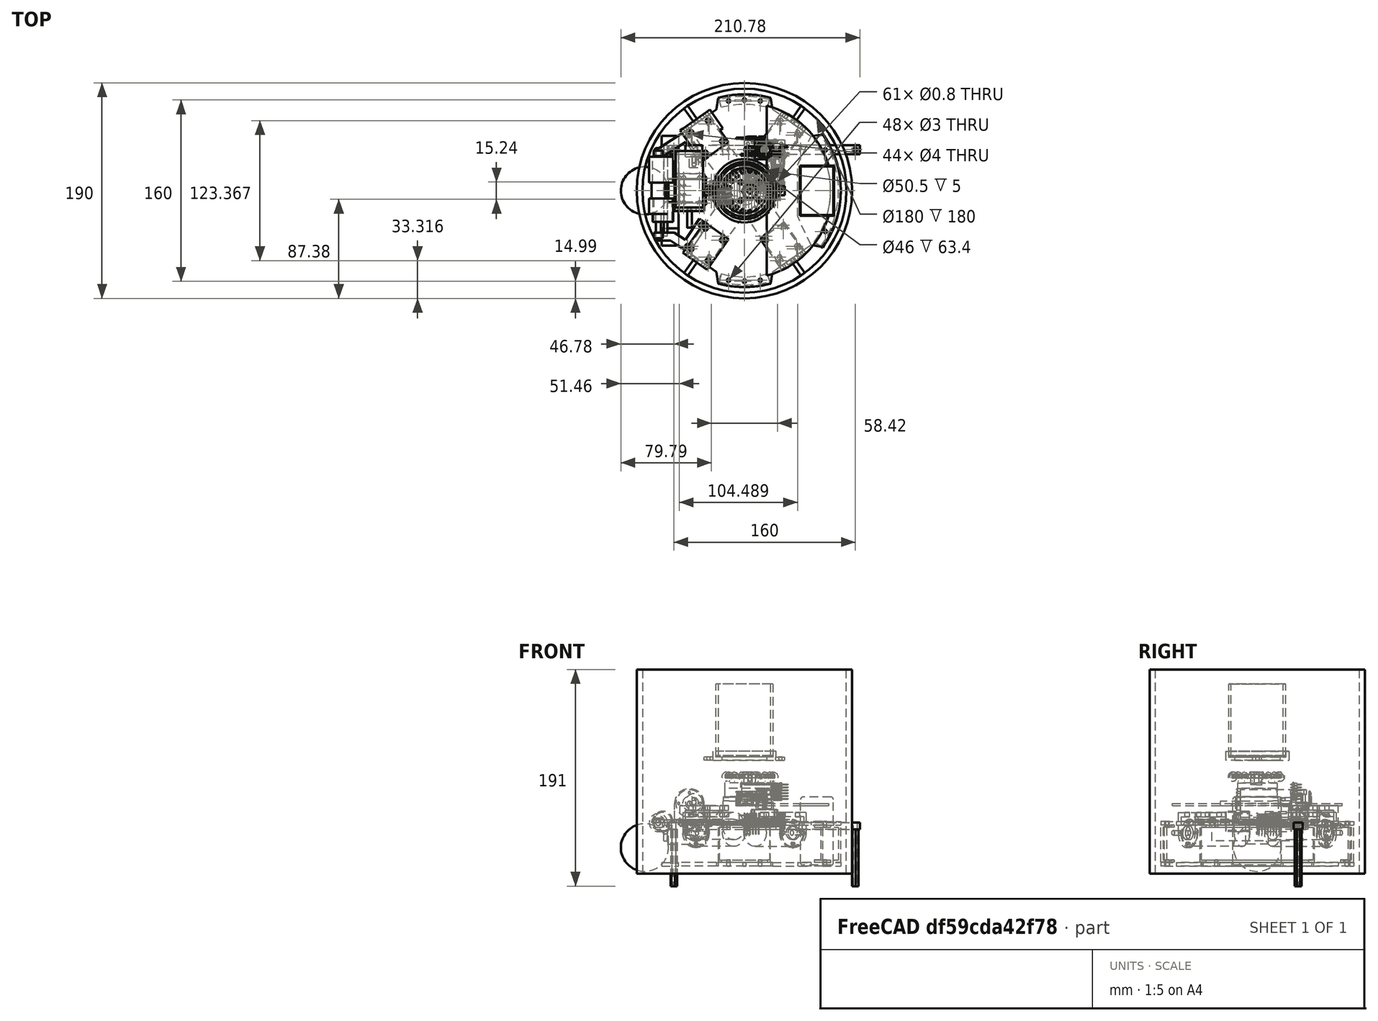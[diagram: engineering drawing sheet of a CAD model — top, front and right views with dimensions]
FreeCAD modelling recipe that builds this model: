
FCSTD DOCUMENT  (FreeCAD 0.21R33668 +7 (Git))
Label: SN9-10_model
License: All rights reserved
LicenseURL: https://en.wikipedia.org/wiki/All_rights_reserved
objects: Part::Feature×304, Sketcher::SketchObject×75, App::Part×51, PartDesign::Pad×48, PartDesign::Pocket×47, PartDesign::Body×31, PartDesign::SubShapeBinder×27, PartDesign::PolarPattern×11, PartDesign::Revolution×4, Part::FeaturePython×2, Part::Sphere×1, PartDesign::Fillet×1, Part::Cylinder×1, Part::Cut×1
note: 653 computed .brp shape members not serialized (recipe doc carries the construction recipe); baked Part::Feature solids carry a one-line shape summary decoded from their .brp

FEATURE [Sketcher::SketchObject] Sketch
  FullyConstrained = true
  MapMode = 5
  Support = -> [XY_Plane008]
  sketch-geometry (1):
    g0: Circle CenterX=0 CenterY=0 CenterZ=0 NormalX=0 NormalY=0 NormalZ=1 AngleXU=0 Radius=85
  constraints (2):
    c: Coincident(g0,g-1)
    c: Diameter(g0) = 170
FEATURE [Sketcher::SketchObject] Sketch005
  FullyConstrained = true
  MapMode = 5
  Placement = pos=(0,0,0) rot=(1,0,0;1.5708rad)
  Support = -> [XZ_Plane009]
  sketch-geometry (6):
    g0: ArcOfHyperbola CenterX=0 CenterY=94.5 CenterZ=0 NormalX=0 NormalY=0 NormalZ=1 MajorRadius=17.5 MinorRadius=15.6742 AngleXU=1.5708 StartAngle=0 EndAngle=1.02375
    g1: LineSegment StartX=5e-16 StartY=112 StartZ=0 EndX=-5e-16 EndY=77 EndZ=0
    g2: LineSegment StartX=-15.6742 StartY=112 StartZ=0 EndX=15.6742 EndY=112 EndZ=0
    g3: GeomPoint X=2.6e-15 Y=117.993 Z=0
    g4: LineSegment StartX=-19 StartY=122 StartZ=0 EndX=0 EndY=122 EndZ=0
    g5: LineSegment StartX=0 StartY=112 StartZ=0 EndX=0 EndY=122 EndZ=0
  constraints (15):
    c: InternalAlignment(g1,g0)
    c: InternalAlignment(g2,g0)
    c: InternalAlignment(g3,g0)
    c: Horizontal(g2)
    c: PointOnObject(g0,g-2)
    c: PointOnObject(g0,g-2)
    c: DistanceY(g0,g0) = 10
    c: DistanceX(g0,g0) = 19
    c: DistanceY(g1,g0) = 35
    c: Coincident(g4,g0)
    c: Coincident(g5,g0)
    c: Coincident(g5,g4)
    c: Vertical(g5)
    c: Horizontal(g4)
    c: DistanceY(g-1,g0) = 112
FEATURE [PartDesign::Pad] Pad  label="Structural layer"
  Direction = (0,0,1)
  Length = 3
  Length2 = 10
  Profile = -> Sketch
  ReferenceAxis = -> Sketch [N_Axis]
  Type = 0
FEATURE [Sketcher::SketchObject] Sketch001
  ExternalGeometry = -> [Pad]
  FullyConstrained = false
  MapMode = 5
  Placement = pos=(0,0,3) rot=(0,0,1;0rad)
  Support = -> [Pad]
  sketch-geometry (7):
    g0: LineSegment StartX=-10.6686 StartY=100.741 StartZ=0 EndX=44.4806 EndY=91.0164 EndZ=0
    g1: LineSegment StartX=44.4806 StartY=91.0164 StartZ=0 EndX=41.5109 EndY=74.1744 EndZ=0
    g2: LineSegment StartX=32.942 StartY=68.1744 StartZ=0 EndX=-7.63834 EndY=75.3298 EndZ=0
    g3: LineSegment StartX=-13.6383 StartY=83.8987 StartZ=0 EndX=-10.6686 EndY=100.741 EndZ=0
    g4: LineSegment StartX=32.942 StartY=68.1744 StartZ=0 EndX=41.5109 EndY=74.1744 EndZ=0
    g5: LineSegment StartX=-13.6383 StartY=83.8987 StartZ=0 EndX=-7.63834 EndY=75.3298 EndZ=0
    g6: LineSegment StartX=-98.5042 StartY=90.5189 StartZ=0 EndX=89.0462 EndY=57.4487 EndZ=0
  constraints (18):
    c: Coincident(g0,g1)
    c: Coincident(g3,g0)
    c: Coincident(g4,g2)
    c: Coincident(g4,g1)
    c: Coincident(g5,g3)
    c: Coincident(g5,g2)
    c: Angle(g4,g2) = 2.35619
    c: Angle(g2,g5) = 2.35619
    c: DistanceX(g3,g2) = 6
    c: Angle(g6,g-1) = 0.174533
    c: Parallel(g2,g6)
    c: Parallel(g0,g2)
    c: Perpendicular(g6,g1)
    c: Equal(g1,g3)
    c: Parallel(g1,g3)
    c: PointOnObject(g3,g-3)
    c: PointOnObject(g1,g-3)
    c: Distance(g0) = 56
FEATURE [PartDesign::Pocket] Pocket
  BaseFeature = -> Pad
  Direction = (0,0,-1)
  Length = 5
  Length2 = 5
  Profile = -> Sketch001
  ReferenceAxis = -> Sketch001 [N_Axis]
  Type = 1
FEATURE [PartDesign::PolarPattern] PolarPattern
  Angle = 110
  Axis = -> Sketch001 [N_Axis]
  BaseFeature = -> Pocket
  Occurrences = 2
  Originals = -> [Pocket]
FEATURE [PartDesign::Revolution] Revolution
  Angle = 360
  Axis = (0,-2e-16,1)
  Base = (0,0,0)
  Placement = pos=(0,0,0) rot=(1,0,0;1.5708rad)
  Profile = -> Sketch005
  ReferenceAxis = -> Sketch005 [V_Axis]
FEATURE [Sketcher::SketchObject] Sketch015
  FullyConstrained = true
  MapMode = 5
  Placement = pos=(0,0,3) rot=(0,0,1;0rad)
  Support = -> [PolarPattern]
  sketch-geometry (4):
    g0: LineSegment StartX=-111 StartY=31 StartZ=0 EndX=-31 EndY=111 EndZ=0
    g1: LineSegment StartX=-31 StartY=111 StartZ=0 EndX=-1 EndY=81 EndZ=0
    g2: LineSegment StartX=-1 StartY=81 StartZ=0 EndX=-81 EndY=1 EndZ=0
    g3: LineSegment StartX=-81 StartY=1 StartZ=0 EndX=-111 EndY=31 EndZ=0
  constraints (12):
    c: Coincident(g0,g1)
    c: Coincident(g1,g2)
    c: Coincident(g2,g3)
    c: Coincident(g3,g0)
    c: Equal(g3,g1)
    c: Equal(g0,g2)
    c: Angle(g3,g0) = 1.5708
    c: DistanceX(g2,g-1) = 81
    c: DistanceY(g-1,g1) = 81
    c: DistanceX(g0,g1) = 30
    c: DistanceX(g2,g1) = 80
    c: Angle(g-1,g2) = 0.785398
FEATURE [PartDesign::Pocket] Pocket004
  BaseFeature = -> PolarPattern
  Direction = (0,0,-1)
  Length = 5
  Length2 = 5
  Profile = -> Sketch015
  ReferenceAxis = -> Sketch015 [N_Axis]
  Type = 1
FEATURE [Sketcher::SketchObject] Sketch016
  FullyConstrained = true
  MapMode = 5
  Placement = pos=(0,0,0) rot=(1,0,0;1.5708rad)
  Support = -> [XZ_Plane016]
  sketch-geometry (8):
    g0: LineSegment StartX=-88 StartY=-1 StartZ=0 EndX=-79 EndY=-1 EndZ=0
    g1: LineSegment StartX=-79 StartY=-34 StartZ=0 EndX=-88 EndY=-34 EndZ=0
    g2: LineSegment StartX=-88 StartY=-34 StartZ=0 EndX=-88 EndY=-1 EndZ=0
    g3: LineSegment StartX=-79 StartY=-1 StartZ=0 EndX=-79 EndY=-3 EndZ=0
    g4: LineSegment StartX=-79 StartY=-3 StartZ=0 EndX=-86 EndY=-3 EndZ=0
    g5: LineSegment StartX=-86 StartY=-3 StartZ=0 EndX=-86 EndY=-32 EndZ=0
    g6: LineSegment StartX=-86 StartY=-32 StartZ=0 EndX=-79 EndY=-32 EndZ=0
    g7: LineSegment StartX=-79 StartY=-32 StartZ=0 EndX=-79 EndY=-34 EndZ=0
  constraints (24):
    c: Coincident(g1,g2)
    c: Coincident(g2,g0)
    c: Horizontal(g0)
    c: Horizontal(g1)
    c: Vertical(g2)
    c: DistanceY(g1,g0) = 33
    c: DistanceX(g1,g1) = 9
    c: DistanceX(g0,g-1) = 88
    c: DistanceY(g1,g-1) = 34
    c: Equal(g1,g0)
    c: Coincident(g3,g0)
    c: Vertical(g3)
    c: Coincident(g4,g3)
    c: Horizontal(g4)
    c: Coincident(g5,g4)
    c: Vertical(g5)
    c: Coincident(g6,g5)
    c: Horizontal(g6)
    c: Coincident(g7,g6)
    c: Coincident(g7,g1)
    c: Vertical(g7)
    c: Equal(g3,g7)
    c: DistanceY(g3,g3) = 2
    c: DistanceX(g0,g4) = 2
FEATURE [PartDesign::Revolution] Revolution001
  Angle = 30
  Axis = (1e-16,1e-16,1)
  Base = (0,0,0)
  Midplane = true
  Placement = pos=(0,0,0) rot=(1,0,0;1.5708rad)
  Profile = -> Sketch016
  ReferenceAxis = -> Z_Axis016
  Reversed = true
FEATURE [Part::Feature] Part__Feature268  label="OmniBase_Predeterminado004"
  Placement = pos=(4.80373,-0.638646,40.5) rot=(0,0,1;0rad)
  shape: bbox 44 x 43.9 x 9 mm, 104 faces (baked)
FEATURE [Part::Feature] Part__Feature269  label="Roller_Predeterminado072"
  Placement = pos=(4.80373,20.3614,41.6192) rot=(0,0,1;0rad)
  shape: bbox 2.6 x 8.659 x 8.659 mm, 10 faces (baked)
FEATURE [Part::Feature] Part__Feature270  label="Roller_Predeterminado073"
  Placement = pos=(-2.3787,19.0949,41.6192) rot=(0,0,1;0.349066rad)
  shape: bbox 4.664 x 8.342 x 8.659 mm, 10 faces (baked)
FEATURE [Part::Feature] Part__Feature271  label="Roller_Predeterminado074"
  Placement = pos=(-8.69481,15.4483,41.6192) rot=(0,0,1;0.698132rad)
  shape: bbox 6.71 x 7.451 x 8.659 mm, 10 faces (baked)
FEATURE [Part::Feature] Part__Feature272  label="Roller_Predeterminado075"
  Placement = pos=(-13.3828,9.86135,41.6192) rot=(0,0,1;1.0472rad)
  shape: bbox 7.965 x 5.765 x 8.659 mm, 10 faces (baked)
FEATURE [Part::Feature] Part__Feature273  label="Roller_Predeterminado076"
  Placement = pos=(-15.8772,3.00797,41.6192) rot=(0,0,1;1.39626rad)
  shape: bbox 8.632 x 3.688 x 8.659 mm, 10 faces (baked)
FEATURE [Part::Feature] Part__Feature274  label="Roller_Predeterminado077"
  Placement = pos=(-15.8772,-4.28526,41.6192) rot=(0,0,1;1.74533rad)
  shape: bbox 8.632 x 3.688 x 8.659 mm, 10 faces (baked)
FEATURE [Part::Feature] Part__Feature275  label="Roller_Predeterminado078"
  Placement = pos=(-13.3828,-11.1386,41.6192) rot=(0,0,1;2.0944rad)
  shape: bbox 7.965 x 5.765 x 8.659 mm, 10 faces (baked)
FEATURE [Part::Feature] Part__Feature276  label="Roller_Predeterminado079"
  Placement = pos=(-8.69481,-16.7256,41.6192) rot=(0,0,1;2.44346rad)
  shape: bbox 6.71 x 7.451 x 8.659 mm, 10 faces (baked)
FEATURE [Part::Feature] Part__Feature277  label="Roller_Predeterminado080"
  Placement = pos=(-2.3787,-20.3722,41.6192) rot=(0,0,1;2.79253rad)
  shape: bbox 4.664 x 8.342 x 8.659 mm, 10 faces (baked)
FEATURE [Part::Feature] Part__Feature278  label="Roller_Predeterminado081"
  Placement = pos=(4.80373,-21.6386,41.6192) rot=(0,0,1;3.14159rad)
  shape: bbox 2.6 x 8.659 x 8.659 mm, 10 faces (baked)
FEATURE [Part::Feature] Part__Feature279  label="Roller_Predeterminado082"
  Placement = pos=(11.9862,-20.3722,41.6192) rot=(0,0,1;3.49066rad)
  shape: bbox 4.664 x 8.342 x 8.659 mm, 10 faces (baked)
FEATURE [Part::Feature] Part__Feature280  label="Roller_Predeterminado083"
  Placement = pos=(18.3023,-16.7256,41.6192) rot=(0,0,1;3.83972rad)
  shape: bbox 6.71 x 7.451 x 8.659 mm, 10 faces (baked)
FEATURE [Part::Feature] Part__Feature281  label="Roller_Predeterminado084"
  Placement = pos=(22.9903,-11.1386,41.6192) rot=(0,0,-1;2.0944rad)
  shape: bbox 7.965 x 5.765 x 8.659 mm, 10 faces (baked)
FEATURE [Part::Feature] Part__Feature282  label="Roller_Predeterminado085"
  Placement = pos=(25.4847,-4.28526,41.6192) rot=(0,0,-1;1.74533rad)
  shape: bbox 8.632 x 3.688 x 8.659 mm, 10 faces (baked)
FEATURE [Part::Feature] Part__Feature283  label="Roller_Predeterminado086"
  Placement = pos=(25.4847,3.00797,41.6192) rot=(0,0,-1;1.39626rad)
  shape: bbox 8.632 x 3.688 x 8.659 mm, 10 faces (baked)
FEATURE [Part::Feature] Part__Feature284  label="Roller_Predeterminado087"
  Placement = pos=(22.9903,9.86135,41.6192) rot=(0,0,-1;1.0472rad)
  shape: bbox 7.965 x 5.765 x 8.659 mm, 10 faces (baked)
FEATURE [Part::Feature] Part__Feature285  label="Roller_Predeterminado088"
  Placement = pos=(18.3023,15.4483,41.6192) rot=(0,0,-1;0.698132rad)
  shape: bbox 6.71 x 7.451 x 8.659 mm, 10 faces (baked)
FEATURE [Part::Feature] Part__Feature286  label="Roller_Predeterminado089"
  Placement = pos=(11.9862,19.0949,41.6192) rot=(0,0,-1;0.349066rad)
  shape: bbox 4.664 x 8.342 x 8.659 mm, 10 faces (baked)
FEATURE [Part::Feature] Part__Feature287  label="Nut_Predeterminado004"
  Placement = pos=(4.80373,-0.638646,43.5) rot=(0,0,1;1.0472rad)
  shape: bbox 13.86 x 12.93 x 2 mm, 24 faces (baked)
FEATURE [App::Part] OmniWheel054  label="OmniWheel 1"
  Group = -> [Part__Feature268,Part__Feature269,Part__Feature270,Part__Feature271,Part__Feature272,Part__Feature273,Part__Feature274,Part__Feature275,Part__Feature276,Part__Feature277,Part__Feature278,Part__Feature279,Part__Feature280,Part__Feature281,Part__Feature282,Part__Feature283,Part__Feature284,Part__Feature285,Part__Feature286,Part__Feature287]
  Origin = -> Origin019
  Placement = pos=(-23.8855,35.1581,-6.8) rot=(-0.419215,-0.805305,-0.419215;1.78566rad)
FEATURE [Sketcher::SketchObject] Sketch023
  FullyConstrained = true
  MapMode = 5
  Support = -> [XY_Plane024]
  sketch-geometry (9):
    g0: Circle CenterX=0 CenterY=0 CenterZ=0 NormalX=0 NormalY=0 NormalZ=1 AngleXU=0 Radius=20
    g1: LineSegment StartX=27.7128 StartY=-4 StartZ=0 EndX=35.7128 EndY=-4 EndZ=0
    g2: LineSegment StartX=35.7128 StartY=-4 StartZ=0 EndX=35.7128 EndY=4 EndZ=0
    g3: LineSegment StartX=35.7128 StartY=4 StartZ=0 EndX=27.7128 EndY=4 EndZ=0
    g4: LineSegment StartX=-27.7128 StartY=-4 StartZ=0 EndX=-35.7128 EndY=-4 EndZ=0
    g5: LineSegment StartX=-35.7128 StartY=-4 StartZ=0 EndX=-35.7128 EndY=4 EndZ=0
    g6: LineSegment StartX=-35.7128 StartY=4 StartZ=0 EndX=-27.7128 EndY=4 EndZ=0
    g7: ArcOfCircle CenterX=0 CenterY=0 CenterZ=0 NormalX=0 NormalY=0 NormalZ=1 AngleXU=0 Radius=28 StartAngle=0.143348 EndAngle=2.99825
    g8: ArcOfCircle CenterX=0 CenterY=0 CenterZ=0 NormalX=0 NormalY=0 NormalZ=1 AngleXU=0 Radius=28 StartAngle=3.28494 EndAngle=6.13984
  constraints (25):
    c: Coincident(g0,g-1)
    c: Diameter(g0) = 40
    c: Horizontal(g1)
    c: Coincident(g2,g1)
    c: Coincident(g3,g2)
    c: Horizontal(g3)
    c: Horizontal(g4)
    c: Coincident(g5,g4)
    c: Vertical(g5)
    c: Coincident(g6,g5)
    c: Horizontal(g6)
    c: Coincident(g7,g0)
    c: Coincident(g7,g6)
    c: Coincident(g7,g3)
    c: Coincident(g8,g0)
    c: Coincident(g8,g4)
    c: Coincident(g8,g1)
    c: Diameter(g7) = 56
    c: Diameter(g8) = 56
    c: Symmetric(g1,g2,g-1)
    c: Equal(g5,g2)
    c: Equal(g6,g3)
    c: Equal(g4,g1)
    c: DistanceY(g2,g2) = 8
    c: DistanceX(g6,g6) = 8
FEATURE [PartDesign::Pad] Pad007
  Direction = (0,0,1)
  Length = 3
  Length2 = 10
  Profile = -> Sketch023
  ReferenceAxis = -> Sketch023 [N_Axis]
  Type = 0
FEATURE [Sketcher::SketchObject] Sketch025
  FullyConstrained = true
  MapMode = 5
  Support = -> [XY_Plane026]
  sketch-geometry (2):
    g0: Circle CenterX=0 CenterY=0 CenterZ=0 NormalX=0 NormalY=0 NormalZ=1 AngleXU=0 Radius=90
    g1: Circle CenterX=0 CenterY=0 CenterZ=0 NormalX=0 NormalY=0 NormalZ=1 AngleXU=0 Radius=95
  constraints (4):
    c: Diameter(g0) = 180
    c: Coincident(g1,g-1)
    c: Diameter(g1) = 190
    c: Coincident(g0,g-1)
FEATURE [PartDesign::Pad] Pad008
  Direction = (0,0,1)
  Length = 180
  Length2 = 10
  Profile = -> Sketch025
  ReferenceAxis = -> Sketch025 [N_Axis]
  Type = 0
FEATURE [PartDesign::Body] Body008  label="Cylinder"
  Group = -> [Sketch025,Pad008]
  Origin = -> Origin026
  Placement = pos=(0,0,-44) rot=(0,0,1;0rad)
  Tip = -> Pad008
FEATURE [Sketcher::SketchObject] Sketch061
  FullyConstrained = true
  MapMode = 5
  Placement = pos=(0,0,2) rot=(0,0,1;0rad)
  sketch-geometry (1):
    g0: Circle CenterX=0 CenterY=0 CenterZ=0 NormalX=0 NormalY=0 NormalZ=1 AngleXU=0 Radius=12.5
  constraints (2):
    c: Coincident(g0,g-1)
    c: Diameter(g0) = 25
FEATURE [PartDesign::Pocket] Pocket019
  BaseFeature = -> Pocket004
  Direction = (0,0,-1)
  Length = 5
  Length2 = 5
  Profile = -> Sketch061
  ReferenceAxis = -> Sketch061 [N_Axis]
  Type = 4
FEATURE [Part::Feature] Part__Feature439  label="114-00841-68--3DModel-STEP-56544 v1"
  Placement = pos=(24.0935,-0.00012972,0.814608) rot=(0.57735,0.57735,0.57735;2.0944rad)
  shape: bbox 11.35 x 11.95 x 1.68 mm, 239 faces (baked)
FEATURE [Part::Feature] Part__Feature453  label="MIMXRT1052CVJ5B v1"
  Placement = pos=(1.30183,-0.0809243,0.815) rot=(0,0.707107,0.707107;3.14159rad)
  shape: bbox 12 x 12 x 1.27 mm, 6 faces (baked)
FEATURE [App::Part] MIMXRT1052CVJ5B_v1  label="MIMXRT1052CVJ5B v198"
  Group = -> [Part__Feature453]
  Origin = -> Origin053
FEATURE [Part::Feature] Part__Feature589  label="MicroUSB Molex 473460001 v1"
  Placement = pos=(-28.9499,0.13174,2.07033) rot=(0.57735,-0.57735,-0.57735;2.0944rad)
  shape: bbox 5.43 x 7.98 x 2.94 mm, 406 faces (baked)
FEATURE [Part::Feature] Part__Feature590  label="COMPOUND"
  shape: bbox 2.54 x 2.54 x 2.799 mm, 22 faces, 0 solids (baked)
FEATURE [Part::Feature] Part__Feature591  label="COMPOUND001"
  shape: bbox 2.54 x 2.54 x 2.799 mm, 22 faces, 0 solids (baked)
FEATURE [Part::Feature] Part__Feature592  label="COMPOUND002"
  shape: bbox 2.54 x 2.54 x 2.799 mm, 23 faces, 0 solids (baked)
FEATURE [Part::Feature] Part__Feature593  label="COMPOUND003"
  shape: bbox 2.54 x 2.54 x 2.799 mm, 22 faces, 0 solids (baked)
FEATURE [Part::Feature] Part__Feature594  label="COMPOUND004"
  shape: bbox 2.54 x 2.54 x 2.799 mm, 22 faces, 0 solids (baked)
FEATURE [Part::Feature] Part__Feature595  label="COMPOUND005"
  shape: bbox 2.54 x 2.54 x 2.799 mm, 23 faces, 0 solids (baked)
FEATURE [App::Part] COMPOUND  label="COMPOUND006"
  Group = -> [Part__Feature590,Part__Feature591,Part__Feature592,Part__Feature593,Part__Feature594,Part__Feature595]
  Origin = -> Origin055
FEATURE [Part::Feature] Part__Feature596  label="COMPOUND007"
  shape: bbox 0.6304 x 0.63 x 12.7 mm, 14 faces (baked)
FEATURE [Part::Feature] Part__Feature597  label="COMPOUND008"
  shape: bbox 0.6304 x 0.63 x 12.7 mm, 14 faces (baked)
FEATURE [Part::Feature] Part__Feature598  label="COMPOUND009"
  shape: bbox 0.6304 x 0.63 x 12.7 mm, 14 faces (baked)
FEATURE [Part::Feature] Part__Feature599  label="COMPOUND010"
  shape: bbox 0.6304 x 0.63 x 12.7 mm, 14 faces (baked)
FEATURE [Part::Feature] Part__Feature600  label="COMPOUND011"
  shape: bbox 0.6304 x 0.63 x 12.7 mm, 14 faces (baked)
FEATURE [Part::Feature] Part__Feature601  label="COMPOUND012"
  shape: bbox 0.6304 x 0.63 x 12.7 mm, 14 faces (baked)
FEATURE [App::Part] COMPOUND001  label="COMPOUND013"
  Group = -> [Part__Feature596,Part__Feature597,Part__Feature598,Part__Feature599,Part__Feature600,Part__Feature601]
  Origin = -> Origin056
FEATURE [App::Part] Pin_Header_1x6_TH_Pitch_2_54mm_v1  label="Pin Header 1x6 TH Pitch 2.54mm v1"
  Group = -> [COMPOUND,COMPOUND001]
  Origin = -> Origin054
  Placement = pos=(-16.51,-7.62,-0.814) rot=(0,1,0;3.14159rad)
FEATURE [Part::Feature] Part__Feature602  label="COMPOUND014"
  shape: bbox 2.54 x 2.54 x 2.799 mm, 22 faces, 0 solids (baked)
FEATURE [Part::Feature] Part__Feature603  label="COMPOUND015"
  shape: bbox 2.54 x 2.54 x 2.799 mm, 22 faces, 0 solids (baked)
FEATURE [Part::Feature] Part__Feature604  label="COMPOUND016"
  shape: bbox 2.54 x 2.54 x 2.799 mm, 23 faces, 0 solids (baked)
FEATURE [Part::Feature] Part__Feature605  label="COMPOUND017"
  shape: bbox 2.54 x 2.54 x 2.799 mm, 22 faces, 0 solids (baked)
FEATURE [Part::Feature] Part__Feature606  label="COMPOUND018"
  shape: bbox 2.54 x 2.54 x 2.799 mm, 22 faces, 0 solids (baked)
FEATURE [Part::Feature] Part__Feature607  label="COMPOUND019"
  shape: bbox 2.54 x 2.54 x 2.799 mm, 23 faces, 0 solids (baked)
FEATURE [App::Part] COMPOUND002  label="COMPOUND020"
  Group = -> [Part__Feature602,Part__Feature603,Part__Feature604,Part__Feature605,Part__Feature606,Part__Feature607]
  Origin = -> Origin058
FEATURE [Part::Feature] Part__Feature608  label="COMPOUND021"
  shape: bbox 0.6304 x 0.63 x 12.7 mm, 14 faces (baked)
FEATURE [Part::Feature] Part__Feature609  label="COMPOUND022"
  shape: bbox 0.6304 x 0.63 x 12.7 mm, 14 faces (baked)
FEATURE [Part::Feature] Part__Feature610  label="COMPOUND023"
  shape: bbox 0.6304 x 0.63 x 12.7 mm, 14 faces (baked)
FEATURE [Part::Feature] Part__Feature611  label="COMPOUND024"
  shape: bbox 0.6304 x 0.63 x 12.7 mm, 14 faces (baked)
FEATURE [Part::Feature] Part__Feature612  label="COMPOUND025"
  shape: bbox 0.6304 x 0.63 x 12.7 mm, 14 faces (baked)
FEATURE [Part::Feature] Part__Feature613  label="COMPOUND026"
  shape: bbox 0.6304 x 0.63 x 12.7 mm, 14 faces (baked)
FEATURE [App::Part] COMPOUND003  label="COMPOUND027"
  Group = -> [Part__Feature608,Part__Feature609,Part__Feature610,Part__Feature611,Part__Feature612,Part__Feature613]
  Origin = -> Origin059
FEATURE [App::Part] Pin_Header_1x6_TH_Pitch_2_54mm_v002  label="Pin Header 1x6 TH Pitch 2.54mm v002"
  Group = -> [COMPOUND002,COMPOUND003]
  Origin = -> Origin057
  Placement = pos=(-1.27,-7.62,-0.814) rot=(0,1,0;3.14159rad)
FEATURE [Part::Feature] Part__Feature614  label="COMPOUND028"
  shape: bbox 2.54 x 2.54 x 2.799 mm, 22 faces, 0 solids (baked)
FEATURE [Part::Feature] Part__Feature615  label="COMPOUND029"
  shape: bbox 2.54 x 2.54 x 2.799 mm, 22 faces, 0 solids (baked)
FEATURE [Part::Feature] Part__Feature616  label="COMPOUND030"
  shape: bbox 2.54 x 2.54 x 2.799 mm, 23 faces, 0 solids (baked)
FEATURE [Part::Feature] Part__Feature617  label="COMPOUND031"
  shape: bbox 2.54 x 2.54 x 2.799 mm, 22 faces, 0 solids (baked)
FEATURE [Part::Feature] Part__Feature618  label="COMPOUND032"
  shape: bbox 2.54 x 2.54 x 2.799 mm, 22 faces, 0 solids (baked)
FEATURE [Part::Feature] Part__Feature619  label="COMPOUND033"
  shape: bbox 2.54 x 2.54 x 2.799 mm, 23 faces, 0 solids (baked)
FEATURE [App::Part] COMPOUND004  label="COMPOUND034"
  Group = -> [Part__Feature614,Part__Feature615,Part__Feature616,Part__Feature617,Part__Feature618,Part__Feature619]
  Origin = -> Origin060
FEATURE [Part::Feature] Part__Feature620  label="COMPOUND035"
  shape: bbox 0.6304 x 0.63 x 12.7 mm, 14 faces (baked)
FEATURE [Part::Feature] Part__Feature621  label="COMPOUND036"
  shape: bbox 0.6304 x 0.63 x 12.7 mm, 14 faces (baked)
FEATURE [Part::Feature] Part__Feature622  label="COMPOUND037"
  shape: bbox 0.6304 x 0.63 x 12.7 mm, 14 faces (baked)
FEATURE [Part::Feature] Part__Feature623  label="COMPOUND038"
  shape: bbox 0.6304 x 0.63 x 12.7 mm, 14 faces (baked)
FEATURE [Part::Feature] Part__Feature624  label="COMPOUND039"
  shape: bbox 0.6304 x 0.63 x 12.7 mm, 14 faces (baked)
FEATURE [Part::Feature] Part__Feature625  label="COMPOUND040"
  shape: bbox 0.6304 x 0.63 x 12.7 mm, 14 faces (baked)
FEATURE [App::Part] COMPOUND005  label="COMPOUND041"
  Group = -> [Part__Feature620,Part__Feature621,Part__Feature622,Part__Feature623,Part__Feature624,Part__Feature625]
  Origin = -> Origin010
FEATURE [App::Part] Pin_Header_1x6_TH_Pitch_2_54mm_v003  label="Pin Header 1x6 TH Pitch 2.54mm v003"
  Group = -> [COMPOUND004,COMPOUND005]
  Origin = -> Origin011
  Placement = pos=(13.97,-7.62,-0.814) rot=(0,1,0;3.14159rad)
FEATURE [Part::Feature] Part__Feature626  label="COMPOUND042"
  shape: bbox 2.54 x 2.54 x 2.799 mm, 22 faces, 0 solids (baked)
FEATURE [Part::Feature] Part__Feature627  label="COMPOUND043"
  shape: bbox 2.54 x 2.54 x 2.799 mm, 22 faces, 0 solids (baked)
FEATURE [Part::Feature] Part__Feature628  label="COMPOUND044"
  shape: bbox 2.54 x 2.54 x 2.799 mm, 23 faces, 0 solids (baked)
FEATURE [Part::Feature] Part__Feature629  label="COMPOUND045"
  shape: bbox 2.54 x 2.54 x 2.799 mm, 22 faces, 0 solids (baked)
FEATURE [Part::Feature] Part__Feature630  label="COMPOUND046"
  shape: bbox 2.54 x 2.54 x 2.799 mm, 22 faces, 0 solids (baked)
FEATURE [Part::Feature] Part__Feature631  label="COMPOUND047"
  shape: bbox 2.54 x 2.54 x 2.799 mm, 23 faces, 0 solids (baked)
FEATURE [App::Part] COMPOUND006  label="COMPOUND048"
  Group = -> [Part__Feature626,Part__Feature627,Part__Feature628,Part__Feature629,Part__Feature630,Part__Feature631]
  Origin = -> Origin012
FEATURE [Part::Feature] Part__Feature632  label="COMPOUND049"
  shape: bbox 0.6304 x 0.63 x 12.7 mm, 14 faces (baked)
FEATURE [Part::Feature] Part__Feature633  label="COMPOUND050"
  shape: bbox 0.6304 x 0.63 x 12.7 mm, 14 faces (baked)
FEATURE [Part::Feature] Part__Feature634  label="COMPOUND051"
  shape: bbox 0.6304 x 0.63 x 12.7 mm, 14 faces (baked)
FEATURE [Part::Feature] Part__Feature635  label="COMPOUND052"
  shape: bbox 0.6304 x 0.63 x 12.7 mm, 14 faces (baked)
FEATURE [Part::Feature] Part__Feature636  label="COMPOUND053"
  shape: bbox 0.6304 x 0.63 x 12.7 mm, 14 faces (baked)
FEATURE [Part::Feature] Part__Feature637  label="COMPOUND054"
  shape: bbox 0.6304 x 0.63 x 12.7 mm, 14 faces (baked)
FEATURE [App::Part] COMPOUND007  label="COMPOUND055"
  Group = -> [Part__Feature632,Part__Feature633,Part__Feature634,Part__Feature635,Part__Feature636,Part__Feature637]
  Origin = -> Origin013
FEATURE [App::Part] Pin_Header_1x6_TH_Pitch_2_54mm_v004  label="Pin Header 1x6 TH Pitch 2.54mm v004"
  Group = -> [COMPOUND006,COMPOUND007]
  Origin = -> Origin014
  Placement = pos=(29.21,-7.62,-0.814) rot=(0,1,0;3.14159rad)
FEATURE [Part::Feature] Part__Feature638  label="COMPOUND056"
  shape: bbox 2.54 x 2.54 x 2.799 mm, 22 faces, 0 solids (baked)
FEATURE [Part::Feature] Part__Feature639  label="COMPOUND057"
  shape: bbox 2.54 x 2.54 x 2.799 mm, 22 faces, 0 solids (baked)
FEATURE [Part::Feature] Part__Feature640  label="COMPOUND058"
  shape: bbox 2.54 x 2.54 x 2.799 mm, 23 faces, 0 solids (baked)
FEATURE [Part::Feature] Part__Feature641  label="COMPOUND059"
  shape: bbox 2.54 x 2.54 x 2.799 mm, 22 faces, 0 solids (baked)
FEATURE [Part::Feature] Part__Feature642  label="COMPOUND060"
  shape: bbox 2.54 x 2.54 x 2.799 mm, 22 faces, 0 solids (baked)
FEATURE [Part::Feature] Part__Feature643  label="COMPOUND061"
  shape: bbox 2.54 x 2.54 x 2.799 mm, 23 faces, 0 solids (baked)
FEATURE [App::Part] COMPOUND008  label="COMPOUND062"
  Group = -> [Part__Feature638,Part__Feature639,Part__Feature640,Part__Feature641,Part__Feature642,Part__Feature643]
  Origin = -> Origin061
FEATURE [Part::Feature] Part__Feature644  label="COMPOUND063"
  shape: bbox 0.6304 x 0.63 x 12.7 mm, 14 faces (baked)
FEATURE [Part::Feature] Part__Feature645  label="COMPOUND064"
  shape: bbox 0.6304 x 0.63 x 12.7 mm, 14 faces (baked)
FEATURE [Part::Feature] Part__Feature646  label="COMPOUND065"
  shape: bbox 0.6304 x 0.63 x 12.7 mm, 14 faces (baked)
FEATURE [Part::Feature] Part__Feature647  label="COMPOUND066"
  shape: bbox 0.6304 x 0.63 x 12.7 mm, 14 faces (baked)
FEATURE [Part::Feature] Part__Feature648  label="COMPOUND067"
  shape: bbox 0.6304 x 0.63 x 12.7 mm, 14 faces (baked)
FEATURE [Part::Feature] Part__Feature649  label="COMPOUND068"
  shape: bbox 0.6304 x 0.63 x 12.7 mm, 14 faces (baked)
FEATURE [App::Part] COMPOUND009  label="COMPOUND069"
  Group = -> [Part__Feature644,Part__Feature645,Part__Feature646,Part__Feature647,Part__Feature648,Part__Feature649]
  Origin = -> Origin062
FEATURE [App::Part] Pin_Header_1x6_TH_Pitch_2_54mm_v1_Mirror_  label="Pin Header 1x6 TH Pitch 2.54mm v1(Mirror)"
  Group = -> [COMPOUND008,COMPOUND009]
  Origin = -> Origin017
  Placement = pos=(-16.51,7.62,-0.814) rot=(0,0,1;3.14159rad)
FEATURE [Part::Feature] Part__Feature650  label="COMPOUND070"
  shape: bbox 2.54 x 2.54 x 2.799 mm, 22 faces, 0 solids (baked)
FEATURE [Part::Feature] Part__Feature651  label="COMPOUND071"
  shape: bbox 2.54 x 2.54 x 2.799 mm, 22 faces, 0 solids (baked)
FEATURE [Part::Feature] Part__Feature652  label="COMPOUND072"
  shape: bbox 2.54 x 2.54 x 2.799 mm, 23 faces, 0 solids (baked)
FEATURE [Part::Feature] Part__Feature653  label="COMPOUND073"
  shape: bbox 2.54 x 2.54 x 2.799 mm, 22 faces, 0 solids (baked)
FEATURE [Part::Feature] Part__Feature654  label="COMPOUND074"
  shape: bbox 2.54 x 2.54 x 2.799 mm, 22 faces, 0 solids (baked)
FEATURE [Part::Feature] Part__Feature655  label="COMPOUND075"
  shape: bbox 2.54 x 2.54 x 2.799 mm, 23 faces, 0 solids (baked)
FEATURE [App::Part] COMPOUND010  label="COMPOUND076"
  Group = -> [Part__Feature650,Part__Feature651,Part__Feature652,Part__Feature653,Part__Feature654,Part__Feature655]
  Origin = -> Origin064
FEATURE [Part::Feature] Part__Feature656  label="COMPOUND077"
  shape: bbox 0.6304 x 0.63 x 12.7 mm, 14 faces (baked)
FEATURE [Part::Feature] Part__Feature657  label="COMPOUND078"
  shape: bbox 0.6304 x 0.63 x 12.7 mm, 14 faces (baked)
FEATURE [Part::Feature] Part__Feature658  label="COMPOUND079"
  shape: bbox 0.6304 x 0.63 x 12.7 mm, 14 faces (baked)
FEATURE [Part::Feature] Part__Feature659  label="COMPOUND080"
  shape: bbox 0.6304 x 0.63 x 12.7 mm, 14 faces (baked)
FEATURE [Part::Feature] Part__Feature660  label="COMPOUND081"
  shape: bbox 0.6304 x 0.63 x 12.7 mm, 14 faces (baked)
FEATURE [Part::Feature] Part__Feature661  label="COMPOUND082"
  shape: bbox 0.6304 x 0.63 x 12.7 mm, 14 faces (baked)
FEATURE [App::Part] COMPOUND011  label="COMPOUND083"
  Group = -> [Part__Feature656,Part__Feature657,Part__Feature658,Part__Feature659,Part__Feature660,Part__Feature661]
  Origin = -> Origin065
FEATURE [App::Part] Pin_Header_1x6_TH_Pitch_2_54mm_v1_Mirror_001  label="Pin Header 1x6 TH Pitch 2.54mm v1(Mirror)001"
  Group = -> [COMPOUND010,COMPOUND011]
  Origin = -> Origin063
  Placement = pos=(-1.27,7.62,-0.814) rot=(0,0,1;3.14159rad)
FEATURE [Part::Feature] Part__Feature662  label="COMPOUND084"
  shape: bbox 2.54 x 2.54 x 2.799 mm, 22 faces, 0 solids (baked)
FEATURE [Part::Feature] Part__Feature663  label="COMPOUND085"
  shape: bbox 2.54 x 2.54 x 2.799 mm, 22 faces, 0 solids (baked)
FEATURE [Part::Feature] Part__Feature664  label="COMPOUND086"
  shape: bbox 2.54 x 2.54 x 2.799 mm, 23 faces, 0 solids (baked)
FEATURE [Part::Feature] Part__Feature665  label="COMPOUND087"
  shape: bbox 2.54 x 2.54 x 2.799 mm, 22 faces, 0 solids (baked)
FEATURE [Part::Feature] Part__Feature666  label="COMPOUND088"
  shape: bbox 2.54 x 2.54 x 2.799 mm, 22 faces, 0 solids (baked)
FEATURE [Part::Feature] Part__Feature667  label="COMPOUND089"
  shape: bbox 2.54 x 2.54 x 2.799 mm, 23 faces, 0 solids (baked)
FEATURE [App::Part] COMPOUND012  label="COMPOUND090"
  Group = -> [Part__Feature662,Part__Feature663,Part__Feature664,Part__Feature665,Part__Feature666,Part__Feature667]
  Origin = -> Origin067
FEATURE [Part::Feature] Part__Feature668  label="COMPOUND091"
  shape: bbox 0.6304 x 0.63 x 12.7 mm, 14 faces (baked)
FEATURE [Part::Feature] Part__Feature669  label="COMPOUND092"
  shape: bbox 0.6304 x 0.63 x 12.7 mm, 14 faces (baked)
FEATURE [Part::Feature] Part__Feature670  label="COMPOUND093"
  shape: bbox 0.6304 x 0.63 x 12.7 mm, 14 faces (baked)
FEATURE [Part::Feature] Part__Feature671  label="COMPOUND094"
  shape: bbox 0.6304 x 0.63 x 12.7 mm, 14 faces (baked)
FEATURE [Part::Feature] Part__Feature672  label="COMPOUND095"
  shape: bbox 0.6304 x 0.63 x 12.7 mm, 14 faces (baked)
FEATURE [Part::Feature] Part__Feature673  label="COMPOUND096"
  shape: bbox 0.6304 x 0.63 x 12.7 mm, 14 faces (baked)
FEATURE [App::Part] COMPOUND013  label="COMPOUND097"
  Group = -> [Part__Feature668,Part__Feature669,Part__Feature670,Part__Feature671,Part__Feature672,Part__Feature673]
  Origin = -> Origin022
FEATURE [App::Part] Pin_Header_1x6_TH_Pitch_2_54mm_v1_Mirror_002  label="Pin Header 1x6 TH Pitch 2.54mm v1(Mirror)002"
  Group = -> [COMPOUND012,COMPOUND013]
  Origin = -> Origin066
  Placement = pos=(13.97,7.62,-0.814) rot=(0,0,1;3.14159rad)
FEATURE [Part::Feature] Part__Feature674  label="COMPOUND098"
  shape: bbox 2.54 x 2.54 x 2.799 mm, 22 faces, 0 solids (baked)
FEATURE [Part::Feature] Part__Feature675  label="COMPOUND099"
  shape: bbox 2.54 x 2.54 x 2.799 mm, 22 faces, 0 solids (baked)
FEATURE [Part::Feature] Part__Feature676  label="COMPOUND100"
  shape: bbox 2.54 x 2.54 x 2.799 mm, 23 faces, 0 solids (baked)
FEATURE [Part::Feature] Part__Feature677  label="COMPOUND101"
  shape: bbox 2.54 x 2.54 x 2.799 mm, 22 faces, 0 solids (baked)
FEATURE [Part::Feature] Part__Feature678  label="COMPOUND102"
  shape: bbox 2.54 x 2.54 x 2.799 mm, 22 faces, 0 solids (baked)
FEATURE [Part::Feature] Part__Feature679  label="COMPOUND103"
  shape: bbox 2.54 x 2.54 x 2.799 mm, 23 faces, 0 solids (baked)
FEATURE [App::Part] COMPOUND014  label="COMPOUND104"
  Group = -> [Part__Feature674,Part__Feature675,Part__Feature676,Part__Feature677,Part__Feature678,Part__Feature679]
  Origin = -> Origin069
FEATURE [Part::Feature] Part__Feature680  label="COMPOUND105"
  shape: bbox 0.6304 x 0.63 x 12.7 mm, 14 faces (baked)
FEATURE [Part::Feature] Part__Feature681  label="COMPOUND106"
  shape: bbox 0.6304 x 0.63 x 12.7 mm, 14 faces (baked)
FEATURE [Part::Feature] Part__Feature682  label="COMPOUND107"
  shape: bbox 0.6304 x 0.63 x 12.7 mm, 14 faces (baked)
FEATURE [Part::Feature] Part__Feature683  label="COMPOUND108"
  shape: bbox 0.6304 x 0.63 x 12.7 mm, 14 faces (baked)
FEATURE [Part::Feature] Part__Feature684  label="COMPOUND109"
  shape: bbox 0.6304 x 0.63 x 12.7 mm, 14 faces (baked)
FEATURE [Part::Feature] Part__Feature685  label="COMPOUND110"
  shape: bbox 0.6304 x 0.63 x 12.7 mm, 14 faces (baked)
FEATURE [App::Part] COMPOUND015  label="COMPOUND111"
  Group = -> [Part__Feature680,Part__Feature681,Part__Feature682,Part__Feature683,Part__Feature684,Part__Feature685]
  Origin = -> Origin070
FEATURE [App::Part] Pin_Header_1x6_TH_Pitch_2_54mm_v1_Mirror_003  label="Pin Header 1x6 TH Pitch 2.54mm v1(Mirror)003"
  Group = -> [COMPOUND014,COMPOUND015]
  Origin = -> Origin068
  Placement = pos=(29.21,7.62,-0.814) rot=(0,0,1;3.14159rad)
FEATURE [Part::Feature] Part__Feature716  label="PTS810 SJK 250 SMTR LFS v1"
  Placement = pos=(12.85,-0.068585,1.06859) rot=(1,0,0;1.5708rad)
  shape: bbox 4.2 x 3.2 x 2 mm, 27 faces (baked)
FEATURE [Part::Feature] Part__Feature717  label="PTS810 SJK 250 SMTR LFS v002"
  Placement = pos=(12.85,-0.068585,1.06859) rot=(1,0,0;1.5708rad)
  shape: bbox 3.181 x 2.381 x 1.2 mm, 10 faces (baked)
FEATURE [App::Part] PTS810_SJK_250_SMTR_LFS_v1  label="PTS810 SJK 250 SMTR LFS v007"
  Group = -> [Part__Feature716,Part__Feature717]
  Origin = -> Origin075
FEATURE [Part::Feature] Part__Feature722  label="COMPOUND136"
  shape: bbox 60.96 x 17.78 x 1.63 mm, 71 faces (baked)
FEATURE [App::Part] COMPOUND020  label="COMPOUND159"
  Group = -> [Part__Feature722]
  Origin = -> Origin076
FEATURE [Part::Sphere] Sphere  label="Ball"
  Angle1 = -90
  Angle2 = 90
  Angle3 = 360
  AttacherType = Attacher::AttachEngine3D
  Placement = pos=(-88,0,-21) rot=(0,1,0;1.5708rad)
  Radius = 21
FEATURE [Sketcher::SketchObject] Sketch065
  FullyConstrained = true
  MapMode = 5
  Support = -> [XY_Plane226]
  sketch-geometry (12):
    g0: LineSegment StartX=101.78 StartY=40.22 StartZ=0 EndX=101.78 EndY=32.22 EndZ=0
    g1: LineSegment StartX=-66.22 StartY=32.22 StartZ=0 EndX=-66.22 EndY=40.22 EndZ=0
    g2: LineSegment StartX=-66.22 StartY=32.22 StartZ=0 EndX=7.78 EndY=32.22 EndZ=0
    g3: LineSegment StartX=7.78 StartY=32.22 StartZ=0 EndX=7.78 EndY=0 EndZ=0
    g4: LineSegment StartX=7.78 StartY=0 StartZ=0 EndX=27.78 EndY=0 EndZ=0
    g5: LineSegment StartX=27.78 StartY=0 StartZ=0 EndX=27.78 EndY=32.22 EndZ=0
    g6: LineSegment StartX=27.78 StartY=32.22 StartZ=0 EndX=101.78 EndY=32.22 EndZ=0
    g7: LineSegment StartX=-66.22 StartY=40.22 StartZ=0 EndX=0 EndY=40.22 EndZ=0
    g8: LineSegment StartX=101.78 StartY=40.22 StartZ=0 EndX=35.56 EndY=40.22 EndZ=0
    g9: LineSegment StartX=0 StartY=40.22 StartZ=0 EndX=0 EndY=44.52 EndZ=0
    g10: LineSegment StartX=0 StartY=44.52 StartZ=0 EndX=35.56 EndY=44.52 EndZ=0
    g11: LineSegment StartX=35.56 StartY=44.52 StartZ=0 EndX=35.56 EndY=40.22 EndZ=0
  constraints (36):
    c: Vertical(g0)
    c: Vertical(g1)
    c: DistanceY(g0,g0) = 8
    c: Coincident(g2,g1)
    c: Horizontal(g2)
    c: Vertical(g3)
    c: Coincident(g4,g3)
    c: Horizontal(g4)
    c: Coincident(g5,g4)
    c: Vertical(g5)
    c: Coincident(g6,g5)
    c: Coincident(g6,g0)
    c: Horizontal(g6)
    c: Equal(g2,g6)
    c: Horizontal(g2,g5)
    c: DistanceX(g1,g0) = 168
    c: Coincident(g7,g1)
    c: PointOnObject(g7,g-2)
    c: Horizontal(g7)
    c: Coincident(g8,g0)
    c: Horizontal(g8)
    c: DistanceX(g7,g8) = 35.56
    c: Equal(g1,g0)
    c: Coincident(g9,g7)
    c: Vertical(g9)
    c: Coincident(g10,g9)
    c: Horizontal(g10)
    c: Coincident(g11,g10)
    c: Coincident(g11,g8)
    c: Vertical(g11)
    c: DistanceY(g11,g11) = 4.3
    c: PointOnObject(g4,g-1)
    c: Coincident(g2,g3)
    c: DistanceX(g6,g6) = 74
    c: DistanceX(g1,g-1) = 66.22
    c: DistanceY(g-1,g1) = 32.22
FEATURE [PartDesign::Pad] Pad044
  Direction = (0,0,1)
  Length = 6
  Length2 = 10
  Profile = -> Sketch065
  ReferenceAxis = -> Sketch065 [N_Axis]
  Reversed = true
  Type = 0
FEATURE [Sketcher::SketchObject] Sketch074
  FullyConstrained = true
  MapMode = 5
  Support = -> [XY_Plane229]
  sketch-geometry (1):
    g0: Circle CenterX=0 CenterY=0 CenterZ=0 NormalX=0 NormalY=0 NormalZ=1 AngleXU=0 Radius=12
  constraints (2):
    c: Diameter(g0) = 24
    c: Coincident(g0,g-1)
FEATURE [PartDesign::Pad] Pad051
  Direction = (0,0,1)
  Length = 56.5
  Length2 = 10
  Profile = -> Sketch074
  ReferenceAxis = -> Sketch074 [N_Axis]
  Type = 0
FEATURE [Sketcher::SketchObject] Sketch075
  FullyConstrained = true
  MapMode = 5
  Support = -> [XY_Plane230]
  sketch-geometry (1):
    g0: Circle CenterX=0 CenterY=0 CenterZ=0 NormalX=0 NormalY=0 NormalZ=1 AngleXU=0 Radius=12
  constraints (2):
    c: Diameter(g0) = 24
    c: Coincident(g0,g-1)
FEATURE [PartDesign::Pad] Pad052
  Direction = (0,0,1)
  Length = 56.5
  Length2 = 10
  Profile = -> Sketch075
  ReferenceAxis = -> Sketch075 [N_Axis]
  Type = 0
FEATURE [Sketcher::SketchObject] Sketch081
  FullyConstrained = true
  MapMode = 5
  Support = -> [XY_Plane235]
  sketch-geometry (1):
    g0: Circle CenterX=0 CenterY=0 CenterZ=0 NormalX=0 NormalY=0 NormalZ=1 AngleXU=0 Radius=12
  constraints (2):
    c: Diameter(g0) = 24
    c: Coincident(g0,g-1)
FEATURE [PartDesign::Pad] Pad057
  Direction = (0,0,1)
  Length = 56.5
  Length2 = 10
  Profile = -> Sketch081
  ReferenceAxis = -> Sketch081 [N_Axis]
  Type = 0
FEATURE [Sketcher::SketchObject] Sketch082
  FullyConstrained = true
  MapMode = 5
  Placement = pos=(0,0,0) rot=(1,0,0;1.5708rad)
  Support = -> [XZ_Plane237]
  sketch-geometry (1):
    g0: Circle CenterX=0 CenterY=0 CenterZ=0 NormalX=0 NormalY=0 NormalZ=1 AngleXU=0 Radius=12
  constraints (2):
    c: Coincident(g0,g-1)
    c: Diameter(g0) = 24
FEATURE [PartDesign::Pad] Pad058
  Direction = (0,-1,-2e-16)
  Length = 50
  Length2 = 10
  Placement = pos=(0,0,0) rot=(1,0,0;1.5708rad)
  Profile = -> Sketch082
  ReferenceAxis = -> Sketch082 [N_Axis]
  Reversed = true
  Type = 0
FEATURE [Sketcher::SketchObject] Sketch083
  FullyConstrained = true
  MapMode = 5
  Placement = pos=(0,0,0) rot=(1,0,0;1.5708rad)
  Support = -> [XZ_Plane238]
  sketch-geometry (1):
    g0: Circle CenterX=0 CenterY=0 CenterZ=0 NormalX=0 NormalY=0 NormalZ=1 AngleXU=0 Radius=8
  constraints (2):
    c: Coincident(g0,g-1)
    c: Diameter(g0) = 16
FEATURE [PartDesign::Pad] Pad059
  Direction = (0,-1,-2e-16)
  Length = 50.5
  Length2 = 10
  Placement = pos=(0,0,0) rot=(1,0,0;1.5708rad)
  Profile = -> Sketch083
  ReferenceAxis = -> Sketch083 [N_Axis]
  Reversed = true
  Type = 0
FEATURE [Sketcher::SketchObject] Sketch084
  FullyConstrained = true
  MapMode = 5
  Placement = pos=(0,0,0) rot=(1,0,0;1.5708rad)
  Support = -> [XZ_Plane241]
  sketch-geometry (5):
    g0: Circle CenterX=0 CenterY=0 CenterZ=0 NormalX=0 NormalY=0 NormalZ=1 AngleXU=0 Radius=5
    g1: LineSegment StartX=-13 StartY=18 StartZ=0 EndX=13 EndY=18 EndZ=0
    g2: LineSegment StartX=-13 StartY=18 StartZ=0 EndX=-13 EndY=-3.6e-15 EndZ=0
    g3: LineSegment StartX=13 StartY=18 StartZ=0 EndX=13 EndY=-3.6e-15 EndZ=0
    g4: ArcOfCircle CenterX=0 CenterY=0 CenterZ=0 NormalX=0 NormalY=0 NormalZ=1 AngleXU=0 Radius=13 StartAngle=3.14159 EndAngle=6.28319
  constraints (13):
    c: Coincident(g0,g-1)
    c: Diameter(g0) = 10
    c: DistanceX(g1,g1) = 26
    c: Symmetric(g1,g1,g-2)
    c: DistanceY(g0,g1) = 18
    c: Coincident(g2,g1)
    c: PointOnObject(g2,g-1)
    c: Vertical(g2)
    c: Coincident(g3,g1)
    c: PointOnObject(g3,g-1)
    c: Coincident(g4,g0)
    c: Coincident(g4,g2)
    c: Coincident(g4,g3)
FEATURE [PartDesign::Pad] Pad062
  Direction = (0,-1,-2e-16)
  Length = 3
  Length2 = 10
  Placement = pos=(0,0,0) rot=(1,0,0;1.5708rad)
  Profile = -> Sketch084
  ReferenceAxis = -> Sketch084 [N_Axis]
  Type = 0
FEATURE [Sketcher::SketchObject] Sketch085
  ExternalGeometry = -> [Pad062]
  FullyConstrained = true
  MapMode = 5
  Placement = pos=(0,-3,0) rot=(1,0,0;1.5708rad)
  Support = -> [Pad062]
  sketch-geometry (4):
    g0: LineSegment StartX=-13 StartY=18 StartZ=0 EndX=-13 EndY=14 EndZ=0
    g1: LineSegment StartX=-13 StartY=14 StartZ=0 EndX=13 EndY=14 EndZ=0
    g2: LineSegment StartX=13 StartY=14 StartZ=0 EndX=13 EndY=18 EndZ=0
    g3: LineSegment StartX=13 StartY=18 StartZ=0 EndX=-13 EndY=18 EndZ=0
  constraints (10):
    c: Coincident(g0,g-3)
    c: Vertical(g0)
    c: Coincident(g1,g0)
    c: Horizontal(g1)
    c: Coincident(g2,g1)
    c: Coincident(g2,g-3)
    c: Vertical(g2)
    c: Coincident(g3,g2)
    c: Coincident(g3,g0)
    c: DistanceY(g0,g0) = 4
FEATURE [PartDesign::Pad] Pad063
  BaseFeature = -> Pad062
  Direction = (0,-1,-2e-16)
  Length = 30
  Length2 = 10
  Placement = pos=(0,0,0) rot=(1,0,0;1.5708rad)
  Profile = -> Sketch085
  ReferenceAxis = -> Sketch085 [N_Axis]
  Type = 0
FEATURE [Sketcher::SketchObject] Sketch086
  ExternalGeometry = -> [Pad063]
  FullyConstrained = true
  MapMode = 5
  Placement = pos=(0,4e-15,18) rot=(0,0,1;3.14159rad)
  Support = -> [Pad063]
  sketch-geometry (4):
    g0: Circle CenterX=-9 CenterY=7 CenterZ=0 NormalX=0 NormalY=0 NormalZ=1 AngleXU=0 Radius=2
    g1: Circle CenterX=9 CenterY=7 CenterZ=0 NormalX=0 NormalY=0 NormalZ=1 AngleXU=0 Radius=2
    g2: Circle CenterX=-9 CenterY=29 CenterZ=0 NormalX=0 NormalY=0 NormalZ=1 AngleXU=0 Radius=2
    g3: Circle CenterX=9 CenterY=29 CenterZ=0 NormalX=0 NormalY=0 NormalZ=1 AngleXU=0 Radius=2
  constraints (10):
    c: Diameter(g2) = 4
    c: Diameter(g3) = 4
    c: Diameter(g1) = 4
    c: Diameter(g0) = 4
    c: Symmetric(g2,g3,g-2)
    c: Symmetric(g0,g1,g-2)
    c: Vertical(g2,g0)
    c: DistanceX(g-4,g2) = 4
    c: DistanceY(g2,g-4) = 4
    c: DistanceY(g-4,g0) = 4
FEATURE [PartDesign::Pocket] Pocket029
  BaseFeature = -> Pad063
  Direction = (0,2e-16,-1)
  Length = 5
  Length2 = 5
  Placement = pos=(0,0,0) rot=(1,0,0;1.5708rad)
  Profile = -> Sketch086
  ReferenceAxis = -> Sketch086 [N_Axis]
  Type = 1
FEATURE [Sketcher::SketchObject] Sketch087
  FullyConstrained = true
  MapMode = 5
  Placement = pos=(0,0,0) rot=(-1,0,0;1.5708rad)
  Support = -> [Pocket029]
  sketch-geometry (1):
    g0: Circle CenterX=0 CenterY=9.5 CenterZ=0 NormalX=0 NormalY=0 NormalZ=1 AngleXU=0 Radius=1
  constraints (3):
    c: PointOnObject(g0,g-2)
    c: Diameter(g0) = 2
    c: DistanceY(g-1,g0) = 9.5
FEATURE [PartDesign::Pocket] Pocket030
  BaseFeature = -> Pocket029
  Direction = (0,-1,-2e-16)
  Length = 5
  Length2 = 5
  Placement = pos=(0,0,0) rot=(1,0,0;1.5708rad)
  Profile = -> Sketch087
  ReferenceAxis = -> Sketch087 [N_Axis]
  Type = 1
FEATURE [PartDesign::PolarPattern] PolarPattern012
  Angle = 360
  Axis = -> Sketch087 [N_Axis]
  BaseFeature = -> Pocket030
  Occurrences = 4
  Originals = -> [Pocket030]
  Placement = pos=(0,0,0) rot=(1,0,0;1.5708rad)
FEATURE [PartDesign::SubShapeBinder] Binder
  BindCopyOnChange = 0
  BindMode = 0
  ClaimChildren = false
  Context = -> Body [Binder.]
  Fuse = false
  MakeFace = true
  OffsetFill = false
  OffsetIntersection = false
  OffsetJoinType = 0
  OffsetOpenResult = false
  PartialLoad = false
  Relative = true
  Support = -> [Part003[Part005.Body038.Pocket029.Sketch086.]]
  _Version = 2
FEATURE [Sketcher::SketchObject] Sketch088
  FullyConstrained = true
  MapMode = 5
  Placement = pos=(0,0,0) rot=(1,0,0;1.5708rad)
  Support = -> [XZ_Plane242]
  sketch-geometry (5):
    g0: Circle CenterX=0 CenterY=0 CenterZ=0 NormalX=0 NormalY=0 NormalZ=1 AngleXU=0 Radius=6
    g1: LineSegment StartX=-13 StartY=18 StartZ=0 EndX=13 EndY=18 EndZ=0
    g2: LineSegment StartX=-13 StartY=18 StartZ=0 EndX=-13 EndY=0 EndZ=0
    g3: LineSegment StartX=13 StartY=18 StartZ=0 EndX=13 EndY=-3.6e-15 EndZ=0
    g4: ArcOfCircle CenterX=0 CenterY=0 CenterZ=0 NormalX=0 NormalY=0 NormalZ=1 AngleXU=0 Radius=13 StartAngle=3.14159 EndAngle=6.28319
  constraints (13):
    c: Coincident(g0,g-1)
    c: Diameter(g0) = 12
    c: DistanceX(g1,g1) = 26
    c: Symmetric(g1,g1,g-2)
    c: DistanceY(g0,g1) = 18
    c: Coincident(g2,g1)
    c: PointOnObject(g2,g-1)
    c: Vertical(g2)
    c: Coincident(g3,g1)
    c: PointOnObject(g3,g-1)
    c: Coincident(g4,g0)
    c: Coincident(g4,g2)
    c: Coincident(g4,g3)
FEATURE [PartDesign::Pad] Pad064
  Direction = (0,-1,-2e-16)
  Length = 3
  Length2 = 10
  Placement = pos=(0,0,0) rot=(1,0,0;1.5708rad)
  Profile = -> Sketch088
  ReferenceAxis = -> Sketch088 [N_Axis]
  Type = 0
FEATURE [Sketcher::SketchObject] Sketch089
  ExternalGeometry = -> [Pad064]
  FullyConstrained = true
  MapMode = 5
  Placement = pos=(0,-3,0) rot=(1,0,0;1.5708rad)
  Support = -> [Pad064]
  sketch-geometry (4):
    g0: LineSegment StartX=-13 StartY=18 StartZ=0 EndX=-13 EndY=14 EndZ=0
    g1: LineSegment StartX=-13 StartY=14 StartZ=0 EndX=13 EndY=14 EndZ=0
    g2: LineSegment StartX=13 StartY=14 StartZ=0 EndX=13 EndY=18 EndZ=0
    g3: LineSegment StartX=13 StartY=18 StartZ=0 EndX=-13 EndY=18 EndZ=0
  constraints (10):
    c: Coincident(g0,g-3)
    c: Vertical(g0)
    c: Coincident(g1,g0)
    c: Horizontal(g1)
    c: Coincident(g2,g1)
    c: Coincident(g2,g-3)
    c: Vertical(g2)
    c: Coincident(g3,g2)
    c: Coincident(g3,g0)
    c: DistanceY(g0,g0) = 4
FEATURE [PartDesign::Pad] Pad065
  BaseFeature = -> Pad064
  Direction = (0,-1,-2e-16)
  Length = 30
  Length2 = 10
  Placement = pos=(0,0,0) rot=(1,0,0;1.5708rad)
  Profile = -> Sketch089
  ReferenceAxis = -> Sketch089 [N_Axis]
  Type = 0
FEATURE [Sketcher::SketchObject] Sketch090
  ExternalGeometry = -> [Pad065]
  FullyConstrained = true
  MapMode = 5
  Placement = pos=(0,4e-15,18) rot=(0,0,1;3.14159rad)
  Support = -> [Pad065]
  sketch-geometry (4):
    g0: Circle CenterX=-9 CenterY=7 CenterZ=0 NormalX=0 NormalY=0 NormalZ=1 AngleXU=0 Radius=2
    g1: Circle CenterX=9 CenterY=7 CenterZ=0 NormalX=0 NormalY=0 NormalZ=1 AngleXU=0 Radius=2
    g2: Circle CenterX=-9 CenterY=29 CenterZ=0 NormalX=0 NormalY=0 NormalZ=1 AngleXU=0 Radius=2
    g3: Circle CenterX=9 CenterY=29 CenterZ=0 NormalX=0 NormalY=0 NormalZ=1 AngleXU=0 Radius=2
  constraints (10):
    c: Diameter(g2) = 4
    c: Diameter(g3) = 4
    c: Diameter(g1) = 4
    c: Diameter(g0) = 4
    c: Symmetric(g2,g3,g-2)
    c: Symmetric(g0,g1,g-2)
    c: Vertical(g2,g0)
    c: DistanceX(g-4,g2) = 4
    c: DistanceY(g2,g-4) = 4
    c: DistanceY(g-4,g0) = 4
FEATURE [PartDesign::Pocket] Pocket032
  BaseFeature = -> Pad065
  Direction = (0,2e-16,-1)
  Length = 5
  Length2 = 5
  Placement = pos=(0,0,0) rot=(1,0,0;1.5708rad)
  Profile = -> Sketch090
  ReferenceAxis = -> Sketch090 [N_Axis]
  Type = 1
FEATURE [Sketcher::SketchObject] Sketch091
  FullyConstrained = true
  MapMode = 5
  Placement = pos=(0,0,0) rot=(-1,0,0;1.5708rad)
  Support = -> [Pocket032]
  sketch-geometry (1):
    g0: Circle CenterX=0 CenterY=9.5 CenterZ=0 NormalX=0 NormalY=0 NormalZ=1 AngleXU=0 Radius=1
  constraints (3):
    c: PointOnObject(g0,g-2)
    c: Diameter(g0) = 2
    c: DistanceY(g-1,g0) = 9.5
FEATURE [PartDesign::Pocket] Pocket033
  BaseFeature = -> Pocket032
  Direction = (0,-1,-2e-16)
  Length = 5
  Length2 = 5
  Placement = pos=(0,0,0) rot=(1,0,0;1.5708rad)
  Profile = -> Sketch091
  ReferenceAxis = -> Sketch091 [N_Axis]
  Type = 1
FEATURE [PartDesign::PolarPattern] PolarPattern013
  Angle = 360
  Axis = -> Sketch091 [N_Axis]
  BaseFeature = -> Pocket033
  Occurrences = 4
  Originals = -> [Pocket033]
  Placement = pos=(0,0,0) rot=(1,0,0;1.5708rad)
FEATURE [PartDesign::Body] Body039  label="Moteur support 2"
  Group = -> [Sketch088,Pad064,Sketch089,Pad065,Sketch090,Pocket032,Sketch091,Pocket033,PolarPattern013]
  Origin = -> Origin242
  Placement = pos=(43.5918,62.2556,-8) rot=(0,0,-1;0.610865rad)
  Tip = -> PolarPattern013
FEATURE [Sketcher::SketchObject] Sketch092
  FullyConstrained = true
  MapMode = 5
  Placement = pos=(0,0,0) rot=(1,0,0;1.5708rad)
  Support = -> [XZ_Plane243]
  sketch-geometry (5):
    g0: Circle CenterX=0 CenterY=0 CenterZ=0 NormalX=0 NormalY=0 NormalZ=1 AngleXU=0 Radius=6
    g1: LineSegment StartX=-13 StartY=18 StartZ=0 EndX=13 EndY=18 EndZ=0
    g2: LineSegment StartX=-13 StartY=18 StartZ=0 EndX=-13 EndY=0 EndZ=0
    g3: LineSegment StartX=13 StartY=18 StartZ=0 EndX=13 EndY=-3.6e-15 EndZ=0
    g4: ArcOfCircle CenterX=0 CenterY=0 CenterZ=0 NormalX=0 NormalY=0 NormalZ=1 AngleXU=0 Radius=13 StartAngle=3.14159 EndAngle=6.28319
  constraints (13):
    c: Coincident(g0,g-1)
    c: Diameter(g0) = 12
    c: DistanceX(g1,g1) = 26
    c: Symmetric(g1,g1,g-2)
    c: DistanceY(g0,g1) = 18
    c: Coincident(g2,g1)
    c: PointOnObject(g2,g-1)
    c: Vertical(g2)
    c: Coincident(g3,g1)
    c: PointOnObject(g3,g-1)
    c: Coincident(g4,g0)
    c: Coincident(g4,g2)
    c: Coincident(g4,g3)
FEATURE [PartDesign::Pad] Pad066
  Direction = (0,-1,-2e-16)
  Length = 3
  Length2 = 10
  Placement = pos=(0,0,0) rot=(1,0,0;1.5708rad)
  Profile = -> Sketch092
  ReferenceAxis = -> Sketch092 [N_Axis]
  Type = 0
FEATURE [Sketcher::SketchObject] Sketch093
  ExternalGeometry = -> [Pad066]
  FullyConstrained = true
  MapMode = 5
  Placement = pos=(0,-3,0) rot=(1,0,0;1.5708rad)
  Support = -> [Pad066]
  sketch-geometry (4):
    g0: LineSegment StartX=-13 StartY=18 StartZ=0 EndX=-13 EndY=14 EndZ=0
    g1: LineSegment StartX=-13 StartY=14 StartZ=0 EndX=13 EndY=14 EndZ=0
    g2: LineSegment StartX=13 StartY=14 StartZ=0 EndX=13 EndY=18 EndZ=0
    g3: LineSegment StartX=13 StartY=18 StartZ=0 EndX=-13 EndY=18 EndZ=0
  constraints (10):
    c: Coincident(g0,g-3)
    c: Vertical(g0)
    c: Coincident(g1,g0)
    c: Horizontal(g1)
    c: Coincident(g2,g1)
    c: Coincident(g2,g-3)
    c: Vertical(g2)
    c: Coincident(g3,g2)
    c: Coincident(g3,g0)
    c: DistanceY(g0,g0) = 4
FEATURE [PartDesign::Pad] Pad067
  BaseFeature = -> Pad066
  Direction = (0,-1,-2e-16)
  Length = 30
  Length2 = 10
  Placement = pos=(0,0,0) rot=(1,0,0;1.5708rad)
  Profile = -> Sketch093
  ReferenceAxis = -> Sketch093 [N_Axis]
  Type = 0
FEATURE [Sketcher::SketchObject] Sketch094
  ExternalGeometry = -> [Pad067]
  FullyConstrained = true
  MapMode = 5
  Placement = pos=(0,4e-15,18) rot=(0,0,1;3.14159rad)
  Support = -> [Pad067]
  sketch-geometry (4):
    g0: Circle CenterX=-9 CenterY=7 CenterZ=0 NormalX=0 NormalY=0 NormalZ=1 AngleXU=0 Radius=2
    g1: Circle CenterX=9 CenterY=7 CenterZ=0 NormalX=0 NormalY=0 NormalZ=1 AngleXU=0 Radius=2
    g2: Circle CenterX=-9 CenterY=29 CenterZ=0 NormalX=0 NormalY=0 NormalZ=1 AngleXU=0 Radius=2
    g3: Circle CenterX=9 CenterY=29 CenterZ=0 NormalX=0 NormalY=0 NormalZ=1 AngleXU=0 Radius=2
  constraints (10):
    c: Diameter(g2) = 4
    c: Diameter(g3) = 4
    c: Diameter(g1) = 4
    c: Diameter(g0) = 4
    c: Symmetric(g2,g3,g-2)
    c: Symmetric(g0,g1,g-2)
    c: Vertical(g2,g0)
    c: DistanceX(g-4,g2) = 4
    c: DistanceY(g2,g-4) = 4
    c: DistanceY(g-4,g0) = 4
FEATURE [PartDesign::Pocket] Pocket034
  BaseFeature = -> Pad067
  Direction = (0,2e-16,-1)
  Length = 5
  Length2 = 5
  Placement = pos=(0,0,0) rot=(1,0,0;1.5708rad)
  Profile = -> Sketch094
  ReferenceAxis = -> Sketch094 [N_Axis]
  Type = 1
FEATURE [Sketcher::SketchObject] Sketch095
  FullyConstrained = true
  MapMode = 5
  Placement = pos=(0,0,0) rot=(-1,0,0;1.5708rad)
  Support = -> [Pocket034]
  sketch-geometry (1):
    g0: Circle CenterX=0 CenterY=9.5 CenterZ=0 NormalX=0 NormalY=0 NormalZ=1 AngleXU=0 Radius=1
  constraints (3):
    c: PointOnObject(g0,g-2)
    c: Diameter(g0) = 2
    c: DistanceY(g-1,g0) = 9.5
FEATURE [PartDesign::Pocket] Pocket035
  BaseFeature = -> Pocket034
  Direction = (0,-1,-2e-16)
  Length = 5
  Length2 = 5
  Placement = pos=(0,0,0) rot=(1,0,0;1.5708rad)
  Profile = -> Sketch095
  ReferenceAxis = -> Sketch095 [N_Axis]
  Type = 1
FEATURE [PartDesign::PolarPattern] PolarPattern014
  Angle = 360
  Axis = -> Sketch095 [N_Axis]
  BaseFeature = -> Pocket035
  Occurrences = 4
  Originals = -> [Pocket035]
  Placement = pos=(0,0,0) rot=(1,0,0;1.5708rad)
FEATURE [PartDesign::Body] Body040  label="Moteur support 3"
  Group = -> [Sketch092,Pad066,Sketch093,Pad067,Sketch094,Pocket034,Sketch095,Pocket035,PolarPattern014]
  Origin = -> Origin243
  Placement = pos=(43.5918,-62.2556,-8) rot=(0,0,1;3.75246rad)
  Tip = -> PolarPattern014
FEATURE [Sketcher::SketchObject] Sketch096
  FullyConstrained = true
  MapMode = 5
  Placement = pos=(0,0,0) rot=(1,0,0;1.5708rad)
  Support = -> [XZ_Plane244]
  sketch-geometry (5):
    g0: Circle CenterX=0 CenterY=0 CenterZ=0 NormalX=0 NormalY=0 NormalZ=1 AngleXU=0 Radius=6
    g1: LineSegment StartX=-13 StartY=18 StartZ=0 EndX=13 EndY=18 EndZ=0
    g2: LineSegment StartX=-13 StartY=18 StartZ=0 EndX=-13 EndY=0 EndZ=0
    g3: LineSegment StartX=13 StartY=18 StartZ=0 EndX=13 EndY=-3.6e-15 EndZ=0
    g4: ArcOfCircle CenterX=0 CenterY=0 CenterZ=0 NormalX=0 NormalY=0 NormalZ=1 AngleXU=0 Radius=13 StartAngle=3.14159 EndAngle=6.28319
  constraints (13):
    c: Coincident(g0,g-1)
    c: Diameter(g0) = 12
    c: DistanceX(g1,g1) = 26
    c: Symmetric(g1,g1,g-2)
    c: DistanceY(g0,g1) = 18
    c: Coincident(g2,g1)
    c: PointOnObject(g2,g-1)
    c: Vertical(g2)
    c: Coincident(g3,g1)
    c: PointOnObject(g3,g-1)
    c: Coincident(g4,g0)
    c: Coincident(g4,g2)
    c: Coincident(g4,g3)
FEATURE [PartDesign::Pad] Pad068
  Direction = (0,-1,-2e-16)
  Length = 3
  Length2 = 10
  Placement = pos=(0,0,0) rot=(1,0,0;1.5708rad)
  Profile = -> Sketch096
  ReferenceAxis = -> Sketch096 [N_Axis]
  Type = 0
FEATURE [Sketcher::SketchObject] Sketch097
  ExternalGeometry = -> [Pad068]
  FullyConstrained = true
  MapMode = 5
  Placement = pos=(0,-3,0) rot=(1,0,0;1.5708rad)
  Support = -> [Pad068]
  sketch-geometry (4):
    g0: LineSegment StartX=-13 StartY=18 StartZ=0 EndX=-13 EndY=14 EndZ=0
    g1: LineSegment StartX=-13 StartY=14 StartZ=0 EndX=13 EndY=14 EndZ=0
    g2: LineSegment StartX=13 StartY=14 StartZ=0 EndX=13 EndY=18 EndZ=0
    g3: LineSegment StartX=13 StartY=18 StartZ=0 EndX=-13 EndY=18 EndZ=0
  constraints (10):
    c: Coincident(g0,g-3)
    c: Vertical(g0)
    c: Coincident(g1,g0)
    c: Horizontal(g1)
    c: Coincident(g2,g1)
    c: Coincident(g2,g-3)
    c: Vertical(g2)
    c: Coincident(g3,g2)
    c: Coincident(g3,g0)
    c: DistanceY(g0,g0) = 4
FEATURE [PartDesign::Pad] Pad069
  BaseFeature = -> Pad068
  Direction = (0,-1,-2e-16)
  Length = 30
  Length2 = 10
  Placement = pos=(0,0,0) rot=(1,0,0;1.5708rad)
  Profile = -> Sketch097
  ReferenceAxis = -> Sketch097 [N_Axis]
  Type = 0
FEATURE [Sketcher::SketchObject] Sketch098
  ExternalGeometry = -> [Pad069]
  FullyConstrained = true
  MapMode = 5
  Placement = pos=(0,4e-15,18) rot=(0,0,1;3.14159rad)
  Support = -> [Pad069]
  sketch-geometry (4):
    g0: Circle CenterX=-9 CenterY=7 CenterZ=0 NormalX=0 NormalY=0 NormalZ=1 AngleXU=0 Radius=2
    g1: Circle CenterX=9 CenterY=7 CenterZ=0 NormalX=0 NormalY=0 NormalZ=1 AngleXU=0 Radius=2
    g2: Circle CenterX=-9 CenterY=29 CenterZ=0 NormalX=0 NormalY=0 NormalZ=1 AngleXU=0 Radius=2
    g3: Circle CenterX=9 CenterY=29 CenterZ=0 NormalX=0 NormalY=0 NormalZ=1 AngleXU=0 Radius=2
  constraints (10):
    c: Diameter(g2) = 4
    c: Diameter(g3) = 4
    c: Diameter(g1) = 4
    c: Diameter(g0) = 4
    c: Symmetric(g2,g3,g-2)
    c: Symmetric(g0,g1,g-2)
    c: Vertical(g2,g0)
    c: DistanceX(g-4,g2) = 4
    c: DistanceY(g2,g-4) = 4
    c: DistanceY(g-4,g0) = 4
FEATURE [PartDesign::Pocket] Pocket036
  BaseFeature = -> Pad069
  Direction = (0,2e-16,-1)
  Length = 5
  Length2 = 5
  Placement = pos=(0,0,0) rot=(1,0,0;1.5708rad)
  Profile = -> Sketch098
  ReferenceAxis = -> Sketch098 [N_Axis]
  Type = 1
FEATURE [Sketcher::SketchObject] Sketch099
  FullyConstrained = true
  MapMode = 5
  Placement = pos=(0,0,0) rot=(-1,0,0;1.5708rad)
  Support = -> [Pocket036]
  sketch-geometry (1):
    g0: Circle CenterX=0 CenterY=9.5 CenterZ=0 NormalX=0 NormalY=0 NormalZ=1 AngleXU=0 Radius=1
  constraints (3):
    c: PointOnObject(g0,g-2)
    c: Diameter(g0) = 2
    c: DistanceY(g-1,g0) = 9.5
FEATURE [PartDesign::Pocket] Pocket037
  BaseFeature = -> Pocket036
  Direction = (0,-1,-2e-16)
  Length = 5
  Length2 = 5
  Placement = pos=(0,0,0) rot=(1,0,0;1.5708rad)
  Profile = -> Sketch099
  ReferenceAxis = -> Sketch099 [N_Axis]
  Type = 1
FEATURE [PartDesign::PolarPattern] PolarPattern015
  Angle = 360
  Axis = -> Sketch099 [N_Axis]
  BaseFeature = -> Pocket037
  Occurrences = 4
  Originals = -> [Pocket037]
  Placement = pos=(0,0,0) rot=(1,0,0;1.5708rad)
FEATURE [PartDesign::Body] Body041  label="Moteur support 4"
  Group = -> [Sketch096,Pad068,Sketch097,Pad069,Sketch098,Pocket036,Sketch099,Pocket037,PolarPattern015]
  Origin = -> Origin244
  Placement = pos=(-43.5918,-62.2556,-8) rot=(0,0,1;2.53073rad)
  Tip = -> PolarPattern015
FEATURE [PartDesign::SubShapeBinder] Binder005
  BindCopyOnChange = 0
  BindMode = 0
  ClaimChildren = false
  Context = -> Body [Binder005.]
  Fuse = false
  MakeFace = true
  OffsetFill = false
  OffsetIntersection = false
  OffsetJoinType = 0
  OffsetOpenResult = false
  PartialLoad = false
  Relative = true
  Support = -> [Part003[Part006.Body039.Pocket032.Sketch090.]]
  _Version = 2
FEATURE [PartDesign::Pocket] Pocket031
  BaseFeature = -> Pocket019
  Direction = (0,-2e-16,-1)
  Length = 5
  Length2 = 5
  Profile = -> Binder
  Reversed = true
  Type = 1
FEATURE [PartDesign::Pocket] Pocket038
  BaseFeature = -> Pocket031
  Direction = (-2e-16,0,-1)
  Length = 5
  Length2 = 5
  Profile = -> Binder005
  Reversed = true
  Type = 1
FEATURE [PartDesign::SubShapeBinder] Binder006
  BindCopyOnChange = 0
  BindMode = 0
  ClaimChildren = false
  Context = -> Body [Binder006.]
  Fuse = false
  MakeFace = true
  OffsetFill = false
  OffsetIntersection = false
  OffsetJoinType = 0
  OffsetOpenResult = false
  PartialLoad = false
  Relative = true
  Support = -> [Part003[Part007.Body040.Pocket034.Sketch094.]]
  _Version = 2
FEATURE [PartDesign::Pocket] Pocket039
  BaseFeature = -> Pocket038
  Direction = (0,2e-16,-1)
  Length = 5
  Length2 = 5
  Profile = -> Binder006
  Reversed = true
  Type = 1
FEATURE [PartDesign::SubShapeBinder] Binder007
  BindCopyOnChange = 0
  BindMode = 0
  ClaimChildren = false
  Context = -> Body [Binder007.]
  Fuse = false
  MakeFace = true
  OffsetFill = false
  OffsetIntersection = false
  OffsetJoinType = 0
  OffsetOpenResult = false
  PartialLoad = false
  Relative = true
  Support = -> [Part003[Part008.Body041.Pocket036.Sketch098.]]
  _Version = 2
FEATURE [PartDesign::Pocket] Pocket040
  BaseFeature = -> Pocket039
  Direction = (2e-16,0,-1)
  Length = 5
  Length2 = 5
  Profile = -> Binder007
  Reversed = true
  Type = 1
FEATURE [Sketcher::SketchObject] Sketch102
  FullyConstrained = true
  MapMode = 5
  Support = -> [XY_Plane248]
  sketch-geometry (1):
    g0: Circle CenterX=0 CenterY=0 CenterZ=0 NormalX=0 NormalY=0 NormalZ=1 AngleXU=0 Radius=85
  constraints (2):
    c: Coincident(g0,g-1)
    c: Diameter(g0) = 170
FEATURE [PartDesign::Pad] Pad070  label="Structural layer001"
  Direction = (0,0,1)
  Length = 3
  Length2 = 10
  Profile = -> Sketch102
  ReferenceAxis = -> Sketch102 [N_Axis]
  Type = 0
FEATURE [Sketcher::SketchObject] Sketch109
  FullyConstrained = true
  MapMode = 5
  Placement = pos=(0,0,0) rot=(0.57735,0.57735,0.57735;2.0944rad)
  Support = -> [YZ_Plane251]
  sketch-geometry (4):
    g0: LineSegment StartX=-40 StartY=7 StartZ=0 EndX=40 EndY=7 EndZ=0
    g1: LineSegment StartX=40 StartY=7 StartZ=0 EndX=40 EndY=-7 EndZ=0
    g2: LineSegment StartX=40 StartY=-7 StartZ=0 EndX=-40 EndY=-7 EndZ=0
    g3: LineSegment StartX=-40 StartY=-7 StartZ=0 EndX=-40 EndY=7 EndZ=0
  constraints (10):
    c: Coincident(g0,g1)
    c: Coincident(g1,g2)
    c: Coincident(g2,g3)
    c: Coincident(g3,g0)
    c: Horizontal(g2)
    c: Vertical(g1)
    c: Symmetric(g2,g0,g-1)
    c: Symmetric(g0,g0,g-2)
    c: DistanceX(g0,g0) = 80
    c: DistanceY(g1,g1) = 14
FEATURE [PartDesign::Pad] Pad076
  Direction = (1,-2e-16,3e-16)
  Length = 3
  Length2 = 10
  Placement = pos=(0,0,0) rot=(0.57735,0.57735,0.57735;2.0944rad)
  Profile = -> Sketch109
  ReferenceAxis = -> Sketch109 [N_Axis]
  Type = 0
FEATURE [Sketcher::SketchObject] Sketch121
  FullyConstrained = true
  MapMode = 5
  Placement = pos=(0,0,0) rot=(1,0,0;1.5708rad)
  Support = -> [XZ_Plane255]
  sketch-geometry (5):
    g0: Circle CenterX=0 CenterY=0 CenterZ=0 NormalX=0 NormalY=0 NormalZ=1 AngleXU=0 Radius=6
    g1: LineSegment StartX=-13 StartY=17 StartZ=0 EndX=13 EndY=17 EndZ=0
    g2: LineSegment StartX=-13 StartY=17 StartZ=0 EndX=-13 EndY=0 EndZ=0
    g3: LineSegment StartX=13 StartY=17 StartZ=0 EndX=13 EndY=-3.6e-15 EndZ=0
    g4: ArcOfCircle CenterX=0 CenterY=0 CenterZ=0 NormalX=0 NormalY=0 NormalZ=1 AngleXU=0 Radius=13 StartAngle=3.14159 EndAngle=6.28319
  constraints (13):
    c: Coincident(g0,g-1)
    c: Diameter(g0) = 12
    c: DistanceX(g1,g1) = 26
    c: Symmetric(g1,g1,g-2)
    c: DistanceY(g0,g1) = 17
    c: Coincident(g2,g1)
    c: PointOnObject(g2,g-1)
    c: Vertical(g2)
    c: Coincident(g3,g1)
    c: PointOnObject(g3,g-1)
    c: Coincident(g4,g0)
    c: Coincident(g4,g2)
    c: Coincident(g4,g3)
FEATURE [PartDesign::Pad] Pad085
  Direction = (0,-1,2e-16)
  Length = 3
  Length2 = 10
  Placement = pos=(0,0,0) rot=(1,0,0;1.5708rad)
  Profile = -> Sketch121
  ReferenceAxis = -> Sketch121 [N_Axis]
  Type = 0
FEATURE [Sketcher::SketchObject] Sketch122
  ExternalGeometry = -> [Pad085]
  FullyConstrained = true
  MapMode = 5
  Placement = pos=(0,-3,1.3e-15) rot=(1,0,0;1.5708rad)
  Support = -> [Pad085]
  sketch-geometry (4):
    g0: LineSegment StartX=-13 StartY=17 StartZ=0 EndX=-13 EndY=14 EndZ=0
    g1: LineSegment StartX=-13 StartY=14 StartZ=0 EndX=13 EndY=14 EndZ=0
    g2: LineSegment StartX=13 StartY=14 StartZ=0 EndX=13 EndY=17 EndZ=0
    g3: LineSegment StartX=13 StartY=17 StartZ=0 EndX=-13 EndY=17 EndZ=0
  constraints (10):
    c: Coincident(g0,g-3)
    c: Vertical(g0)
    c: Coincident(g1,g0)
    c: Horizontal(g1)
    c: Coincident(g2,g1)
    c: Coincident(g2,g-3)
    c: Vertical(g2)
    c: Coincident(g3,g2)
    c: Coincident(g3,g0)
    c: DistanceY(g0,g0) = 3
FEATURE [PartDesign::Pad] Pad086
  BaseFeature = -> Pad085
  Direction = (0,-1,2e-16)
  Length = 30
  Length2 = 10
  Placement = pos=(0,0,0) rot=(1,0,0;1.5708rad)
  Profile = -> Sketch122
  ReferenceAxis = -> Sketch122 [N_Axis]
  Type = 0
FEATURE [Sketcher::SketchObject] Sketch123
  ExternalGeometry = -> [Pad086]
  FullyConstrained = true
  MapMode = 5
  Placement = pos=(2.4e-15,1.13e-14,17) rot=(0,0,1;3.14159rad)
  Support = -> [Pad086]
  sketch-geometry (4):
    g0: Circle CenterX=-9 CenterY=7 CenterZ=0 NormalX=0 NormalY=0 NormalZ=1 AngleXU=0 Radius=2
    g1: Circle CenterX=9 CenterY=7 CenterZ=0 NormalX=0 NormalY=0 NormalZ=1 AngleXU=0 Radius=2
    g2: Circle CenterX=-9 CenterY=29 CenterZ=0 NormalX=0 NormalY=0 NormalZ=1 AngleXU=0 Radius=2
    g3: Circle CenterX=9 CenterY=29 CenterZ=0 NormalX=0 NormalY=0 NormalZ=1 AngleXU=0 Radius=2
  constraints (10):
    c: Diameter(g2) = 4
    c: Diameter(g3) = 4
    c: Diameter(g1) = 4
    c: Diameter(g0) = 4
    c: Symmetric(g2,g3,g-2)
    c: Symmetric(g0,g1,g-2)
    c: Vertical(g2,g0)
    c: DistanceX(g-4,g2) = 4
    c: DistanceY(g2,g-4) = 4
    c: DistanceY(g-4,g0) = 4
FEATURE [PartDesign::Pocket] Pocket048
  BaseFeature = -> Pad086
  Direction = (-1e-16,-2e-16,-1)
  Length = 5
  Length2 = 5
  Placement = pos=(0,0,0) rot=(1,0,0;1.5708rad)
  Profile = -> Sketch123
  ReferenceAxis = -> Sketch123 [N_Axis]
  Type = 1
FEATURE [Sketcher::SketchObject] Sketch124
  FullyConstrained = true
  MapMode = 5
  Placement = pos=(0,0,0) rot=(-1,0,0;1.5708rad)
  Support = -> [Pocket048]
  sketch-geometry (1):
    g0: Circle CenterX=0 CenterY=9.5 CenterZ=0 NormalX=0 NormalY=0 NormalZ=1 AngleXU=0 Radius=1
  constraints (3):
    c: PointOnObject(g0,g-2)
    c: Diameter(g0) = 2
    c: DistanceY(g-1,g0) = 9.5
FEATURE [PartDesign::Pocket] Pocket049
  BaseFeature = -> Pocket048
  Direction = (0,-1,2e-16)
  Length = 5
  Length2 = 5
  Placement = pos=(0,0,0) rot=(1,0,0;1.5708rad)
  Profile = -> Sketch124
  ReferenceAxis = -> Sketch124 [N_Axis]
  Type = 1
FEATURE [PartDesign::PolarPattern] PolarPattern018
  Angle = 360
  Axis = -> Sketch124 [N_Axis]
  BaseFeature = -> Pocket049
  Occurrences = 4
  Originals = -> [Pocket049]
  Placement = pos=(0,0,0) rot=(1,0,0;1.5708rad)
FEATURE [PartDesign::SubShapeBinder] Binder008
  BindCopyOnChange = 0
  BindMode = 0
  ClaimChildren = false
  Context = -> Body [Binder008.]
  Fuse = false
  MakeFace = true
  OffsetFill = false
  OffsetIntersection = false
  OffsetJoinType = 0
  OffsetOpenResult = false
  PartialLoad = false
  Relative = true
  Support = -> [Part011[Body050.Pocket048.Sketch123.]]
  _Version = 2
FEATURE [PartDesign::Pocket] Pocket050
  BaseFeature = -> Pocket040
  Direction = (-4e-16,-6e-16,-1)
  Length = 5
  Length2 = 5
  Profile = -> Binder008
  Type = 1
FEATURE [PartDesign::SubShapeBinder] Binder010
  BindCopyOnChange = 0
  BindMode = 0
  ClaimChildren = false
  Context = -> Part015 [Body025.Binder010.]
  Fuse = false
  MakeFace = true
  OffsetFill = false
  OffsetIntersection = false
  OffsetJoinType = 0
  OffsetOpenResult = false
  PartialLoad = false
  Relative = true
  _Version = 2
FEATURE [PartDesign::Pocket] Pocket052
  BaseFeature = -> Pad044
  Direction = (0,0,-1)
  Length = 5
  Length2 = 5
  Profile = -> Binder010
  Type = 1
FEATURE [Sketcher::SketchObject] Sketch126
  FullyConstrained = false
  MapMode = 5
  Placement = pos=(0,0,2) rot=(0,0,1;0rad)
  sketch-geometry (8):
    g0: Circle CenterX=-65.799 CenterY=-46 CenterZ=0 NormalX=0 NormalY=0 NormalZ=1 AngleXU=0 Radius=1.5
    g1: Circle CenterX=-46 CenterY=-65.799 CenterZ=0 NormalX=0 NormalY=0 NormalZ=1 AngleXU=0 Radius=1.5
    g2: LineSegment StartX=103.375 StartY=103.375 StartZ=0 EndX=-110.971 EndY=-110.971 EndZ=0
    g3: LineSegment StartX=0 StartY=0 StartZ=0 EndX=106.113 EndY=-106.113 EndZ=0
    g4: Circle CenterX=25 CenterY=-75.9117 CenterZ=0 NormalX=0 NormalY=0 NormalZ=1 AngleXU=0 Radius=1.5
    g5: Circle CenterX=75.9117 CenterY=-25 CenterZ=0 NormalX=0 NormalY=0 NormalZ=1 AngleXU=0 Radius=1.5
    g6: Circle CenterX=65.799 CenterY=46 CenterZ=0 NormalX=0 NormalY=0 NormalZ=1 AngleXU=0 Radius=1.5
    g7: Circle CenterX=46 CenterY=65.799 CenterZ=0 NormalX=0 NormalY=0 NormalZ=1 AngleXU=0 Radius=1.5
  constraints (19):
    c: Diameter(g1) = 3
    c: Diameter(g0) = 3
    c: Angle(g2,g-1) = 2.35619
    c: Symmetric(g1,g0,g2)
    c: Distance(g1,g2) = 14
    c: Distance(g1,g-2) = 46
    c: PointOnObject(g-1,g2)
    c: Coincident(g3,g-1)
    c: Perpendicular(g2,g3)
    c: Diameter(g7) = 3
    c: Diameter(g6) = 3
    c: Diameter(g5) = 3
    c: Diameter(g4) = 3
    c: Symmetric(g4,g5,g3)
    c: Symmetric(g7,g6,g2)
    c: Distance(g4,g3) = 36
    c: Distance(g6,g2) = 14
    c: Distance(g4,g-2) = 25
    c: Distance(g7,g-2) = 46
FEATURE [PartDesign::Pocket] Pocket055
  BaseFeature = -> Pocket050
  Direction = (0,0,-1)
  Length = 50
  Length2 = 5
  Profile = -> Sketch126
  ReferenceAxis = -> Sketch126 [N_Axis]
  Type = 4
FEATURE [PartDesign::SubShapeBinder] Binder013
  BindCopyOnChange = 0
  BindMode = 0
  ClaimChildren = false
  Context = -> Part014 [Body044.Binder013.]
  Fuse = false
  MakeFace = true
  OffsetFill = false
  OffsetIntersection = false
  OffsetJoinType = 0
  OffsetOpenResult = false
  PartialLoad = false
  Relative = true
  Support = -> [Body[Pocket055.Sketch126.]]
  _Version = 2
FEATURE [PartDesign::Pocket] Pocket094
  BaseFeature = -> Pad070
  Direction = (0,0,-1)
  Length = 5
  Length2 = 5
  Profile = -> Binder013
  Type = 1
FEATURE [PartDesign::PolarPattern] PolarPattern021
  Angle = 70
  Axis = -> Sketch001 [N_Axis]
  BaseFeature = -> Pocket055
  Occurrences = 2
  Originals = -> [Pocket]
  Reversed = true
FEATURE [PartDesign::PolarPattern] PolarPattern022
  Angle = 360
  Axis = -> Sketch001 [N_Axis]
  BaseFeature = -> PolarPattern021
  Occurrences = 2
  Originals = -> [Pocket]
FEATURE [PartDesign::SubShapeBinder] Binder027
  BindCopyOnChange = 0
  BindMode = 0
  ClaimChildren = false
  Context = -> Part014 [Body044.Binder027.]
  Fuse = false
  MakeFace = true
  OffsetFill = false
  OffsetIntersection = false
  OffsetJoinType = 0
  OffsetOpenResult = false
  PartialLoad = false
  Relative = true
  Support = -> [Body[Pocket.Sketch001.]]
  _Version = 2
FEATURE [PartDesign::Pocket] Pocket096
  BaseFeature = -> Pocket094
  Direction = (0,0,-1)
  Length = 5
  Length2 = 5
  Profile = -> Binder027
  Type = 1
FEATURE [PartDesign::PolarPattern] PolarPattern023
  Angle = 110
  Axis = -> Z_Axis248
  BaseFeature = -> Pocket096
  Occurrences = 2
  Originals = -> [Pocket096]
FEATURE [PartDesign::PolarPattern] PolarPattern024
  Angle = 70
  Axis = -> Z_Axis248
  BaseFeature = -> PolarPattern023
  Occurrences = 2
  Originals = -> [Pocket096]
  Reversed = true
FEATURE [PartDesign::PolarPattern] PolarPattern025
  Angle = 180
  Axis = -> Z_Axis248
  BaseFeature = -> PolarPattern024
  Occurrences = 2
  Originals = -> [Pocket096]
FEATURE [PartDesign::SubShapeBinder] Binder028
  BindCopyOnChange = 0
  BindMode = 0
  ClaimChildren = false
  Context = -> Part014 [Body044.Binder028.]
  Fuse = false
  MakeFace = true
  OffsetFill = false
  OffsetIntersection = false
  OffsetJoinType = 0
  OffsetOpenResult = false
  PartialLoad = false
  Relative = true
  Support = -> [Body[Pocket004.Sketch015.]]
  _Version = 2
FEATURE [PartDesign::Pocket] Pocket097
  BaseFeature = -> PolarPattern025
  Direction = (0,0,-1)
  Length = 5
  Length2 = 5
  Profile = -> Binder028
  Type = 1
FEATURE [Sketcher::SketchObject] Sketch127
  FullyConstrained = true
  MapMode = 5
  Placement = pos=(0,0,0) rot=(1,0,0;1.5708rad)
  Support = -> [XZ_Plane256]
  sketch-geometry (8):
    g0: LineSegment StartX=-88 StartY=-1 StartZ=0 EndX=-79 EndY=-1 EndZ=0
    g1: LineSegment StartX=-79 StartY=-34 StartZ=0 EndX=-88 EndY=-34 EndZ=0
    g2: LineSegment StartX=-88 StartY=-34 StartZ=0 EndX=-88 EndY=-1 EndZ=0
    g3: LineSegment StartX=-79 StartY=-1 StartZ=0 EndX=-79 EndY=-3 EndZ=0
    g4: LineSegment StartX=-79 StartY=-3 StartZ=0 EndX=-86 EndY=-3 EndZ=0
    g5: LineSegment StartX=-86 StartY=-3 StartZ=0 EndX=-86 EndY=-32 EndZ=0
    g6: LineSegment StartX=-86 StartY=-32 StartZ=0 EndX=-79 EndY=-32 EndZ=0
    g7: LineSegment StartX=-79 StartY=-32 StartZ=0 EndX=-79 EndY=-34 EndZ=0
  constraints (24):
    c: Coincident(g1,g2)
    c: Coincident(g2,g0)
    c: Horizontal(g0)
    c: Horizontal(g1)
    c: Vertical(g2)
    c: DistanceY(g1,g0) = 33
    c: DistanceX(g1,g1) = 9
    c: DistanceX(g0,g-1) = 88
    c: DistanceY(g1,g-1) = 34
    c: Equal(g1,g0)
    c: Coincident(g3,g0)
    c: Vertical(g3)
    c: Coincident(g4,g3)
    c: Horizontal(g4)
    c: Coincident(g5,g4)
    c: Vertical(g5)
    c: Coincident(g6,g5)
    c: Horizontal(g6)
    c: Coincident(g7,g6)
    c: Coincident(g7,g1)
    c: Vertical(g7)
    c: Equal(g3,g7)
    c: DistanceY(g3,g3) = 2
    c: DistanceX(g0,g4) = 2
FEATURE [PartDesign::Revolution] Revolution002
  Angle = 70
  Axis = (1e-16,1e-16,1)
  Base = (0,0,0)
  Midplane = true
  Placement = pos=(0,0,0) rot=(1,0,0;1.5708rad)
  Profile = -> Sketch127
  ReferenceAxis = -> Z_Axis256
  Reversed = true
FEATURE [Sketcher::SketchObject] Sketch128
  FullyConstrained = true
  MapMode = 5
  Placement = pos=(0,0,0) rot=(1,0,0;1.5708rad)
  Support = -> [XZ_Plane257]
  sketch-geometry (8):
    g0: LineSegment StartX=-88 StartY=-1 StartZ=0 EndX=-79 EndY=-1 EndZ=0
    g1: LineSegment StartX=-79 StartY=-34 StartZ=0 EndX=-88 EndY=-34 EndZ=0
    g2: LineSegment StartX=-88 StartY=-34 StartZ=0 EndX=-88 EndY=-1 EndZ=0
    g3: LineSegment StartX=-79 StartY=-1 StartZ=0 EndX=-79 EndY=-3 EndZ=0
    g4: LineSegment StartX=-79 StartY=-3 StartZ=0 EndX=-86 EndY=-3 EndZ=0
    g5: LineSegment StartX=-86 StartY=-3 StartZ=0 EndX=-86 EndY=-32 EndZ=0
    g6: LineSegment StartX=-86 StartY=-32 StartZ=0 EndX=-79 EndY=-32 EndZ=0
    g7: LineSegment StartX=-79 StartY=-32 StartZ=0 EndX=-79 EndY=-34 EndZ=0
  constraints (24):
    c: Coincident(g1,g2)
    c: Coincident(g2,g0)
    c: Horizontal(g0)
    c: Horizontal(g1)
    c: Vertical(g2)
    c: DistanceY(g1,g0) = 33
    c: DistanceX(g1,g1) = 9
    c: DistanceX(g0,g-1) = 88
    c: DistanceY(g1,g-1) = 34
    c: Equal(g1,g0)
    c: Coincident(g3,g0)
    c: Vertical(g3)
    c: Coincident(g4,g3)
    c: Horizontal(g4)
    c: Coincident(g5,g4)
    c: Vertical(g5)
    c: Coincident(g6,g5)
    c: Horizontal(g6)
    c: Coincident(g7,g6)
    c: Coincident(g7,g1)
    c: Vertical(g7)
    c: Equal(g3,g7)
    c: DistanceY(g3,g3) = 2
    c: DistanceX(g0,g4) = 2
FEATURE [PartDesign::Revolution] Revolution003
  Angle = 30
  Axis = (1e-16,1e-16,1)
  Base = (0,0,0)
  Midplane = true
  Placement = pos=(0,0,0) rot=(1,0,0;1.5708rad)
  Profile = -> Sketch128
  ReferenceAxis = -> Z_Axis257
  Reversed = true
FEATURE [Part::Feature] Part__Feature1464  label="LD19_BASE"
  Placement = pos=(-9e-15,-8.62399,0) rot=(0,0,1;0rad)
  shape: bbox 53.95 x 46.29 x 3.551 mm, 34 faces (baked)
FEATURE [Part::Feature] Part__Feature1465  label="LD19_EMITTER"
  Placement = pos=(5.47382e-06,-8.59716,0) rot=(0,0,1;0rad)
  shape: bbox 39.74 x 39.74 x 11.25 mm, 29 faces (baked)
FEATURE [Part::Feature] Part__Feature1466  label="LD19_BODY"
  Placement = pos=(5.47382e-06,-8.59716,-2e-15) rot=(0,0,1;0rad)
  shape: bbox 38.52 x 38.52 x 18.7 mm, 15 faces (baked)
FEATURE [PartDesign::SubShapeBinder] Binder032
  BindCopyOnChange = 0
  BindMode = 0
  ClaimChildren = false
  Context = -> Body [Binder032.]
  Fuse = false
  MakeFace = true
  OffsetFill = false
  OffsetIntersection = false
  OffsetJoinType = 0
  OffsetOpenResult = false
  PartialLoad = false
  Relative = true
  Support = -> [LD19[Part__Feature1464.Edge77,Part__Feature1464.Edge78,Part__Feature1464.Edge73,Part__Feature1464.Edge74,Part__Feature1464.Edge75,Part__Feature1464.Edge76]]
  _Version = 2
FEATURE [PartDesign::Pocket] Pocket101
  BaseFeature = -> PolarPattern022
  Direction = (0,0,-1)
  Length = 5
  Length2 = 5
  Profile = -> Binder032
  Type = 1
FEATURE [Sketcher::SketchObject] Sketch130
  FullyConstrained = false
  MapMode = 5
  Support = -> [XY_Plane049]
  sketch-geometry (6):
    g0: ArcOfCircle CenterX=0 CenterY=0 CenterZ=0 NormalX=0 NormalY=0 NormalZ=1 AngleXU=0 Radius=77.5 StartAngle=4.97117 EndAngle=7.5952
    g1: LineSegment StartX=19.8431 StartY=-22.5 StartZ=0 EndX=19.8431 EndY=22.5 EndZ=0
    g2: ArcOfCircle CenterX=0 CenterY=0 CenterZ=0 NormalX=0 NormalY=0 NormalZ=1 AngleXU=0 Radius=30 StartAngle=5.43464 EndAngle=5.43512
    g3: ArcOfCircle CenterX=0 CenterY=0 CenterZ=0 NormalX=0 NormalY=0 NormalZ=1 AngleXU=0 Radius=30 StartAngle=0.848062 EndAngle=0.848549
    g4: LineSegment StartX=19.8322 StartY=-74.9195 StartZ=0 EndX=19.8322 EndY=-22.5097 EndZ=0
    g5: LineSegment StartX=19.8322 StartY=22.5097 StartZ=0 EndX=19.8322 EndY=74.9195 EndZ=0
  constraints (16):
    c: Coincident(g0,g-1)
    c: Symmetric(g1,g1,g-1)
    c: Diameter(g0) = 155
    c: DistanceY(g1,g1) = 45
    c: Coincident(g2,g0)
    c: Coincident(g2,g1)
    c: Coincident(g3,g0)
    c: Coincident(g3,g1)
    c: Diameter(g3) = 60
    c: Coincident(g4,g0)
    c: Coincident(g4,g2)
    c: Coincident(g5,g3)
    c: Coincident(g5,g0)
    c: Vertical(g0,g0)
    c: Vertical(g2,g3)
    c: Vertical(g4)
FEATURE [PartDesign::Pad] Pad088
  Direction = (0,0,1)
  Length = 2
  Length2 = 10
  Profile = -> Sketch130
  ReferenceAxis = -> Sketch130 [N_Axis]
  Type = 0
FEATURE [Sketcher::SketchObject] Sketch131
  FullyConstrained = true
  MapMode = 5
  Placement = pos=(0,0,0) rot=(1,0,0;1.5708rad)
  Support = -> [XZ_Plane259]
  sketch-geometry (4):
    g0: LineSegment StartX=-22 StartY=15 StartZ=0 EndX=22 EndY=15 EndZ=0
    g1: LineSegment StartX=22 StartY=15 StartZ=0 EndX=22 EndY=-15 EndZ=0
    g2: LineSegment StartX=22 StartY=-15 StartZ=0 EndX=-22 EndY=-15 EndZ=0
    g3: LineSegment StartX=-22 StartY=-15 StartZ=0 EndX=-22 EndY=15 EndZ=0
  constraints (10):
    c: Coincident(g0,g1)
    c: Coincident(g1,g2)
    c: Coincident(g2,g3)
    c: Coincident(g3,g0)
    c: Horizontal(g2)
    c: Vertical(g3)
    c: DistanceY(g1,g1) = 30
    c: Symmetric(g1,g0,g-1)
    c: Symmetric(g0,g0,g-2)
    c: DistanceX(g0,g0) = 44
FEATURE [PartDesign::SubShapeBinder] Binder034
  BindCopyOnChange = 0
  BindMode = 0
  ClaimChildren = false
  Context = -> Body [Binder034.]
  Fuse = false
  MakeFace = true
  OffsetFill = false
  OffsetIntersection = false
  OffsetJoinType = 0
  OffsetOpenResult = false
  PartialLoad = false
  Relative = true
  Support = -> [Part004[Body053.Pad089.Sketch131.]]
  _Version = 2
FEATURE [PartDesign::Pocket] Pocket103
  BaseFeature = -> Pocket101
  Direction = (-6e-16,-1e-15,-1)
  Length = 5
  Length2 = 5
  Profile = -> Binder034
  Reversed = true
  Type = 1
FEATURE [PartDesign::SubShapeBinder] Binder035
  BindCopyOnChange = 0
  BindMode = 0
  ClaimChildren = false
  Context = -> Part [Body024.Binder035.]
  Fuse = false
  MakeFace = true
  OffsetFill = false
  OffsetIntersection = false
  OffsetJoinType = 0
  OffsetOpenResult = false
  PartialLoad = false
  Relative = true
  Support = -> [Part004[Body053.Pad089.Sketch131.]]
  _Version = 2
FEATURE [PartDesign::Pocket] Pocket104
  BaseFeature = -> Pad088
  Direction = (2e-16,-1.1e-15,-1)
  Length = 5
  Length2 = 5
  Profile = -> Binder035
  Reversed = true
  Type = 1
FEATURE [PartDesign::Body] Body024  label="PCB board"
  Group = -> [Sketch130,Pad088,Binder035,Pocket104]
  Origin = -> Origin049
  Placement = pos=(0,0,16) rot=(0,0,1;0rad)
  Tip = -> Pocket104
FEATURE [Sketcher::SketchObject] Sketch133
  FullyConstrained = true
  MapMode = 5
  Placement = pos=(0,0,0) rot=(1,0,0;1.5708rad)
  Support = -> [XZ_Plane259]
  sketch-geometry (4):
    g0: LineSegment StartX=-21.5 StartY=14.5 StartZ=0 EndX=21.5 EndY=14.5 EndZ=0
    g1: LineSegment StartX=21.5 StartY=14.5 StartZ=0 EndX=21.5 EndY=-14.5 EndZ=0
    g2: LineSegment StartX=21.5 StartY=-14.5 StartZ=0 EndX=-21.5 EndY=-14.5 EndZ=0
    g3: LineSegment StartX=-21.5 StartY=-14.5 StartZ=0 EndX=-21.5 EndY=14.5 EndZ=0
  constraints (10):
    c: Coincident(g0,g1)
    c: Coincident(g1,g2)
    c: Coincident(g2,g3)
    c: Coincident(g3,g0)
    c: Horizontal(g2)
    c: Vertical(g1)
    c: Symmetric(g0,g0,g-2)
    c: Symmetric(g2,g0,g-1)
    c: DistanceX(g0,g0) = 43
    c: DistanceY(g1,g1) = 29
FEATURE [PartDesign::Pad] Pad089
  Direction = (0,-1,-2e-16)
  Length = 60
  Length2 = 10
  Placement = pos=(0,0,0) rot=(1,0,0;1.5708rad)
  Profile = -> Sketch133
  ReferenceAxis = -> Sketch133 [N_Axis]
  Type = 0
FEATURE [PartDesign::Fillet] Fillet
  Base = -> Pad089 [Edge7,Edge4,Edge10,Edge12,Edge2,Edge5,Edge1,Edge8,Edge3,Edge11,Edge9,Edge6]
  BaseFeature = -> Pad089
  Placement = pos=(0,0,0) rot=(1,0,0;1.5708rad)
  Radius = 2
  SupportTransform = false
  UseAllEdges = false
FEATURE [PartDesign::Body] Body053  label="Batterie"
  Group = -> [Sketch131,Sketch133,Pad089,Fillet]
  Origin = -> Origin259
  Placement = pos=(64,-2.9e-14,-36.5) rot=(0.57735,-0.57735,0.57735;4.18879rad)
  Tip = -> Fillet
FEATURE [App::Part] Part004  label="Powerpack"
  Group = -> [Body053]
  Origin = -> Origin037
  Placement = pos=(0,0,3) rot=(0,0,1;0rad)
FEATURE [PartDesign::SubShapeBinder] Binder038
  BindCopyOnChange = 0
  BindMode = 0
  ClaimChildren = false
  Context = -> Body [Binder038.]
  Fuse = false
  MakeFace = true
  OffsetFill = false
  OffsetIntersection = false
  OffsetJoinType = 0
  OffsetOpenResult = false
  PartialLoad = false
  Relative = true
  Support = -> [Part013[Body049.Pocket108.Sketch137.]]
  _Version = 2
FEATURE [PartDesign::Pocket] Pocket109
  BaseFeature = -> Pocket103
  Direction = (0,0,-1)
  Length = 5
  Length2 = 5
  Profile = -> Binder038
  Reversed = true
  Type = 1
FEATURE [Sketcher::SketchObject] Sketch138
  ExternalGeometry = -> [Pocket097]
  FullyConstrained = true
  MapMode = 5
  Placement = pos=(0,0,0) rot=(1,0,0;3.14159rad)
  Support = -> [Pocket097]
  sketch-geometry (3):
    g0: LineSegment StartX=7.63834 StartY=75.3298 StartZ=0 EndX=17.2106 EndY=49.0304 EndZ=0
    g1: LineSegment StartX=17.2106 StartY=49.0304 StartZ=0 EndX=49.0304 EndY=17.2106 EndZ=0
    g2: LineSegment StartX=49.0304 StartY=17.2106 StartZ=0 EndX=75.3298 EndY=7.63834 EndZ=0
  constraints (8):
    c: Coincident(g0,g-3)
    c: Coincident(g1,g0)
    c: Coincident(g2,g1)
    c: Coincident(g2,g-4)
    c: Distance(g1) = 45
    c: Equal(g0,g2)
    c: Angle(g0,g-3) = 2.18166
    c: Angle(g-4,g2) = 2.18166
FEATURE [Sketcher::SketchObject] Sketch193
  FullyConstrained = false
  MapMode = 5
  Placement = pos=(0,0,0) rot=(1,0,0;3.14159rad)
  sketch-geometry (6):
    g0: LineSegment StartX=7.63834 StartY=75.3298 StartZ=0 EndX=17.2106 EndY=49.0304 EndZ=0
    g1: LineSegment StartX=17.2106 StartY=49.0304 StartZ=0 EndX=49.0304 EndY=17.2106 EndZ=0
    g2: LineSegment StartX=49.0304 StartY=17.2106 StartZ=0 EndX=75.3298 EndY=7.63834 EndZ=0
    g3: LineSegment StartX=7.63834 StartY=75.3298 StartZ=0 EndX=13.6383 EndY=83.8987 EndZ=0
    g4: LineSegment StartX=75.3298 StartY=7.63834 StartZ=0 EndX=83.8987 EndY=13.6383 EndZ=0
    g5: ArcOfCircle CenterX=0 CenterY=0 CenterZ=0 NormalX=0 NormalY=0 NormalZ=1 AngleXU=0 Radius=85 StartAngle=0.161148 EndAngle=1.40965
  constraints (8):
    c: Coincident(g1,g0)
    c: Coincident(g2,g1)
    c: Distance(g1) = 45
    c: Equal(g0,g2)
    c: Coincident(g3,g0)
    c: Coincident(g4,g2)
    c: Coincident(g5,g-1)
    c: Coincident(g5,g3)
FEATURE [PartDesign::Pad] Pad091
  Direction = (0,0,-1)
  Length = 3
  Length2 = 10
  Placement = pos=(0,0,0) rot=(1,0,0;3.14159rad)
  Profile = -> Sketch193
  ReferenceAxis = -> Sketch193 [N_Axis]
  Type = 0
FEATURE [Sketcher::SketchObject] Sketch248
  FullyConstrained = false
  MapMode = 5
  Placement = pos=(0,0,0) rot=(1,0,0;3.14159rad)
  sketch-geometry (20):
    g0: LineSegment StartX=7.63834 StartY=75.3298 StartZ=0 EndX=17.2106 EndY=49.0304 EndZ=0
    g1: LineSegment StartX=17.2106 StartY=49.0304 StartZ=0 EndX=49.0304 EndY=17.2106 EndZ=0
    g2: LineSegment StartX=49.0304 StartY=17.2106 StartZ=0 EndX=75.3298 EndY=7.63834 EndZ=0
    g3: LineSegment StartX=7.63834 StartY=75.3298 StartZ=0 EndX=-32.942 EndY=68.1744 EndZ=0
    g4: LineSegment StartX=-32.942 StartY=68.1744 StartZ=0 EndX=-41.5109 EndY=74.1744 EndZ=0
    g5: LineSegment StartX=-74.1744 StartY=41.5109 StartZ=0 EndX=-68.1744 EndY=32.942 EndZ=0
    g6: LineSegment StartX=-68.1744 StartY=32.942 StartZ=0 EndX=-75.1847 EndY=-6.81529 EndZ=0
    g7: LineSegment StartX=-6.81529 StartY=-75.1847 StartZ=0 EndX=32.942 EndY=-68.1744 EndZ=0
    g8: LineSegment StartX=32.942 StartY=-68.1744 StartZ=0 EndX=41.5109 EndY=-74.1744 EndZ=0
    g9: LineSegment StartX=74.1744 StartY=-41.5109 StartZ=0 EndX=68.1744 EndY=-32.942 EndZ=0
    g10: LineSegment StartX=68.1744 StartY=-32.942 StartZ=0 EndX=75.3298 EndY=7.63834 EndZ=0
    g11: ArcOfCircle CenterX=0 CenterY=0 CenterZ=0 NormalX=0 NormalY=0 NormalZ=1 AngleXU=0 Radius=85 StartAngle=2.08101 EndAngle=2.63138
    g12: ArcOfCircle CenterX=0 CenterY=0 CenterZ=0 NormalX=0 NormalY=0 NormalZ=1 AngleXU=0 Radius=85 StartAngle=5.2226 EndAngle=5.77297
    g13: LineSegment StartX=-75.1847 StartY=-6.81529 StartZ=0 EndX=-85.7913 EndY=-17.4219 EndZ=0
    g14: LineSegment StartX=-85.7913 StartY=-17.4219 StartZ=0 EndX=-75.1847 EndY=-28.0285 EndZ=0
    g15: LineSegment StartX=-75.1847 StartY=-28.0285 StartZ=0 EndX=-64.5781 EndY=-17.4219 EndZ=0
    g16: LineSegment StartX=-64.5781 StartY=-17.4219 StartZ=0 EndX=-17.4219 EndY=-64.5781 EndZ=0
    g17: LineSegment StartX=-17.4219 StartY=-64.5781 StartZ=0 EndX=-28.0285 EndY=-75.1847 EndZ=0
    g18: LineSegment StartX=-28.0285 StartY=-75.1847 StartZ=0 EndX=-17.4219 EndY=-85.7913 EndZ=0
    g19: LineSegment StartX=-17.4219 StartY=-85.7913 StartZ=0 EndX=-6.81529 EndY=-75.1847 EndZ=0
  constraints (38):
    c: Coincident(g1,g0)
    c: Coincident(g2,g1)
    c: Distance(g1) = 45
    c: Equal(g0,g2)
    c: Coincident(g3,g0)
    c: Coincident(g4,g3)
    c: Coincident(g6,g5)
    c: Coincident(g8,g7)
    c: Coincident(g10,g9)
    c: Coincident(g10,g2)
    c: Coincident(g11,g4)
    c: Coincident(g12,g11)
    c: Coincident(g12,g8)
    c: Coincident(g12,g9)
    c: DistanceX(g6) = -75.1847
    c: DistanceY(g6) = -6.81529
    c: DistanceX(g7) = -6.81529
    c: DistanceY(g7) = -75.1847
    c: Coincident(g13,g6)
    c: Coincident(g14,g13)
    c: Coincident(g15,g14)
    c: Coincident(g16,g15)
    c: Coincident(g17,g16)
    c: Coincident(g18,g17)
    c: Coincident(g19,g18)
    c: Coincident(g19,g7)
    c: Parallel(g13,g15)
    c: Parallel(g17,g19)
    c: Parallel(g16,g14)
    c: Parallel(g16,g18)
    c: Perpendicular(g17,g18)
    c: Perpendicular(g15,g14)
    c: Equal(g15,g17)
    c: Equal(g18,g14)
    c: Equal(g13,g15)
    c: Equal(g17,g19)
    c: Distance(g14) = 15
    c: Distance(g15) = 15
FEATURE [PartDesign::Pad] Pad092
  Direction = (0,0,-1)
  Length = 3
  Length2 = 10
  Placement = pos=(0,0,0) rot=(1,0,0;3.14159rad)
  Profile = -> Sketch248
  ReferenceAxis = -> Sketch248 [N_Axis]
  Type = 0
FEATURE [PartDesign::SubShapeBinder] Binder039
  BindCopyOnChange = 0
  BindMode = 0
  ClaimChildren = false
  Context = -> Part014 [Body093.Binder039.]
  Fuse = false
  MakeFace = true
  OffsetFill = false
  OffsetIntersection = false
  OffsetJoinType = 0
  OffsetOpenResult = false
  PartialLoad = false
  Relative = true
  Support = -> [Body[Pocket055.Sketch126.]]
  _Version = 2
FEATURE [PartDesign::Pocket] Pocket110
  BaseFeature = -> Pad092
  Direction = (0,0,-1)
  Length = 5
  Length2 = 5
  Placement = pos=(0,0,0) rot=(1,0,0;3.14159rad)
  Profile = -> Binder039
  Type = 1
FEATURE [PartDesign::SubShapeBinder] Binder040
  BindCopyOnChange = 0
  BindMode = 0
  ClaimChildren = false
  Context = -> Part014 [Body073.Binder040.]
  Fuse = false
  MakeFace = true
  OffsetFill = false
  OffsetIntersection = false
  OffsetJoinType = 0
  OffsetOpenResult = false
  PartialLoad = false
  Relative = true
  Support = -> [Body[Pocket055.Sketch126.]]
  _Version = 2
FEATURE [PartDesign::Pocket] Pocket111
  BaseFeature = -> Pad091
  Direction = (0,0,-1)
  Length = 5
  Length2 = 5
  Placement = pos=(0,0,0) rot=(1,0,0;3.14159rad)
  Profile = -> Binder040
  Type = 1
FEATURE [PartDesign::Body] Body073  label="Lower plate small"
  Group = -> [Sketch193,Pad091,Binder040,Pocket111]
  Origin = -> Origin300
  Placement = pos=(0,0,-34.2) rot=(0,0,1;0.785398rad)
  Tip = -> Pocket111
FEATURE [Sketcher::SketchObject] Sketch249
  ExternalGeometry = -> [Pocket052]
  FullyConstrained = false
  MapMode = 5
  Placement = pos=(0,0,-6) rot=(1,0,0;3.14159rad)
  Support = -> [Pocket052]
  sketch-geometry (18):
    g0: LineSegment StartX=-61.4103 StartY=-33.3313 StartZ=0 EndX=-64.3168 EndY=-34.0745 EndZ=0
    g1: LineSegment StartX=-64.3168 StartY=-34.0745 StartZ=0 EndX=-65.1265 EndY=-36.9631 EndZ=0
    g2: LineSegment StartX=-65.1265 StartY=-36.9631 StartZ=0 EndX=-63.0297 EndY=-39.1087 EndZ=0
    g3: LineSegment StartX=-63.0297 StartY=-39.1087 StartZ=0 EndX=-60.1232 EndY=-38.3655 EndZ=0
    g4: LineSegment StartX=-60.1232 StartY=-38.3655 StartZ=0 EndX=-59.3135 EndY=-35.4769 EndZ=0
    g5: LineSegment StartX=-59.3135 StartY=-35.4769 StartZ=0 EndX=-61.4103 EndY=-33.3313 EndZ=0
    g6: Circle CenterX=-62.22 CenterY=-36.22 CenterZ=0 NormalX=0 NormalY=0 NormalZ=1 AngleXU=0 Radius=3
    g7: LineSegment StartX=-62.22 StartY=-36.22 StartZ=0 EndX=-66.22 EndY=-40.22 EndZ=0
    g8: LineSegment StartX=-62.22 StartY=-36.22 StartZ=0 EndX=-66.22 EndY=-32.22 EndZ=0
    g9: LineSegment StartX=95.3648 StartY=-34.4404 StartZ=0 EndX=95.0313 EndY=-37.4218 EndZ=0
    g10: LineSegment StartX=95.0313 StartY=-37.4218 StartZ=0 EndX=97.4464 EndY=-39.2014 EndZ=0
    g11: LineSegment StartX=97.4464 StartY=-39.2014 StartZ=0 EndX=100.195 EndY=-37.9996 EndZ=0
    g12: LineSegment StartX=100.195 StartY=-37.9996 StartZ=0 EndX=100.529 EndY=-35.0182 EndZ=0
    g13: LineSegment StartX=100.529 StartY=-35.0182 StartZ=0 EndX=98.1136 EndY=-33.2386 EndZ=0
    g14: LineSegment StartX=98.1136 StartY=-33.2386 StartZ=0 EndX=95.3648 EndY=-34.4404 EndZ=0
    g15: Circle CenterX=97.78 CenterY=-36.22 CenterZ=0 NormalX=0 NormalY=0 NormalZ=1 AngleXU=0 Radius=3
    g16: LineSegment StartX=101.78 StartY=-32.22 StartZ=0 EndX=97.78 EndY=-36.22 EndZ=0
    g17: LineSegment StartX=97.78 StartY=-36.22 StartZ=0 EndX=101.78 EndY=-40.22 EndZ=0
  constraints (40):
    c: Coincident(g0,g1)
    c: Coincident(g1,g2)
    c: Coincident(g2,g3)
    c: Coincident(g3,g4)
    c: Coincident(g4,g5)
    c: Coincident(g5,g0)
    c: Equal(g0, g1-g5) x5
    c: PointOnObject(g0,g6)
    c: PointOnObject(g1,g6)
    c: PointOnObject(g2,g6)
    c: PointOnObject(g3,g6)
    c: PointOnObject(g4,g6)
    c: PointOnObject(g5,g6)
    c: Diameter(g6) = 6
    c: Coincident(g7,g6)
    c: Coincident(g7,g-3)
    c: Coincident(g8,g6)
    c: Coincident(g8,g-3)
    c: Equal(g8,g7)
    c: Coincident(g9,g10)
    c: Coincident(g10,g11)
    c: Coincident(g11,g12)
    c: Coincident(g12,g13)
    c: Coincident(g13,g14)
    c: Coincident(g14,g9)
    c: Equal(g9, g10-g14) x5
    c: PointOnObject(g9,g15)
    c: PointOnObject(g10,g15)
    c: PointOnObject(g11,g15)
    c: PointOnObject(g12,g15)
    c: PointOnObject(g13,g15)
    c: PointOnObject(g14,g15)
    c: Diameter(g15) = 6
    c: Coincident(g16,g-4)
    c: Coincident(g16,g15)
    c: Coincident(g17,g15)
    c: Coincident(g17,g-4)
    c: Equal(g16,g17)
    c: Perpendicular(g8,g7)
    c: Perpendicular(g16,g17)
FEATURE [PartDesign::Pad] Pad093
  BaseFeature = -> Pocket052
  Direction = (0,0,-1)
  Length = 50
  Length2 = 10
  Profile = -> Sketch249
  ReferenceAxis = -> Sketch249 [N_Axis]
  Type = 0
FEATURE [Sketcher::SketchObject] Sketch250
  ExternalGeometry = -> [Pad093]
  FullyConstrained = true
  MapMode = 5
  Support = -> [Pad093]
  sketch-geometry (6):
    g0: Circle CenterX=-62.22 CenterY=36.22 CenterZ=0 NormalX=0 NormalY=0 NormalZ=1 AngleXU=0 Radius=1.5
    g1: LineSegment StartX=-66.22 StartY=32.22 StartZ=0 EndX=-62.22 EndY=36.22 EndZ=0
    g2: LineSegment StartX=-62.22 StartY=36.22 StartZ=0 EndX=-66.22 EndY=40.22 EndZ=0
    g3: Circle CenterX=97.78 CenterY=36.22 CenterZ=0 NormalX=0 NormalY=0 NormalZ=1 AngleXU=0 Radius=1.5
    g4: LineSegment StartX=101.78 StartY=32.22 StartZ=0 EndX=97.78 EndY=36.22 EndZ=0
    g5: LineSegment StartX=97.78 StartY=36.22 StartZ=0 EndX=101.78 EndY=40.22 EndZ=0
  constraints (14):
    c: Diameter(g0) = 3
    c: Coincident(g1,g-3)
    c: Coincident(g1,g0)
    c: Coincident(g2,g-3)
    c: Coincident(g2,g0)
    c: Equal(g1,g2)
    c: Diameter(g3) = 3
    c: Coincident(g4,g-4)
    c: Coincident(g4,g3)
    c: Coincident(g5,g3)
    c: Coincident(g5,g-4)
    c: Equal(g4,g5)
    c: Perpendicular(g2,g1)
    c: Perpendicular(g5,g4)
FEATURE [PartDesign::Pocket] Pocket112
  BaseFeature = -> Pad093
  Direction = (0,0,-1)
  Length = 5
  Length2 = 5
  Profile = -> Sketch250
  ReferenceAxis = -> Sketch250 [N_Axis]
  Type = 1
FEATURE [PartDesign::SubShapeBinder] Binder044
  BindCopyOnChange = 0
  BindMode = 0
  ClaimChildren = false
  Context = -> Part014 [Body093.Binder044.]
  Fuse = false
  MakeFace = true
  OffsetFill = false
  OffsetIntersection = false
  OffsetJoinType = 0
  OffsetOpenResult = false
  PartialLoad = false
  Relative = true
  _Version = 2
FEATURE [PartDesign::Pocket] Pocket116
  BaseFeature = -> Pocket110
  Direction = (0,0,-1)
  Length = 5
  Length2 = 5
  Placement = pos=(0,0,0) rot=(1,0,0;3.14159rad)
  Profile = -> Binder044
  Type = 1
FEATURE [PartDesign::Body] Body093  label="Lower plate large"
  Group = -> [Sketch248,Pad092,Binder039,Pocket110,Binder044,Pocket116]
  Origin = -> Origin340
  Placement = pos=(0,0,-34.2) rot=(0,0,1;0.785398rad)
  Tip = -> Pocket116
FEATURE [PartDesign::SubShapeBinder] Binder045
  BindCopyOnChange = 0
  BindMode = 0
  ClaimChildren = false
  Context = -> Part014 [Body044.Binder045.]
  Fuse = false
  MakeFace = true
  OffsetFill = false
  OffsetIntersection = false
  OffsetJoinType = 0
  OffsetOpenResult = false
  PartialLoad = false
  Relative = true
  _Version = 2
FEATURE [PartDesign::Pocket] Pocket117
  BaseFeature = -> Pocket097
  Direction = (0,0,-1)
  Length = 5
  Length2 = 5
  Profile = -> Binder045
  Type = 1
FEATURE [PartDesign::Body] Body044  label="Lower plate full"
  Group = -> [Sketch102,Pad070,Binder013,Pocket094,Binder027,Pocket096,PolarPattern023,PolarPattern024,PolarPattern025,Binder028,Pocket097,Sketch138,Binder045,Pocket117]
  Origin = -> Origin248
  Placement = pos=(0,0,-37.2) rot=(0,0,1;0.785398rad)
  Tip = -> Pocket117
FEATURE [App::Part] Part014  label="Lower plate"
  Group = -> [Body044,Body073,Body093]
  Origin = -> Origin260
FEATURE [Part::Feature] Part__Feature1467  label="rt10"
  shape: bbox 14 x 14 x 16.7 mm, 16 faces (baked)
FEATURE [Part::Feature] Part__Feature1468  label="rt011"
  shape: bbox 5 x 5 x 0.7243 mm, 72 faces (baked)
FEATURE [Part::Feature] Part__Feature1469  label="rt012"
  shape: bbox 12.1 x 4.6 x 2.3 mm, 1904 faces (baked)
FEATURE [Part::Feature] Part__Feature1470  label="rt013"
  shape: bbox 35.56 x 16.51 x 1.6 mm, 134 faces (baked)
FEATURE [Part::Feature] Part__Feature1471  label="rt014"
  shape: bbox 4.35 x 4.35 x 4.4 mm, 6 faces (baked)
FEATURE [Part::Feature] Part__Feature1472  label="rt015"
  shape: bbox 4.35 x 4.35 x 4.4 mm, 6 faces (baked)
FEATURE [Part::Feature] Part__Feature1473  label="rt016"
  shape: bbox 12.11 x 4.605 x 2.705 mm, 1046 faces (baked)
FEATURE [Part::Feature] Part__Feature1474  label="rt017"
  shape: bbox 5 x 7 x 1.1 mm, 7 faces (baked)
FEATURE [Part::Feature] Part__Feature1475  label="rt018"
  shape: bbox 0.4 x 2 x 16.99 mm, 25 faces (baked)
FEATURE [Part::Feature] Part__Feature1476  label="rt019"
  shape: bbox 0.4 x 2 x 16.99 mm, 25 faces (baked)
FEATURE [Part::Feature] Part__Feature1477  label="rt020"
  shape: bbox 0.4 x 2 x 16.99 mm, 25 faces (baked)
FEATURE [Part::Feature] Part__Feature1478  label="rt021"
  shape: bbox 0.4 x 2 x 16.99 mm, 25 faces (baked)
FEATURE [Part::Feature] Part__Feature1479  label="rt022"
  shape: bbox 0.4 x 2 x 16.99 mm, 25 faces (baked)
FEATURE [Part::Feature] Part__Feature1480  label="rt023"
  shape: bbox 0.4 x 2 x 16.99 mm, 25 faces (baked)
FEATURE [Part::Feature] Part__Feature1481  label="rt024"
  shape: bbox 0.4 x 2 x 16.99 mm, 25 faces (baked)
FEATURE [Part::Feature] Part__Feature1482  label="rt025"
  shape: bbox 0.4 x 2 x 16.99 mm, 25 faces (baked)
FEATURE [Part::Feature] Part__Feature1483  label="rt026"
  shape: bbox 2.54 x 20.32 x 8.5 mm, 114 faces (baked)
FEATURE [Part::Feature] Part__Feature1484  label="rt027"
  shape: bbox 0.4 x 2 x 16.99 mm, 25 faces (baked)
FEATURE [Part::Feature] Part__Feature1485  label="rt028"
  shape: bbox 0.4 x 2 x 16.99 mm, 25 faces (baked)
FEATURE [Part::Feature] Part__Feature1486  label="rt029"
  shape: bbox 0.4 x 2 x 16.99 mm, 25 faces (baked)
FEATURE [Part::Feature] Part__Feature1487  label="rt030"
  shape: bbox 0.4 x 2 x 16.99 mm, 25 faces (baked)
FEATURE [Part::Feature] Part__Feature1488  label="rt031"
  shape: bbox 0.4 x 2 x 16.99 mm, 25 faces (baked)
FEATURE [Part::Feature] Part__Feature1489  label="rt032"
  shape: bbox 0.4 x 2 x 16.99 mm, 25 faces (baked)
FEATURE [Part::Feature] Part__Feature1490  label="rt033"
  shape: bbox 0.4 x 2 x 16.99 mm, 25 faces (baked)
FEATURE [Part::Feature] Part__Feature1491  label="rt034"
  shape: bbox 0.4 x 2 x 16.99 mm, 25 faces (baked)
FEATURE [Part::Feature] Part__Feature1492  label="rt035"
  shape: bbox 2.54 x 20.32 x 8.5 mm, 114 faces (baked)
FEATURE [Part::Feature] Part__Feature1495  label="rt038"
  shape: bbox 6 x 7.7 x 8.35 mm, 81 faces (baked)
FEATURE [Part::Feature] Part__Feature1501  label="rt044"
  shape: bbox 8 x 8 x 1.2 mm, 7 faces (baked)
FEATURE [Part::Feature] Part__Feature1503  label="rt046"
  shape: bbox 5 x 6 x 1 mm, 6 faces (baked)
FEATURE [Part::Feature] Part__Feature1507  label="rt050"
  shape: bbox 10 x 10 x 1.5 mm, 6 faces (baked)
FEATURE [Part::Feature] Part__Feature1510  label="rt053"
  shape: bbox 5.08 x 6.35 x 5.715 mm, 90 faces (baked)
FEATURE [Part::Feature] Part__Feature1511  label="rt054"
  shape: bbox 1.676 x 5.486 x 4.293 mm, 91 faces (baked)
FEATURE [Part::Feature] Part__Feature1512  label="rt055"
  shape: bbox 5.842 x 5.486 x 2.017 mm, 71 faces (baked)
FEATURE [Part::Feature] Part__Feature1514  label="rt057"
  shape: bbox 4 x 4 x 1 mm, 7 faces (baked)
FEATURE [Part::Feature] Part__Feature1517  label="rt060"
  shape: bbox 0.4 x 2 x 16.99 mm, 25 faces (baked)
FEATURE [Part::Feature] Part__Feature1518  label="rt061"
  shape: bbox 0.4 x 2 x 16.99 mm, 25 faces (baked)
FEATURE [Part::Feature] Part__Feature1519  label="rt062"
  shape: bbox 0.4 x 2 x 16.99 mm, 25 faces (baked)
FEATURE [Part::Feature] Part__Feature1520  label="rt063"
  shape: bbox 0.4 x 2 x 16.99 mm, 25 faces (baked)
FEATURE [Part::Feature] Part__Feature1521  label="rt064"
  shape: bbox 0.4 x 2 x 16.99 mm, 25 faces (baked)
FEATURE [Part::Feature] Part__Feature1522  label="rt065"
  shape: bbox 0.4 x 2 x 16.99 mm, 25 faces (baked)
FEATURE [Part::Feature] Part__Feature1523  label="rt066"
  shape: bbox 0.4 x 2 x 16.99 mm, 25 faces (baked)
FEATURE [Part::Feature] Part__Feature1524  label="rt067"
  shape: bbox 0.4 x 2 x 16.99 mm, 25 faces (baked)
FEATURE [Part::Feature] Part__Feature1525  label="rt068"
  shape: bbox 2.54 x 20.32 x 8.5 mm, 114 faces (baked)
FEATURE [Part::Feature] Part__Feature1527  label="rt070"
  shape: bbox 3.2 x 1.6 x 1.2 mm, 240 faces (baked)
FEATURE [Part::Feature] Part__Feature1542  label="rt085"
  shape: bbox 1.6 x 2 x 0.65 mm, 6 faces (baked)
FEATURE [Part::Feature] Part__Feature1543  label="rt086"
  shape: bbox 1.4 x 3.2 x 1 mm, 6 faces (baked)
FEATURE [Part::Feature] Part__Feature1544  label="rt087"
  shape: bbox 2.5 x 1.2 x 0.5 mm, 6 faces (baked)
FEATURE [Part::Feature] Part__Feature1547  label="rt090"
  shape: bbox 0.8 x 1.5 x 0.35 mm, 6 faces (baked)
FEATURE [Part::Feature] Part__Feature1548  label="rt091"
  shape: bbox 0.8 x 1.1 x 0.049 mm, 6 faces (baked)
FEATURE [Part::Feature] Part__Feature1549  label="rt092"
  shape: bbox 3 x 3 x 1 mm, 6 faces (baked)
FEATURE [Part::Feature] Part__Feature1576  label="rt119"
  shape: bbox 3 x 3 x 0.3 mm, 6 faces (baked)
FEATURE [Part::Feature] Part__Feature1578  label="rt121"
  shape: bbox 1.2 x 1.6 x 0.62 mm, 6 faces (baked)
FEATURE [Part::Feature] Part__Feature1585  label="rt128"
  shape: bbox 1.5 x 2.5 x 0.6 mm, 7 faces (baked)
FEATURE [Part::Feature] Part__Feature1591  label="rt134"
  shape: bbox 2 x 1.25 x 1.25 mm, 58 faces (baked)
FEATURE [Part::Feature] Part__Feature1603  label="rt146"
  shape: bbox 2 x 1.25 x 1.25 mm, 58 faces (baked)
FEATURE [Part::Feature] Part__Feature1604  label="rt147"
  shape: bbox 2 x 1.25 x 1.25 mm, 58 faces (baked)
FEATURE [Part::Feature] Part__Feature1608  label="rt151"
  shape: bbox 1.5 x 2.5 x 0.6 mm, 7 faces (baked)
FEATURE [Part::Feature] Part__Feature1615  label="rt158"
  shape: bbox 1.351 x 2.201 x 1.05 mm, 34 faces (baked)
FEATURE [Part::Feature] Part__Feature1616  label="rt159"
  shape: bbox 1.6 x 2 x 1 mm, 7 faces (baked)
FEATURE [Part::Feature] Part__Feature1617  label="rt160"
  shape: bbox 0.5 x 1 x 0.5 mm, 58 faces (baked)
FEATURE [Part::Feature] Part__Feature1700  label="rt243"
  shape: bbox 1.25 x 2 x 1.25 mm, 58 faces (baked)
FEATURE [Part::Feature] Part__Feature1702  label="rt245"
  shape: bbox 1.25 x 2 x 1.25 mm, 58 faces (baked)
FEATURE [Part::Feature] Part__Feature1703  label="rt246"
  shape: bbox 1.6 x 2 x 1 mm, 7 faces (baked)
FEATURE [Part::Feature] Part__Feature1722  label="rt265"
  shape: bbox 2 x 1.25 x 1.25 mm, 58 faces (baked)
FEATURE [Part::Feature] Part__Feature1723  label="rt266"
  shape: bbox 1.25 x 2 x 1.25 mm, 58 faces (baked)
FEATURE [Part::Feature] Part__Feature1738  label="rt281"
  shape: bbox 2 x 1.25 x 1.25 mm, 58 faces (baked)
FEATURE [Part::Feature] Part__Feature1739  label="rt282"
  shape: bbox 11.4 x 11.95 x 1.452 mm, 410 faces (baked)
FEATURE [Part::Feature] Part__Feature1740  label="rt283"
  shape: bbox 1.25 x 2 x 1.25 mm, 58 faces (baked)
FEATURE [Part::Feature] Part__Feature1741  label="rt284"
  shape: bbox 2 x 1.25 x 1.25 mm, 58 faces (baked)
FEATURE [Part::Feature] Part__Feature1742  label="rt285"
  shape: bbox 1.25 x 2 x 1.25 mm, 58 faces (baked)
FEATURE [Part::Feature] Part__Feature1750  label="rt293"
  shape: bbox 1.5 x 2.5 x 0.6 mm, 7 faces (baked)
FEATURE [Part::Feature] Part__Feature1754  label="rt297"
  shape: bbox 1.2 x 1.6 x 0.6 mm, 6 faces (baked)
FEATURE [Part::Feature] Part__Feature1757  label="rt300"
  shape: bbox 2 x 1.25 x 1.25 mm, 58 faces (baked)
FEATURE [Part::Feature] Part__Feature1758  label="rt301"
  shape: bbox 1.6 x 2 x 1 mm, 7 faces (baked)
FEATURE [Part::Feature] Part__Feature1768  label="rt311"
  shape: bbox 2.988 x 2.8 x 1.175 mm, 78 faces (baked)
FEATURE [Part::Feature] Part__Feature1772  label="rt315"
  shape: bbox 1.351 x 2.201 x 1.05 mm, 34 faces (baked)
FEATURE [Part::Feature] Part__Feature1776  label="rt319"
  shape: bbox 1.351 x 2.201 x 1.05 mm, 34 faces (baked)
FEATURE [Part::Feature] Part__Feature1777  label="rt320"
  shape: bbox 2.2 x 1.2 x 0.6 mm, 7 faces (baked)
FEATURE [Part::Feature] Part__Feature1778  label="rt321"
  shape: bbox 1.25 x 2 x 1.25 mm, 58 faces (baked)
FEATURE [Part::Feature] Part__Feature1779  label="rt322"
  shape: bbox 1.25 x 2 x 1.25 mm, 58 faces (baked)
FEATURE [Part::Feature] Part__Feature1796  label="rt339"
  shape: bbox 8.34 x 6.62 x 3.56 mm, 238 faces (baked)
FEATURE [Part::Feature] Part__Feature1823  label="rt366"
  shape: bbox 9.58 x 7.53 x 4.16 mm, 463 faces (baked)
FEATURE [Part::Feature] Part__Feature1828  label="rt371"
  shape: bbox 0.4 x 2 x 16.99 mm, 25 faces (baked)
FEATURE [Part::Feature] Part__Feature1829  label="rt372"
  shape: bbox 0.4 x 2 x 16.99 mm, 25 faces (baked)
FEATURE [Part::Feature] Part__Feature1830  label="rt373"
  shape: bbox 0.4 x 2 x 16.99 mm, 25 faces (baked)
FEATURE [Part::Feature] Part__Feature1831  label="rt374"
  shape: bbox 0.4 x 2 x 16.99 mm, 25 faces (baked)
FEATURE [Part::Feature] Part__Feature1832  label="rt375"
  shape: bbox 0.4 x 2 x 16.99 mm, 25 faces (baked)
FEATURE [Part::Feature] Part__Feature1833  label="rt376"
  shape: bbox 0.4 x 2 x 16.99 mm, 25 faces (baked)
FEATURE [Part::Feature] Part__Feature1834  label="rt377"
  shape: bbox 0.4 x 2 x 16.99 mm, 25 faces (baked)
FEATURE [Part::Feature] Part__Feature1835  label="rt378"
  shape: bbox 0.4 x 2 x 16.99 mm, 25 faces (baked)
FEATURE [Part::Feature] Part__Feature1836  label="rt379"
  shape: bbox 2.54 x 20.32 x 8.5 mm, 114 faces (baked)
FEATURE [Part::Feature] Part__Feature1837  label="rt380"
  shape: bbox 0.5 x 1 x 0.3375 mm, 36 faces (baked)
FEATURE [Part::Feature] Part__Feature1857  label="rt400"
  shape: bbox 4.718 x 3.55 x 1.549 mm, 350 faces (baked)
FEATURE [Part::Feature] Part__Feature1862  label="rt405"
  shape: bbox 2.5 x 3.2 x 0.8 mm, 47 faces (baked)
FEATURE [Part::Feature] Part__Feature1863  label="rt406"
  shape: bbox 3.21 x 1.803 x 2.385 mm, 34 faces (baked)
FEATURE [Part::Feature] Part__Feature1874  label="rt417"
  shape: bbox 4.718 x 3.55 x 1.549 mm, 350 faces (baked)
FEATURE [Part::Feature] Part__Feature1878  label="rt421"
  shape: bbox 1.803 x 3.21 x 2.385 mm, 34 faces (baked)
FEATURE [Part::Feature] Part__Feature1886  label="rt429"
  shape: bbox 0.991 x 2.312 x 1.054 mm, 10 faces (baked)
FEATURE [Part::Feature] Part__Feature1887  label="rt430"
  shape: bbox 0.991 x 2.312 x 1.054 mm, 10 faces (baked)
FEATURE [Part::Feature] Part__Feature1888  label="rt431"
  shape: bbox 3.088 x 2.999 x 2.109 mm, 16 faces (baked)
FEATURE [Part::Feature] Part__Feature1889  label="rt432"
  shape: bbox 0.617 x 2.874 x 0.051 mm, 6 faces (baked)
FEATURE [Part::Feature] Part__Feature1890  label="rt433"
  shape: bbox 0.991 x 2.312 x 1.054 mm, 10 faces (baked)
FEATURE [Part::Feature] Part__Feature1891  label="rt434"
  shape: bbox 0.991 x 2.312 x 1.054 mm, 10 faces (baked)
FEATURE [Part::Feature] Part__Feature1892  label="rt435"
  shape: bbox 3.088 x 2.999 x 2.109 mm, 16 faces (baked)
FEATURE [Part::Feature] Part__Feature1893  label="rt436"
  shape: bbox 0.617 x 2.874 x 0.051 mm, 6 faces (baked)
FEATURE [Part::Feature] Part__Feature1905  label="rt448"
  shape: bbox 35.56 x 44.45 x 1.2 mm, 64 faces (baked)
FEATURE [Part::Feature] Part__Feature1906  label="rt449"
  shape: bbox 15.5 x 16.25 x 6.3 mm, 24 faces (baked)
FEATURE [Part::Feature] Part__Feature1907  label="rt450"
  shape: bbox 23.8 x 17 x 8 mm, 20 faces (baked)
FEATURE [App::Part] rt10  label="OpenMV RT1062"
  Group = -> [Part__Feature1467,Part__Feature1468,Part__Feature1469,Part__Feature1470,Part__Feature1471,Part__Feature1472,Part__Feature1473,Part__Feature1474,Part__Feature1475,Part__Feature1476,Part__Feature1477,Part__Feature1478,Part__Feature1479,Part__Feature1480,Part__Feature1481,Part__Feature1482,Part__Feature1483,Part__Feature1484,Part__Feature1485,Part__Feature1486,Part__Feature1487,Part__Feature1488,+86 more]
  Origin = -> Origin341
  Placement = pos=(0,0,4.2) rot=(0,0,1;0rad)
FEATURE [PartDesign::SubShapeBinder] Binder047
  BindCopyOnChange = 0
  BindMode = 0
  ClaimChildren = false
  Context = -> Part012 [Body003.Binder047.]
  Fuse = false
  MakeFace = true
  OffsetFill = false
  OffsetIntersection = false
  OffsetJoinType = 0
  OffsetOpenResult = false
  PartialLoad = false
  Relative = true
  Support = -> [Body[Pocket055.Sketch126.]]
  _Version = 2
FEATURE [PartDesign::SubShapeBinder] Binder048
  BindCopyOnChange = 0
  BindMode = 0
  ClaimChildren = false
  Context = -> Part012 [Body051.Binder048.]
  Fuse = false
  MakeFace = true
  OffsetFill = false
  OffsetIntersection = false
  OffsetJoinType = 0
  OffsetOpenResult = false
  PartialLoad = false
  Relative = true
  Support = -> [Body[Pocket055.Sketch126.]]
  _Version = 2
FEATURE [PartDesign::SubShapeBinder] Binder049
  BindCopyOnChange = 0
  BindMode = 0
  ClaimChildren = false
  Context = -> Part012 [Body052.Binder049.]
  Fuse = false
  MakeFace = true
  OffsetFill = false
  OffsetIntersection = false
  OffsetJoinType = 0
  OffsetOpenResult = false
  PartialLoad = false
  Relative = true
  Support = -> [Body[Pocket055.Sketch126.]]
  _Version = 2
FEATURE [PartDesign::Pocket] Pocket119
  BaseFeature = -> Revolution003
  Direction = (0,0,-1)
  Length = 5
  Length2 = 5
  Placement = pos=(0,0,0) rot=(1,0,0;1.5708rad)
  Profile = -> Binder049
  Type = 1
FEATURE [PartDesign::Body] Body052  label="Outer shielding 3"
  Group = -> [Sketch128,Revolution003,Binder049,Pocket119]
  Origin = -> Origin257
  Placement = pos=(0,-3,0) rot=(0,0,-1;1.5708rad)
  Tip = -> Pocket119
FEATURE [PartDesign::Pocket] Pocket120
  BaseFeature = -> Revolution002
  Direction = (0,0,-1)
  Length = 5
  Length2 = 5
  Placement = pos=(0,0,0) rot=(1,0,0;1.5708rad)
  Profile = -> Binder048
  Type = 1
FEATURE [PartDesign::Body] Body051  label="Outer shielding 2"
  Group = -> [Sketch127,Revolution002,Binder048,Pocket120]
  Origin = -> Origin256
  Placement = pos=(-3,1e-15,0) rot=(0,0,1;3.14159rad)
  Tip = -> Pocket120
FEATURE [PartDesign::Pocket] Pocket121
  BaseFeature = -> Revolution001
  Direction = (0,0,-1)
  Length = 5
  Length2 = 5
  Placement = pos=(0,0,0) rot=(1,0,0;1.5708rad)
  Profile = -> Binder047
  Type = 1
FEATURE [PartDesign::SubShapeBinder] Binder050
  BindCopyOnChange = 0
  BindMode = 0
  ClaimChildren = false
  Context = -> Body [Binder050.]
  Fuse = false
  MakeFace = true
  OffsetFill = false
  OffsetIntersection = false
  OffsetJoinType = 0
  OffsetOpenResult = false
  PartialLoad = false
  Relative = true
  Support = -> [Part015[Body025.Pocket112.Sketch250.]]
  _Version = 2
FEATURE [PartDesign::Pocket] Pocket122
  BaseFeature = -> Pocket109
  Direction = (-2e-16,-2e-16,-1)
  Length = 5
  Length2 = 5
  Profile = -> Binder050
  Type = 1
FEATURE [Sketcher::SketchObject] Sketch251
  FullyConstrained = false
  MapMode = 5
  Placement = pos=(0,0,3) rot=(0,0,1;0rad)
  sketch-geometry (2):
    g0: Circle CenterX=0 CenterY=0 CenterZ=0 NormalX=0 NormalY=0 NormalZ=1 AngleXU=0 Radius=28
    g1: Circle CenterX=0 CenterY=0 CenterZ=0 NormalX=0 NormalY=0 NormalZ=1 AngleXU=0 Radius=25.25
  constraints (2):
    c: Coincident(g1,g0)
    c: Diameter(g1) = 50.5
FEATURE [PartDesign::Pad] Pad095
  BaseFeature = -> Pad007
  Direction = (0,0,1)
  Length = 5
  Length2 = 10
  Profile = -> Sketch251
  ReferenceAxis = -> Sketch251 [N_Axis]
  Type = 0
FEATURE [Sketcher::SketchObject] Sketch253
  FullyConstrained = true
  MapMode = 5
  Placement = pos=(0,0,0) rot=(0.57735,0.57735,-0.57735;4.18879rad)
  Support = -> [Pad076]
  sketch-geometry (1):
    g0: Circle CenterX=0 CenterY=0 CenterZ=0 NormalX=0 NormalY=0 NormalZ=1 AngleXU=0 Radius=1
  constraints (2):
    c: Coincident(g0,g-1)
    c: Diameter(g0) = 2
FEATURE [PartDesign::Pocket] Pocket123
  BaseFeature = -> Pad076
  Direction = (1,-7e-16,3e-16)
  Length = 5
  Length2 = 5
  Placement = pos=(0,0,0) rot=(0.57735,0.57735,0.57735;2.0944rad)
  Profile = -> Sketch253
  ReferenceAxis = -> Sketch253 [N_Axis]
  Type = 1
FEATURE [PartDesign::Body] Body046  label="Kicker plate"
  Group = -> [Sketch109,Pad076,Sketch253,Pocket123]
  Origin = -> Origin251
  Placement = pos=(-71,0,-8) rot=(0,0,1;0rad)
  Tip = -> Pocket123
FEATURE [Sketcher::SketchObject] Sketch254
  FullyConstrained = true
  MapMode = 5
  Placement = pos=(0,50,-1e-16) rot=(-1,0,0;1.5708rad)
  Support = -> [Pad058]
  sketch-geometry (1):
    g0: Circle CenterX=0 CenterY=0 CenterZ=0 NormalX=0 NormalY=0 NormalZ=1 AngleXU=0 Radius=2
  constraints (2):
    c: Coincident(g0,g-1)
    c: Diameter(g0) = 4
FEATURE [PartDesign::Pad] Pad097
  BaseFeature = -> Pad058
  Direction = (0,1,2e-16)
  Length = 17.5
  Length2 = 10
  Placement = pos=(0,0,0) rot=(1,0,0;1.5708rad)
  Profile = -> Sketch254
  ReferenceAxis = -> Sketch254 [N_Axis]
  Type = 0
FEATURE [PartDesign::Body] Body034  label="Dribbler motor"
  Group = -> [Sketch082,Pad058,Sketch254,Pad097]
  Origin = -> Origin237
  Placement = pos=(-48.5,35,17.9) rot=(0.707107,0,0.707107;3.14159rad)
  Tip = -> Pad097
FEATURE [PartDesign::SubShapeBinder] Binder051
  BindCopyOnChange = 0
  BindMode = 0
  ClaimChildren = false
  Context = -> Part011 [Body050.Binder051.]
  Fuse = false
  MakeFace = true
  OffsetFill = false
  OffsetIntersection = false
  OffsetJoinType = 0
  OffsetOpenResult = false
  PartialLoad = false
  Relative = true
  Support = -> [Part013[Body049.Pocket108.Sketch137.]]
  _Version = 2
FEATURE [PartDesign::Pocket] Pocket124
  BaseFeature = -> PolarPattern018
  Direction = (-8e-16,-4e-16,-1)
  Length = 5
  Length2 = 5
  Placement = pos=(0,0,0) rot=(1,0,0;1.5708rad)
  Profile = -> Binder051
  Type = 1
FEATURE [PartDesign::Body] Body050  label="Dribbler support"
  Group = -> [Sketch121,Pad085,Sketch122,Pad086,Sketch123,Pocket048,Sketch124,Pocket049,PolarPattern018,Binder051,Pocket124]
  Origin = -> Origin255
  Placement = pos=(-48.5401,-17.9599,18) rot=(1,0,0;3.14159rad)
  Tip = -> Pocket124
FEATURE [Part::Feature] Part__Feature1908  label="HC05_Pcb"
  Placement = pos=(14.7308,31.0562,28.3016) rot=(-1,0,0;1.5708rad)
  shape: bbox 35.75 x 1.502 x 15.75 mm, 1080 faces (baked)
FEATURE [Part::Feature] Part__Feature1909  label="HC05_06"
  Placement = pos=(6.11873,45.8979,22.3358) rot=(-1,0,0;1.5708rad)
  shape: bbox 27.01 x 1.902 x 13.01 mm, 1526 faces (baked)
FEATURE [Part::Feature] Part__Feature1938  label="QSMD7.0x5.0x1.3"
  Placement = pos=(4.0775,46.698,26.3896) rot=(0,0,1;0rad)
  shape: bbox 3.51 x 0.8001 x 2 mm, 196 faces (baked)
FEATURE [App::Part] HC05_06  label="HC05_007"
  Group = -> [Part__Feature1909,Part__Feature1938]
  Origin = -> Origin347
  Placement = pos=(4.98703,-13.3397,5.96586) rot=(0,0,1;0rad)
FEATURE [Part::Feature] Part__Feature1939  label="Pines_90"
  Placement = pos=(31.1058,32.5572,34.6516) rot=(0,1,0;1.5708rad)
  shape: bbox 8.54 x 9.358 x 2.54 mm, 44 faces (baked)
FEATURE [Part::Feature] Part__Feature1940  label="Pines_091"
  Placement = pos=(31.1058,32.5572,34.6516) rot=(0,1,0;1.5708rad)
  shape: bbox 8.54 x 9.358 x 2.54 mm, 44 faces (baked)
FEATURE [Part::Feature] Part__Feature1941  label="Pines_092"
  Placement = pos=(31.1058,32.5572,34.6516) rot=(0,1,0;1.5708rad)
  shape: bbox 8.54 x 9.358 x 2.34 mm, 40 faces (baked)
FEATURE [Part::Feature] Part__Feature1942  label="Pines_093"
  Placement = pos=(31.1058,32.5572,34.6516) rot=(0,1,0;1.5708rad)
  shape: bbox 8.54 x 9.358 x 2.54 mm, 44 faces (baked)
FEATURE [Part::Feature] Part__Feature1943  label="Pines_094"
  Placement = pos=(31.1058,32.5572,34.6516) rot=(0,1,0;1.5708rad)
  shape: bbox 8.54 x 9.358 x 2.54 mm, 44 faces (baked)
FEATURE [Part::Feature] Part__Feature1944  label="Pines_095"
  Placement = pos=(31.1058,32.5572,34.6516) rot=(0,1,0;1.5708rad)
  shape: bbox 8.54 x 9.358 x 2.54 mm, 44 faces (baked)
FEATURE [App::Part] Pines_90  label="Pines_096"
  Group = -> [Part__Feature1939,Part__Feature1940,Part__Feature1941,Part__Feature1942,Part__Feature1943,Part__Feature1944]
  Origin = -> Origin348
FEATURE [Part::Feature] Part__Feature1968  label="Pulsador_Smd"
  Placement = pos=(27.6199,32.5662,22.084) rot=(0,0.707107,0.707107;3.14159rad)
  shape: bbox 3.92 x 1.91 x 2.9 mm, 86 faces (baked)
FEATURE [App::Part] HC05_Modulo  label="Module HC-05"
  Group = -> [Part__Feature1908,HC05_06,Pines_90,Part__Feature1968]
  Origin = -> Origin354
  Placement = pos=(-20.2898,-34.483,-9) rot=(1,0,0;1.5708rad)
FEATURE [Sketcher::SketchObject] Sketch256
  ExternalGeometry = -> [Pad095]
  FullyConstrained = true
  MapMode = 5
  Placement = pos=(0,0,0) rot=(1,0,0;3.14159rad)
  Support = -> [Pad095]
  sketch-geometry (4):
    g0: Circle CenterX=31.7128 CenterY=0 CenterZ=0 NormalX=0 NormalY=0 NormalZ=1 AngleXU=0 Radius=1.5
    g1: Circle CenterX=-31.7128 CenterY=0 CenterZ=0 NormalX=0 NormalY=0 NormalZ=1 AngleXU=0 Radius=1.5
    g2: LineSegment StartX=31.7128 StartY=0 StartZ=0 EndX=35.7128 EndY=4 EndZ=0
    g3: LineSegment StartX=31.7128 StartY=0 StartZ=0 EndX=35.7128 EndY=-4 EndZ=0
  constraints (9):
    c: PointOnObject(g0,g-1)
    c: Diameter(g0) = 3
    c: Diameter(g1) = 3
    c: Symmetric(g1,g0,g-2)
    c: Coincident(g2,g0)
    c: Coincident(g2,g-3)
    c: Coincident(g3,g0)
    c: Coincident(g3,g-3)
    c: Perpendicular(g3,g2)
FEATURE [PartDesign::Pocket] Pocket125
  BaseFeature = -> Pad095
  Direction = (0,0,1)
  Length = 5
  Length2 = 5
  Profile = -> Sketch256
  ReferenceAxis = -> Sketch256 [N_Axis]
  Type = 1
FEATURE [PartDesign::Body] Body007  label="Mirror base"
  Group = -> [Sketch023,Pad007,Sketch251,Pad095,Sketch256,Pocket125]
  Origin = -> Origin024
  Placement = pos=(0,0,56) rot=(0,0,1;0rad)
  Tip = -> Pocket125
FEATURE [PartDesign::SubShapeBinder] Binder052
  BindCopyOnChange = 0
  BindMode = 0
  ClaimChildren = false
  Context = -> Part015 [Body025.Binder052.]
  Fuse = false
  MakeFace = true
  OffsetFill = false
  OffsetIntersection = false
  OffsetJoinType = 0
  OffsetOpenResult = false
  PartialLoad = false
  Relative = true
  Support = -> [Part001[Body007.Pocket125.Sketch256.]]
  _Version = 2
FEATURE [PartDesign::Pocket] Pocket126
  BaseFeature = -> Pocket112
  Direction = (2e-16,0,-1)
  Length = 5
  Length2 = 5
  Profile = -> Binder052
  Type = 1
FEATURE [PartDesign::Body] Body025  label="Support camera "
  Group = -> [Sketch065,Pad044,Binder010,Pocket052,Sketch249,Pad093,Sketch250,Pocket112,Binder052,Pocket126]
  Origin = -> Origin226
  Placement = pos=(0,0,1) rot=(0,0,1;0rad)
  Tip = -> Pocket126
FEATURE [App::Part] Part015  label="Camera"
  Group = -> [rt10,Body025]
  Origin = -> Origin342
  Placement = pos=(36.22,-17.79,57) rot=(0,0,-1;4.71239rad)
FEATURE [PartDesign::SubShapeBinder] Binder053
  BindCopyOnChange = 0
  BindMode = 0
  ClaimChildren = false
  Context = -> Part012 [Body003.Binder053.]
  Fuse = false
  MakeFace = true
  OffsetFill = false
  OffsetIntersection = false
  OffsetJoinType = 0
  OffsetOpenResult = false
  PartialLoad = false
  Relative = true
  Support = -> [Part015[Body025.Pocket112.Sketch250.]]
  _Version = 2
FEATURE [PartDesign::Pocket] Pocket127
  BaseFeature = -> Pocket121
  Direction = (-2e-16,0,-1)
  Length = 60
  Length2 = 5
  Placement = pos=(0,0,0) rot=(1,0,0;1.5708rad)
  Profile = -> Binder053
  Type = 0
FEATURE [PartDesign::Body] Body003  label="Outer shielding 1"
  Group = -> [Sketch016,Revolution001,Binder047,Pocket121,Binder053,Pocket127]
  Origin = -> Origin016
  Placement = pos=(1e-15,3,0) rot=(0,0,1;1.5708rad)
  Tip = -> Pocket127
FEATURE [App::Part] Part012  label="Shielding"
  Group = -> [Body003,Body051,Body052]
  Origin = -> Origin247
FEATURE [PartDesign::SubShapeBinder] Binder054
  BindCopyOnChange = 0
  BindMode = 0
  ClaimChildren = false
  Context = -> Body [Binder054.]
  Fuse = false
  MakeFace = true
  OffsetFill = false
  OffsetIntersection = false
  OffsetJoinType = 0
  OffsetOpenResult = false
  PartialLoad = false
  Relative = true
  Support = -> [Part015[Body025.Pocket112.Sketch250.]]
  _Version = 2
FEATURE [PartDesign::Pocket] Pocket128
  BaseFeature = -> Pocket122
  Direction = (-2e-16,-2e-16,-1)
  Length = 5
  Length2 = 5
  Profile = -> Binder054
  Type = 1
FEATURE [PartDesign::Body] Body  label="Main plate"
  Group = -> [Sketch,Pad,Sketch001,Pocket,PolarPattern,Sketch015,Pocket004,Sketch061,Pocket019,Binder,Pocket031,Binder005,Pocket038,Binder006,Pocket039,Binder007,Pocket040,Binder008,Pocket050,Sketch126,Pocket055,PolarPattern021,PolarPattern022,Binder032,Pocket101,Binder034,Pocket103,Binder038,Pocket109,Binder050,Pocket122,Binder054,Pocket128]
  Origin = -> Origin008
  Placement = pos=(0,0,-1) rot=(0,0,1;0.785398rad)
  Tip = -> Pocket128
FEATURE [Sketcher::SketchObject] Sketch077
  FullyConstrained = true
  MapMode = 5
  Support = -> [XY_Plane232]
  sketch-geometry (1):
    g0: Circle CenterX=0 CenterY=0 CenterZ=0 NormalX=0 NormalY=0 NormalZ=1 AngleXU=0 Radius=12
  constraints (2):
    c: Diameter(g0) = 24
    c: Coincident(g0,g-1)
FEATURE [PartDesign::Pad] Pad054
  Direction = (0,0,1)
  Length = 56.5
  Length2 = 28.25
  Profile = -> Sketch077
  ReferenceAxis = -> Sketch077 [N_Axis]
  Type = 0
FEATURE [Sketcher::SketchObject] Sketch257
  FullyConstrained = true
  MapMode = 5
  Placement = pos=(0,0,0) rot=(1,0,0;3.14159rad)
  Support = -> [Pad052]
  sketch-geometry (1):
    g0: Circle CenterX=0 CenterY=0 CenterZ=0 NormalX=0 NormalY=0 NormalZ=1 AngleXU=0 Radius=2
  constraints (2):
    c: Coincident(g0,g-1)
    c: Diameter(g0) = 4
FEATURE [PartDesign::Pad] Pad099
  BaseFeature = -> Pad052
  Direction = (0,0,-1)
  Length = 17.5
  Length2 = 10
  Profile = -> Sketch257
  ReferenceAxis = -> Sketch257 [N_Axis]
  Type = 0
FEATURE [PartDesign::Body] Body029  label="Moteur 1"
  Group = -> [Sketch075,Pad052,Sketch257,Pad099]
  Origin = -> Origin230
  Placement = pos=(-41.8711,59.7981,-2) rot=(-0.217607,0.690162,-0.690162;2.71306rad)
  Tip = -> Pad099
FEATURE [Sketcher::SketchObject] Sketch258
  FullyConstrained = true
  MapMode = 5
  Placement = pos=(0,0,0) rot=(1,0,0;3.14159rad)
  Support = -> [Pad054]
  sketch-geometry (1):
    g0: Circle CenterX=0 CenterY=0 CenterZ=0 NormalX=0 NormalY=0 NormalZ=1 AngleXU=0 Radius=2
  constraints (2):
    c: Coincident(g0,g-1)
    c: Diameter(g0) = 4
FEATURE [PartDesign::Pad] Pad100
  BaseFeature = -> Pad054
  Direction = (0,0,-1)
  Length = 17.5
  Length2 = 10
  Profile = -> Sketch258
  ReferenceAxis = -> Sketch258 [N_Axis]
  Type = 0
FEATURE [PartDesign::Body] Body031  label="Moteur 2"
  Group = -> [Sketch077,Pad054,Sketch258,Pad100]
  Origin = -> Origin232
  Placement = pos=(41.8711,59.7981,-8) rot=(0.913318,-0.287968,-0.287968;1.66134rad)
  Tip = -> Pad100
FEATURE [Sketcher::SketchObject] Sketch259
  FullyConstrained = true
  MapMode = 5
  Placement = pos=(0,0,0) rot=(1,0,0;3.14159rad)
  Support = -> [Pad051]
  sketch-geometry (1):
    g0: Circle CenterX=0 CenterY=0 CenterZ=0 NormalX=0 NormalY=0 NormalZ=1 AngleXU=0 Radius=2
  constraints (2):
    c: Coincident(g0,g-1)
    c: Diameter(g0) = 4
FEATURE [PartDesign::Pad] Pad101
  BaseFeature = -> Pad051
  Direction = (0,0,-1)
  Length = 17.5
  Length2 = 10
  Profile = -> Sketch259
  ReferenceAxis = -> Sketch259 [N_Axis]
  Type = 0
FEATURE [PartDesign::Body] Body028  label="Moteur 4"
  Group = -> [Sketch074,Pad051,Sketch259,Pad101]
  Origin = -> Origin229
  Placement = pos=(-41.8711,-59.7981,-8) rot=(-0.913318,0.287968,-0.287968;1.66134rad)
  Tip = -> Pad101
FEATURE [Sketcher::SketchObject] Sketch260
  FullyConstrained = true
  MapMode = 5
  Placement = pos=(0,0,0) rot=(1,0,0;3.14159rad)
  Support = -> [Pad057]
  sketch-geometry (1):
    g0: Circle CenterX=0 CenterY=0 CenterZ=0 NormalX=0 NormalY=0 NormalZ=1 AngleXU=0 Radius=2
  constraints (2):
    c: Coincident(g0,g-1)
    c: Diameter(g0) = 4
FEATURE [PartDesign::Pad] Pad102
  BaseFeature = -> Pad057
  Direction = (0,0,-1)
  Length = 17.5
  Length2 = 10
  Profile = -> Sketch260
  ReferenceAxis = -> Sketch260 [N_Axis]
  Type = 0
FEATURE [PartDesign::Body] Body033  label="Moteur 3"
  Group = -> [Sketch081,Pad057,Sketch260,Pad102]
  Origin = -> Origin235
  Placement = pos=(41.8711,-59.7981,-8) rot=(-0.913318,-0.287968,0.287968;1.66134rad)
  Tip = -> Pad102
FEATURE [Sketcher::SketchObject] Sketch261
  FullyConstrained = true
  MapMode = 5
  Support = -> [XY_Plane357]
  sketch-geometry (1):
    g0: Circle CenterX=0 CenterY=0 CenterZ=0 NormalX=0 NormalY=0 NormalZ=1 AngleXU=0 Radius=17.5
  constraints (2):
    c: Coincident(g0,g-1)
    c: Diameter(g0) = 35
FEATURE [PartDesign::Pad] Pad103
  Direction = (0,0,1)
  Length = 12
  Length2 = 10
  Profile = -> Sketch261
  ReferenceAxis = -> Sketch261 [N_Axis]
  Type = 0
FEATURE [PartDesign::Body] Body095  label="Corps"
  Group = -> [Sketch261,Pad103]
  Origin = -> Origin357
  Placement = pos=(0,0,24) rot=(0,0,1;0rad)
  Tip = -> Pad103
FEATURE [App::Part] LD19  label="LIDAR LD19"
  Group = -> [Part__Feature1464,Part__Feature1465,Part__Feature1466,Body095]
  Origin = -> Origin258
  Placement = pos=(0,0,13) rot=(0,0,-1;4.71239rad)
FEATURE [Sketcher::SketchObject] Sketch262
  FullyConstrained = false
  MapMode = 5
  Placement = pos=(0,0,0) rot=(0.57735,0.57735,0.57735;2.0944rad)
  Support = -> [YZ_Plane009]
  sketch-geometry (2):
    g0: LineSegment StartX=0 StartY=75.6915 StartZ=0 EndX=-25.0741 EndY=123.858 EndZ=0
    g1: LineSegment StartX=0 StartY=75.6915 StartZ=0 EndX=25.0741 EndY=123.858 EndZ=0
  constraints (4):
    c: PointOnObject(g0,g-2)
    c: Coincident(g1,g0)
    c: Symmetric(g0,g1,g-2)
    c: Angle(g1,g0) = 0.959931
FEATURE [Part::Feature] Part__Feature1973  label="OmniBase_Predeterminado007"
  Placement = pos=(4.80373,-0.638646,40.5) rot=(0,0,1;0rad)
  shape: bbox 44 x 43.9 x 9 mm, 104 faces (baked)
FEATURE [Part::Feature] Part__Feature1974  label="Roller_Predeterminado126"
  Placement = pos=(4.80373,20.3614,41.6192) rot=(0,0,1;0rad)
  shape: bbox 2.6 x 8.659 x 8.659 mm, 10 faces (baked)
FEATURE [Part::Feature] Part__Feature1975  label="Roller_Predeterminado127"
  Placement = pos=(-2.3787,19.0949,41.6192) rot=(0,0,1;0.349066rad)
  shape: bbox 4.664 x 8.342 x 8.659 mm, 10 faces (baked)
FEATURE [Part::Feature] Part__Feature1976  label="Roller_Predeterminado128"
  Placement = pos=(-8.69481,15.4483,41.6192) rot=(0,0,1;0.698132rad)
  shape: bbox 6.71 x 7.451 x 8.659 mm, 10 faces (baked)
FEATURE [Part::Feature] Part__Feature1977  label="Roller_Predeterminado129"
  Placement = pos=(-13.3828,9.86135,41.6192) rot=(0,0,1;1.0472rad)
  shape: bbox 7.965 x 5.765 x 8.659 mm, 10 faces (baked)
FEATURE [Part::Feature] Part__Feature1978  label="Roller_Predeterminado130"
  Placement = pos=(-15.8772,3.00797,41.6192) rot=(0,0,1;1.39626rad)
  shape: bbox 8.632 x 3.688 x 8.659 mm, 10 faces (baked)
FEATURE [Part::Feature] Part__Feature1979  label="Roller_Predeterminado131"
  Placement = pos=(-15.8772,-4.28526,41.6192) rot=(0,0,1;1.74533rad)
  shape: bbox 8.632 x 3.688 x 8.659 mm, 10 faces (baked)
FEATURE [Part::Feature] Part__Feature1980  label="Roller_Predeterminado132"
  Placement = pos=(-13.3828,-11.1386,41.6192) rot=(0,0,1;2.0944rad)
  shape: bbox 7.965 x 5.765 x 8.659 mm, 10 faces (baked)
FEATURE [Part::Feature] Part__Feature1981  label="Roller_Predeterminado133"
  Placement = pos=(-8.69481,-16.7256,41.6192) rot=(0,0,1;2.44346rad)
  shape: bbox 6.71 x 7.451 x 8.659 mm, 10 faces (baked)
FEATURE [Part::Feature] Part__Feature1982  label="Roller_Predeterminado134"
  Placement = pos=(-2.3787,-20.3722,41.6192) rot=(0,0,1;2.79253rad)
  shape: bbox 4.664 x 8.342 x 8.659 mm, 10 faces (baked)
FEATURE [Part::Feature] Part__Feature1983  label="Roller_Predeterminado135"
  Placement = pos=(4.80373,-21.6386,41.6192) rot=(0,0,1;3.14159rad)
  shape: bbox 2.6 x 8.659 x 8.659 mm, 10 faces (baked)
FEATURE [Part::Feature] Part__Feature1984  label="Roller_Predeterminado136"
  Placement = pos=(11.9862,-20.3722,41.6192) rot=(0,0,1;3.49066rad)
  shape: bbox 4.664 x 8.342 x 8.659 mm, 10 faces (baked)
FEATURE [Part::Feature] Part__Feature1985  label="Roller_Predeterminado137"
  Placement = pos=(18.3023,-16.7256,41.6192) rot=(0,0,1;3.83972rad)
  shape: bbox 6.71 x 7.451 x 8.659 mm, 10 faces (baked)
FEATURE [Part::Feature] Part__Feature1986  label="Roller_Predeterminado138"
  Placement = pos=(22.9903,-11.1386,41.6192) rot=(0,0,-1;2.0944rad)
  shape: bbox 7.965 x 5.765 x 8.659 mm, 10 faces (baked)
FEATURE [Part::Feature] Part__Feature1987  label="Roller_Predeterminado139"
  Placement = pos=(25.4847,-4.28526,41.6192) rot=(0,0,-1;1.74533rad)
  shape: bbox 8.632 x 3.688 x 8.659 mm, 10 faces (baked)
FEATURE [Part::Feature] Part__Feature1988  label="Roller_Predeterminado140"
  Placement = pos=(25.4847,3.00797,41.6192) rot=(0,0,-1;1.39626rad)
  shape: bbox 8.632 x 3.688 x 8.659 mm, 10 faces (baked)
FEATURE [Part::Feature] Part__Feature1989  label="Roller_Predeterminado141"
  Placement = pos=(22.9903,9.86135,41.6192) rot=(0,0,-1;1.0472rad)
  shape: bbox 7.965 x 5.765 x 8.659 mm, 10 faces (baked)
FEATURE [Part::Feature] Part__Feature1990  label="Roller_Predeterminado142"
  Placement = pos=(18.3023,15.4483,41.6192) rot=(0,0,-1;0.698132rad)
  shape: bbox 6.71 x 7.451 x 8.659 mm, 10 faces (baked)
FEATURE [Part::Feature] Part__Feature1991  label="Roller_Predeterminado143"
  Placement = pos=(11.9862,19.0949,41.6192) rot=(0,0,-1;0.349066rad)
  shape: bbox 4.664 x 8.342 x 8.659 mm, 10 faces (baked)
FEATURE [Part::Feature] Part__Feature1992  label="Nut_Predeterminado007"
  Placement = pos=(4.80373,-0.638646,43.5) rot=(0,0,1;1.0472rad)
  shape: bbox 13.86 x 12.93 x 2 mm, 24 faces (baked)
FEATURE [App::Part] OmniWheel057  label="OmniWheel 2"
  Group = -> [Part__Feature1973,Part__Feature1974,Part__Feature1975,Part__Feature1976,Part__Feature1977,Part__Feature1978,Part__Feature1979,Part__Feature1980,Part__Feature1981,Part__Feature1982,Part__Feature1983,Part__Feature1984,Part__Feature1985,Part__Feature1986,Part__Feature1987,Part__Feature1988,Part__Feature1989,Part__Feature1990,Part__Feature1991,Part__Feature1992]
  Origin = -> Origin358
  Placement = pos=(20.4451,37.5671,-8.7) rot=(-0.913318,0.287968,-0.287968;1.66134rad)
FEATURE [App::Part] Part006  label="Motor assembly 2"
  Group = -> [Body031,Body039,OmniWheel057]
  Origin = -> Origin039
  Placement = pos=(1,-4,0) rot=(0,0,-1;6.24828rad)
FEATURE [Part::Feature] Part__Feature1993  label="OmniBase_Predeterminado008"
  Placement = pos=(4.80373,-0.638646,40.5) rot=(0,0,1;0rad)
  shape: bbox 44 x 43.9 x 9 mm, 104 faces (baked)
FEATURE [Part::Feature] Part__Feature1994  label="Roller_Predeterminado144"
  Placement = pos=(4.80373,20.3614,41.6192) rot=(0,0,1;0rad)
  shape: bbox 2.6 x 8.659 x 8.659 mm, 10 faces (baked)
FEATURE [Part::Feature] Part__Feature1995  label="Roller_Predeterminado145"
  Placement = pos=(-2.3787,19.0949,41.6192) rot=(0,0,1;0.349066rad)
  shape: bbox 4.664 x 8.342 x 8.659 mm, 10 faces (baked)
FEATURE [Part::Feature] Part__Feature1996  label="Roller_Predeterminado146"
  Placement = pos=(-8.69481,15.4483,41.6192) rot=(0,0,1;0.698132rad)
  shape: bbox 6.71 x 7.451 x 8.659 mm, 10 faces (baked)
FEATURE [Part::Feature] Part__Feature1997  label="Roller_Predeterminado147"
  Placement = pos=(-13.3828,9.86135,41.6192) rot=(0,0,1;1.0472rad)
  shape: bbox 7.965 x 5.765 x 8.659 mm, 10 faces (baked)
FEATURE [Part::Feature] Part__Feature1998  label="Roller_Predeterminado148"
  Placement = pos=(-15.8772,3.00797,41.6192) rot=(0,0,1;1.39626rad)
  shape: bbox 8.632 x 3.688 x 8.659 mm, 10 faces (baked)
FEATURE [Part::Feature] Part__Feature1999  label="Roller_Predeterminado149"
  Placement = pos=(-15.8772,-4.28526,41.6192) rot=(0,0,1;1.74533rad)
  shape: bbox 8.632 x 3.688 x 8.659 mm, 10 faces (baked)
FEATURE [Part::Feature] Part__Feature2000  label="Roller_Predeterminado150"
  Placement = pos=(-13.3828,-11.1386,41.6192) rot=(0,0,1;2.0944rad)
  shape: bbox 7.965 x 5.765 x 8.659 mm, 10 faces (baked)
FEATURE [Part::Feature] Part__Feature2001  label="Roller_Predeterminado151"
  Placement = pos=(-8.69481,-16.7256,41.6192) rot=(0,0,1;2.44346rad)
  shape: bbox 6.71 x 7.451 x 8.659 mm, 10 faces (baked)
FEATURE [Part::Feature] Part__Feature2002  label="Roller_Predeterminado152"
  Placement = pos=(-2.3787,-20.3722,41.6192) rot=(0,0,1;2.79253rad)
  shape: bbox 4.664 x 8.342 x 8.659 mm, 10 faces (baked)
FEATURE [Part::Feature] Part__Feature2003  label="Roller_Predeterminado153"
  Placement = pos=(4.80373,-21.6386,41.6192) rot=(0,0,1;3.14159rad)
  shape: bbox 2.6 x 8.659 x 8.659 mm, 10 faces (baked)
FEATURE [Part::Feature] Part__Feature2004  label="Roller_Predeterminado154"
  Placement = pos=(11.9862,-20.3722,41.6192) rot=(0,0,1;3.49066rad)
  shape: bbox 4.664 x 8.342 x 8.659 mm, 10 faces (baked)
FEATURE [Part::Feature] Part__Feature2005  label="Roller_Predeterminado155"
  Placement = pos=(18.3023,-16.7256,41.6192) rot=(0,0,1;3.83972rad)
  shape: bbox 6.71 x 7.451 x 8.659 mm, 10 faces (baked)
FEATURE [Part::Feature] Part__Feature2006  label="Roller_Predeterminado156"
  Placement = pos=(22.9903,-11.1386,41.6192) rot=(0,0,-1;2.0944rad)
  shape: bbox 7.965 x 5.765 x 8.659 mm, 10 faces (baked)
FEATURE [Part::Feature] Part__Feature2007  label="Roller_Predeterminado157"
  Placement = pos=(25.4847,-4.28526,41.6192) rot=(0,0,-1;1.74533rad)
  shape: bbox 8.632 x 3.688 x 8.659 mm, 10 faces (baked)
FEATURE [Part::Feature] Part__Feature2008  label="Roller_Predeterminado158"
  Placement = pos=(25.4847,3.00797,41.6192) rot=(0,0,-1;1.39626rad)
  shape: bbox 8.632 x 3.688 x 8.659 mm, 10 faces (baked)
FEATURE [Part::Feature] Part__Feature2009  label="Roller_Predeterminado159"
  Placement = pos=(22.9903,9.86135,41.6192) rot=(0,0,-1;1.0472rad)
  shape: bbox 7.965 x 5.765 x 8.659 mm, 10 faces (baked)
FEATURE [Part::Feature] Part__Feature2010  label="Roller_Predeterminado160"
  Placement = pos=(18.3023,15.4483,41.6192) rot=(0,0,-1;0.698132rad)
  shape: bbox 6.71 x 7.451 x 8.659 mm, 10 faces (baked)
FEATURE [Part::Feature] Part__Feature2011  label="Roller_Predeterminado161"
  Placement = pos=(11.9862,19.0949,41.6192) rot=(0,0,-1;0.349066rad)
  shape: bbox 4.664 x 8.342 x 8.659 mm, 10 faces (baked)
FEATURE [Part::Feature] Part__Feature2012  label="Nut_Predeterminado008"
  Placement = pos=(4.80373,-0.638646,43.5) rot=(0,0,1;1.0472rad)
  shape: bbox 13.86 x 12.93 x 2 mm, 24 faces (baked)
FEATURE [App::Part] OmniWheel058  label="OmniWheel 3"
  Group = -> [Part__Feature1993,Part__Feature1994,Part__Feature1995,Part__Feature1996,Part__Feature1997,Part__Feature1998,Part__Feature1999,Part__Feature2000,Part__Feature2001,Part__Feature2002,Part__Feature2003,Part__Feature2004,Part__Feature2005,Part__Feature2006,Part__Feature2007,Part__Feature2008,Part__Feature2009,Part__Feature2010,Part__Feature2011,Part__Feature2012]
  Origin = -> Origin359
  Placement = pos=(20.4451,-37.5671,-7.4) rot=(0.913318,0.287968,0.287968;1.66134rad)
FEATURE [App::Part] Part007  label="Motor assembly 3"
  Group = -> [Body033,Body040,OmniWheel058]
  Origin = -> Origin040
  Placement = pos=(1,4,0) rot=(0,0,1;6.24828rad)
FEATURE [Part::Feature] Part__Feature2013  label="OmniBase_Predeterminado009"
  Placement = pos=(4.80373,-0.638646,40.5) rot=(0,0,1;0rad)
  shape: bbox 44 x 43.9 x 9 mm, 104 faces (baked)
FEATURE [Part::Feature] Part__Feature2014  label="Roller_Predeterminado162"
  Placement = pos=(4.80373,20.3614,41.6192) rot=(0,0,1;0rad)
  shape: bbox 2.6 x 8.659 x 8.659 mm, 10 faces (baked)
FEATURE [Part::Feature] Part__Feature2015  label="Roller_Predeterminado163"
  Placement = pos=(-2.3787,19.0949,41.6192) rot=(0,0,1;0.349066rad)
  shape: bbox 4.664 x 8.342 x 8.659 mm, 10 faces (baked)
FEATURE [Part::Feature] Part__Feature2016  label="Roller_Predeterminado164"
  Placement = pos=(-8.69481,15.4483,41.6192) rot=(0,0,1;0.698132rad)
  shape: bbox 6.71 x 7.451 x 8.659 mm, 10 faces (baked)
FEATURE [Part::Feature] Part__Feature2017  label="Roller_Predeterminado165"
  Placement = pos=(-13.3828,9.86135,41.6192) rot=(0,0,1;1.0472rad)
  shape: bbox 7.965 x 5.765 x 8.659 mm, 10 faces (baked)
FEATURE [Part::Feature] Part__Feature2018  label="Roller_Predeterminado166"
  Placement = pos=(-15.8772,3.00797,41.6192) rot=(0,0,1;1.39626rad)
  shape: bbox 8.632 x 3.688 x 8.659 mm, 10 faces (baked)
FEATURE [Part::Feature] Part__Feature2019  label="Roller_Predeterminado167"
  Placement = pos=(-15.8772,-4.28526,41.6192) rot=(0,0,1;1.74533rad)
  shape: bbox 8.632 x 3.688 x 8.659 mm, 10 faces (baked)
FEATURE [Part::Feature] Part__Feature2020  label="Roller_Predeterminado168"
  Placement = pos=(-13.3828,-11.1386,41.6192) rot=(0,0,1;2.0944rad)
  shape: bbox 7.965 x 5.765 x 8.659 mm, 10 faces (baked)
FEATURE [Part::Feature] Part__Feature2021  label="Roller_Predeterminado169"
  Placement = pos=(-8.69481,-16.7256,41.6192) rot=(0,0,1;2.44346rad)
  shape: bbox 6.71 x 7.451 x 8.659 mm, 10 faces (baked)
FEATURE [Part::Feature] Part__Feature2022  label="Roller_Predeterminado170"
  Placement = pos=(-2.3787,-20.3722,41.6192) rot=(0,0,1;2.79253rad)
  shape: bbox 4.664 x 8.342 x 8.659 mm, 10 faces (baked)
FEATURE [Part::Feature] Part__Feature2023  label="Roller_Predeterminado171"
  Placement = pos=(4.80373,-21.6386,41.6192) rot=(0,0,1;3.14159rad)
  shape: bbox 2.6 x 8.659 x 8.659 mm, 10 faces (baked)
FEATURE [Part::Feature] Part__Feature2024  label="Roller_Predeterminado172"
  Placement = pos=(11.9862,-20.3722,41.6192) rot=(0,0,1;3.49066rad)
  shape: bbox 4.664 x 8.342 x 8.659 mm, 10 faces (baked)
FEATURE [Part::Feature] Part__Feature2025  label="Roller_Predeterminado173"
  Placement = pos=(18.3023,-16.7256,41.6192) rot=(0,0,1;3.83972rad)
  shape: bbox 6.71 x 7.451 x 8.659 mm, 10 faces (baked)
FEATURE [Part::Feature] Part__Feature2026  label="Roller_Predeterminado174"
  Placement = pos=(22.9903,-11.1386,41.6192) rot=(0,0,-1;2.0944rad)
  shape: bbox 7.965 x 5.765 x 8.659 mm, 10 faces (baked)
FEATURE [Part::Feature] Part__Feature2027  label="Roller_Predeterminado175"
  Placement = pos=(25.4847,-4.28526,41.6192) rot=(0,0,-1;1.74533rad)
  shape: bbox 8.632 x 3.688 x 8.659 mm, 10 faces (baked)
FEATURE [Part::Feature] Part__Feature2028  label="Roller_Predeterminado176"
  Placement = pos=(25.4847,3.00797,41.6192) rot=(0,0,-1;1.39626rad)
  shape: bbox 8.632 x 3.688 x 8.659 mm, 10 faces (baked)
FEATURE [Part::Feature] Part__Feature2029  label="Roller_Predeterminado177"
  Placement = pos=(22.9903,9.86135,41.6192) rot=(0,0,-1;1.0472rad)
  shape: bbox 7.965 x 5.765 x 8.659 mm, 10 faces (baked)
FEATURE [Part::Feature] Part__Feature2030  label="Roller_Predeterminado178"
  Placement = pos=(18.3023,15.4483,41.6192) rot=(0,0,-1;0.698132rad)
  shape: bbox 6.71 x 7.451 x 8.659 mm, 10 faces (baked)
FEATURE [Part::Feature] Part__Feature2031  label="Roller_Predeterminado179"
  Placement = pos=(11.9862,19.0949,41.6192) rot=(0,0,-1;0.349066rad)
  shape: bbox 4.664 x 8.342 x 8.659 mm, 10 faces (baked)
FEATURE [Part::Feature] Part__Feature2032  label="Nut_Predeterminado009"
  Placement = pos=(4.80373,-0.638646,43.5) rot=(0,0,1;1.0472rad)
  shape: bbox 13.86 x 12.93 x 2 mm, 24 faces (baked)
FEATURE [App::Part] OmniWheel059  label="OmniWheel 4"
  Group = -> [Part__Feature2013,Part__Feature2014,Part__Feature2015,Part__Feature2016,Part__Feature2017,Part__Feature2018,Part__Feature2019,Part__Feature2020,Part__Feature2021,Part__Feature2022,Part__Feature2023,Part__Feature2024,Part__Feature2025,Part__Feature2026,Part__Feature2027,Part__Feature2028,Part__Feature2029,Part__Feature2030,Part__Feature2031,Part__Feature2032]
  Origin = -> Origin360
  Placement = pos=(-28.3089,-32.0608,-7.4) rot=(-0.913318,0.287968,0.287968;4.62184rad)
FEATURE [App::Part] Part008  label="Motor assembly 4"
  Group = -> [Body028,Body041,OmniWheel059]
  Origin = -> Origin041
  Placement = pos=(-1,4,0) rot=(0,0,1;0.034907rad)
FEATURE [Sketcher::SketchObject] Sketch263
  ExternalGeometry = -> [PolarPattern012]
  FullyConstrained = true
  MapMode = 5
  Placement = pos=(-13,0,0) rot=(0.707107,0,-0.707107;3.14159rad)
  Support = -> [PolarPattern012]
  sketch-geometry (5):
    g0: LineSegment StartX=0 StartY=0 StartZ=0 EndX=-18 EndY=0 EndZ=0
    g1: LineSegment StartX=-18 StartY=0 StartZ=0 EndX=-18 EndY=20 EndZ=0
    g2: LineSegment StartX=0 StartY=0 StartZ=0 EndX=3.6e-15 EndY=3 EndZ=0
    g3: LineSegment StartX=3.6e-15 StartY=3 StartZ=0 EndX=-14 EndY=20 EndZ=0
    g4: LineSegment StartX=-14 StartY=20 StartZ=0 EndX=-18 EndY=20 EndZ=0
  constraints (12):
    c: Coincident(g0,g-1)
    c: Coincident(g0,g-3)
    c: Coincident(g1,g0)
    c: Vertical(g1)
    c: Coincident(g2,g0)
    c: Coincident(g2,g-4)
    c: Coincident(g3,g2)
    c: Coincident(g4,g3)
    c: Coincident(g4,g1)
    c: Horizontal(g4)
    c: DistanceY(g1,g1) = 20
    c: PointOnObject(g3,g-5)
FEATURE [PartDesign::Pad] Pad104
  BaseFeature = -> PolarPattern012
  Direction = (-1,0,-2e-16)
  Length = 3
  Length2 = 10
  Placement = pos=(0,0,0) rot=(1,0,0;1.5708rad)
  Profile = -> Sketch263
  ReferenceAxis = -> Sketch263 [N_Axis]
  Type = 0
FEATURE [Sketcher::SketchObject] Sketch264
  ExternalGeometry = -> [Pad104]
  FullyConstrained = true
  MapMode = 5
  Placement = pos=(13,0,0) rot=(0.707107,0,0.707107;3.14159rad)
  Support = -> [Pad104]
  sketch-geometry (5):
    g0: LineSegment StartX=0 StartY=0 StartZ=0 EndX=18 EndY=-2e-15 EndZ=0
    g1: LineSegment StartX=18 StartY=-2e-15 StartZ=0 EndX=18 EndY=20 EndZ=0
    g2: LineSegment StartX=0 StartY=0 StartZ=0 EndX=0 EndY=3 EndZ=0
    g3: LineSegment StartX=0 StartY=3 StartZ=0 EndX=14 EndY=20 EndZ=0
    g4: LineSegment StartX=14 StartY=20 StartZ=0 EndX=18 EndY=20 EndZ=0
  constraints (12):
    c: Coincident(g0,g-1)
    c: Coincident(g0,g-5)
    c: Coincident(g1,g0)
    c: Vertical(g1)
    c: Coincident(g2,g0)
    c: Coincident(g2,g-3)
    c: Coincident(g3,g2)
    c: PointOnObject(g3,g-4)
    c: Coincident(g4,g3)
    c: Coincident(g4,g1)
    c: Horizontal(g4)
    c: DistanceY(g1,g1) = 20
FEATURE [PartDesign::Pad] Pad105
  BaseFeature = -> Pad104
  Direction = (1,0,-2e-16)
  Length = 3
  Length2 = 10
  Placement = pos=(0,0,0) rot=(1,0,0;1.5708rad)
  Profile = -> Sketch264
  ReferenceAxis = -> Sketch264 [N_Axis]
  Type = 0
FEATURE [PartDesign::Body] Body038  label="Moteur support 1"
  Group = -> [Sketch084,Pad062,Sketch085,Pad063,Sketch086,Pocket029,Sketch087,Pocket030,PolarPattern012,Sketch263,Pad104,Sketch264,Pad105]
  Origin = -> Origin241
  Placement = pos=(-43.5918,62.2556,-2) rot=(0,0,1;0.610865rad)
  Tip = -> Pad105
FEATURE [App::Part] Part005  label="Motor assembly 1"
  Group = -> [OmniWheel054,Body029,Body038]
  Origin = -> Origin038
  Placement = pos=(-1,-4,-6) rot=(0,0,-1;0.034907rad)
FEATURE [App::Part] Part003  label="Powertrain"
  Group = -> [Part005,Part006,Part007,Part008]
  Origin = -> Origin034
  Placement = pos=(0,0,-11) rot=(0,0,1;0rad)
FEATURE [Sketcher::SketchObject] Sketch021
  FullyConstrained = true
  MapMode = 5
  Support = -> [XY_Plane023]
  sketch-geometry (2):
    g0: Circle CenterX=0 CenterY=0 CenterZ=0 NormalX=0 NormalY=0 NormalZ=1 AngleXU=0 Radius=23
    g1: Circle CenterX=0 CenterY=0 CenterZ=0 NormalX=0 NormalY=0 NormalZ=1 AngleXU=0 Radius=25
  constraints (4):
    c: Coincident(g0,g-1)
    c: Diameter(g0) = 46
    c: Coincident(g1,g0)
    c: Diameter(g1) = 50
FEATURE [PartDesign::Pad] Pad006
  Direction = (0,0,1)
  Length = 63.4
  Length2 = 10
  Profile = -> Sketch021
  ReferenceAxis = -> Sketch021 [N_Axis]
  Reversed = true
  Type = 0
FEATURE [PartDesign::Body] Body006  label="Mirror protection"
  Group = -> [Sketch021,Pad006]
  Origin = -> Origin023
  Placement = pos=(0,0,123.4) rot=(0,0,1;0rad)
  Tip = -> Pad006
FEATURE [Sketcher::SketchObject] Sketch265
  FullyConstrained = true
  MapMode = 5
  Placement = pos=(0,2.71e-14,122) rot=(0,0,1;3.14159rad)
  Support = -> [Revolution]
  sketch-geometry (1):
    g0: Circle CenterX=0 CenterY=0 CenterZ=0 NormalX=0 NormalY=0 NormalZ=1 AngleXU=0 Radius=60
  constraints (2):
    c: Coincident(g0,g-1)
    c: Diameter(g0) = 120
FEATURE [PartDesign::Pad] Pad106
  BaseFeature = -> Revolution
  Direction = (0,-2e-16,1)
  Length = 3
  Length2 = 10
  Placement = pos=(0,0,0) rot=(1,0,0;1.5708rad)
  Profile = -> Sketch265
  ReferenceAxis = -> Sketch265 [N_Axis]
  Type = 0
FEATURE [Sketcher::SketchObject] Sketch266
  FullyConstrained = true
  MapMode = 5
  Placement = pos=(0,-6e-15,125) rot=(0,0,1;3.14159rad)
  Support = -> [Pad106]
  sketch-geometry (5):
    g0: Circle CenterX=0 CenterY=0 CenterZ=0 NormalX=0 NormalY=0 NormalZ=1 AngleXU=0 Radius=3
    g1: Circle CenterX=-32 CenterY=0 CenterZ=0 NormalX=0 NormalY=0 NormalZ=1 AngleXU=0 Radius=3
    g2: Circle CenterX=32 CenterY=0 CenterZ=0 NormalX=0 NormalY=0 NormalZ=1 AngleXU=0 Radius=3
    g3: Circle CenterX=-44 CenterY=0 CenterZ=0 NormalX=0 NormalY=0 NormalZ=1 AngleXU=0 Radius=2
    g4: Circle CenterX=44 CenterY=0 CenterZ=0 NormalX=0 NormalY=0 NormalZ=1 AngleXU=0 Radius=2
  constraints (12):
    c: Coincident(g0,g-1)
    c: Diameter(g0) = 6
    c: PointOnObject(g1,g-1)
    c: Symmetric(g1,g2,g-2)
    c: Diameter(g1) = 6
    c: Diameter(g2) = 6
    c: DistanceX(g1,g0) = 32
    c: PointOnObject(g3,g-1)
    c: Diameter(g3) = 4
    c: Diameter(g4) = 4
    c: DistanceX(g3,g0) = 44
    c: Symmetric(g3,g4,g-2)
FEATURE [PartDesign::Pocket] Pocket129
  BaseFeature = -> Pad106
  Direction = (0,3e-16,-1)
  Length = 3
  Length2 = 5
  Placement = pos=(0,0,0) rot=(1,0,0;1.5708rad)
  Profile = -> Sketch266
  ReferenceAxis = -> Sketch266 [N_Axis]
  Type = 0
FEATURE [Sketcher::SketchObject] Sketch267
  FullyConstrained = true
  MapMode = 5
  Placement = pos=(0,-6e-15,125) rot=(0,0,1;3.14159rad)
  Support = -> [Pocket129]
  sketch-geometry (1):
    g0: Circle CenterX=0 CenterY=0 CenterZ=0 NormalX=0 NormalY=0 NormalZ=1 AngleXU=0 Radius=1.5
  constraints (2):
    c: Coincident(g0,g-1)
    c: Diameter(g0) = 3
FEATURE [PartDesign::Pocket] Pocket130
  BaseFeature = -> Pocket129
  Direction = (0,3e-16,-1)
  Length = 5
  Length2 = 5
  Placement = pos=(0,0,0) rot=(1,0,0;1.5708rad)
  Profile = -> Sketch267
  ReferenceAxis = -> Sketch267 [N_Axis]
  Type = 1
FEATURE [Sketcher::SketchObject] Sketch268
  FullyConstrained = true
  MapMode = 5
  Support = -> [XY_Plane361]
  sketch-geometry (3):
    g0: Circle CenterX=0 CenterY=0 CenterZ=0 NormalX=0 NormalY=0 NormalZ=1 AngleXU=0 Radius=4
    g1: LineSegment StartX=-1.24599 StartY=1.5 StartZ=0 EndX=1.24599 EndY=1.5 EndZ=0
    g2: ArcOfCircle CenterX=0 CenterY=0 CenterZ=0 NormalX=0 NormalY=0 NormalZ=1 AngleXU=0 Radius=1.95 StartAngle=2.26396 EndAngle=7.16082
  constraints (8):
    c: Coincident(g0,g-1)
    c: Diameter(g0) = 8
    c: Horizontal(g1)
    c: Coincident(g2,g0)
    c: Coincident(g2,g1)
    c: Coincident(g2,g1)
    c: Diameter(g2) = 3.9
    c: DistanceY(g0,g1) = 1.5
FEATURE [PartDesign::Pad] Pad107
  Direction = (0,0,1)
  Length = 9.5
  Length2 = 10
  Profile = -> Sketch268
  ReferenceAxis = -> Sketch268 [N_Axis]
  Type = 0
FEATURE [Sketcher::SketchObject] Sketch269
  ExternalGeometry = -> [Pad107]
  FullyConstrained = true
  MapMode = 5
  Placement = pos=(0,0,9.5) rot=(0,0,1;0rad)
  Support = -> [Pad107]
  sketch-geometry (1):
    g0: Circle CenterX=0 CenterY=0 CenterZ=0 NormalX=0 NormalY=0 NormalZ=1 AngleXU=0 Radius=7.5
  constraints (2):
    c: Coincident(g0,g-3)
    c: Diameter(g0) = 15
FEATURE [PartDesign::Pad] Pad108
  BaseFeature = -> Pad107
  Direction = (0,0,1)
  Length = 10
  Length2 = 10
  Profile = -> Sketch269
  ReferenceAxis = -> Sketch269 [N_Axis]
  Type = 0
FEATURE [Sketcher::SketchObject] Sketch270
  FullyConstrained = true
  MapMode = 5
  Placement = pos=(0,0,0) rot=(1,0,0;1.5708rad)
  Support = -> [XZ_Plane361]
  sketch-geometry (1):
    g0: Circle CenterX=0 CenterY=2.5 CenterZ=0 NormalX=0 NormalY=0 NormalZ=1 AngleXU=0 Radius=1.5
  constraints (3):
    c: PointOnObject(g0,g-2)
    c: Diameter(g0) = 3
    c: DistanceY(g-1,g0) = 2.5
FEATURE [PartDesign::Pocket] Pocket131
  BaseFeature = -> Pad108
  Direction = (0,1,2e-16)
  Length = 5
  Length2 = 5
  Profile = -> Sketch270
  ReferenceAxis = -> Sketch270 [N_Axis]
  Type = 1
FEATURE [PartDesign::Body] Body096  label="Adaptateur 1"
  Group = -> [Sketch268,Pad107,Sketch269,Pad108,Sketch270,Pocket131]
  Origin = -> Origin361
  Placement = pos=(-44.5,20.5,19) rot=(0,0.707107,0.707107;3.14159rad)
  Tip = -> Pocket131
FEATURE [Sketcher::SketchObject] Sketch274
  ExternalGeometry = -> [Pocket130]
  FullyConstrained = false
  MapMode = 5
  Placement = pos=(0,-5.9e-15,122) rot=(1,0,0;3.14159rad)
  Support = -> [Pocket130]
  sketch-geometry (14):
    g0: LineSegment StartX=-29.1045 StartY=-0.958487 StartZ=0 EndX=-29.7222 EndY=2.02832 EndZ=0
    g1: LineSegment StartX=-29.7222 StartY=2.02832 StartZ=0 EndX=-32.6177 EndY=2.9868 EndZ=0
    g2: LineSegment StartX=-32.6177 StartY=2.9868 StartZ=0 EndX=-34.8955 EndY=0.958487 EndZ=0
    g3: LineSegment StartX=-34.8955 StartY=0.958487 StartZ=0 EndX=-34.2778 EndY=-2.02832 EndZ=0
    g4: LineSegment StartX=-34.2778 StartY=-2.02832 StartZ=0 EndX=-31.3823 EndY=-2.9868 EndZ=0
    g5: LineSegment StartX=-31.3823 StartY=-2.9868 StartZ=0 EndX=-29.1045 EndY=-0.958487 EndZ=0
    g6: Circle CenterX=-32 CenterY=1.1e-15 CenterZ=0 NormalX=0 NormalY=0 NormalZ=1 AngleXU=0 Radius=3.05
    g7: LineSegment StartX=34.4331 StartY=-1.8391 StartZ=0 EndX=34.8093 EndY=1.18762 EndZ=0
    g8: LineSegment StartX=34.8093 StartY=1.18762 StartZ=0 EndX=32.3761 EndY=3.02672 EndZ=0
    g9: LineSegment StartX=32.3761 StartY=3.02672 StartZ=0 EndX=29.5669 EndY=1.8391 EndZ=0
    g10: LineSegment StartX=29.5669 StartY=1.8391 StartZ=0 EndX=29.1907 EndY=-1.18762 EndZ=0
    g11: LineSegment StartX=29.1907 StartY=-1.18762 StartZ=0 EndX=31.6239 EndY=-3.02672 EndZ=0
    g12: LineSegment StartX=31.6239 StartY=-3.02672 StartZ=0 EndX=34.4331 EndY=-1.8391 EndZ=0
    g13: Circle CenterX=32 CenterY=0 CenterZ=0 NormalX=0 NormalY=0 NormalZ=1 AngleXU=0 Radius=3.05
  constraints (29):
    c: Coincident(g0,g1)
    c: Coincident(g1,g2)
    c: Coincident(g2,g3)
    c: Coincident(g3,g4)
    c: Coincident(g4,g5)
    c: Coincident(g5,g0)
    c: Equal(g0, g1-g5) x5
    c: PointOnObject(g0,g6)
    c: PointOnObject(g1,g6)
    c: PointOnObject(g2,g6)
    c: PointOnObject(g3,g6)
    c: PointOnObject(g4,g6)
    c: PointOnObject(g5,g6)
    c: Coincident(g6,g-3)
    c: Coincident(g7,g8)
    c: Coincident(g8,g9)
    c: Coincident(g9,g10)
    c: Coincident(g10,g11)
    c: Coincident(g11,g12)
    c: Coincident(g12,g7)
    c: Equal(g7, g8-g12) x5
    c: PointOnObject(g7,g13)
    c: PointOnObject(g8,g13)
    c: PointOnObject(g9,g13)
    c: PointOnObject(g10,g13)
    c: PointOnObject(g11,g13)
    c: PointOnObject(g12,g13)
    c: Diameter(g6) = 6.1
    c: Diameter(g13) = 6.1
FEATURE [PartDesign::Pad] Pad111
  BaseFeature = -> Pocket130
  Direction = (0,0,-1)
  Length = 73.4
  Length2 = 10
  Placement = pos=(0,0,0) rot=(1,0,0;1.5708rad)
  Profile = -> Sketch274
  ReferenceAxis = -> Sketch274 [N_Axis]
  Type = 0
FEATURE [PartDesign::Body] Body001  label="Mirror"
  Group = -> [Sketch005,Revolution,Sketch262,Sketch265,Pad106,Sketch266,Pocket129,Sketch267,Pocket130,Sketch274,Pad111]
  Origin = -> Origin009
  Placement = pos=(0,0,-0.6) rot=(0,0,1;0rad)
  Tip = -> Pad111
FEATURE [App::Part] Part001  label="Mirror assembly"
  Group = -> [Body007,Body001,Body006]
  Origin = -> Origin025
  Placement = pos=(0,0,10) rot=(0,0,1;4.71239rad)
FEATURE [Sketcher::SketchObject] Sketch277
  FullyConstrained = true
  MapMode = 5
  Placement = pos=(0,0,0) rot=(1,0,0;1.5708rad)
  Support = -> [Pad059]
  sketch-geometry (1):
    g0: Circle CenterX=0 CenterY=0 CenterZ=0 NormalX=0 NormalY=0 NormalZ=1 AngleXU=0 Radius=2.25
  constraints (2):
    c: Coincident(g0,g-1)
    c: Diameter(g0) = 4.5
FEATURE [PartDesign::Pad] Pad114
  BaseFeature = -> Pad059
  Direction = (0,-1,2e-16)
  Length = 5
  Length2 = 10
  Placement = pos=(0,0,0) rot=(1,0,0;1.5708rad)
  Profile = -> Sketch277
  ReferenceAxis = -> Sketch277 [N_Axis]
  Type = 0
FEATURE [Sketcher::SketchObject] Sketch278
  FullyConstrained = true
  MapMode = 5
  Support = -> [XY_Plane365]
  sketch-geometry (11):
    g0: LineSegment StartX=13.4834 StartY=6.80799 StartZ=0 EndX=29.8226 EndY=-18.3521 EndZ=0
    g1: LineSegment StartX=-10 StartY=-11 StartZ=0 EndX=-10 EndY=-6 EndZ=0
    g2: LineSegment StartX=-10 StartY=-6 StartZ=0 EndX=-18 EndY=-6 EndZ=0
    g3: LineSegment StartX=-16 StartY=-4 StartZ=0 EndX=-3.15946 EndY=-4 EndZ=0
    g4: LineSegment StartX=10.07 StartY=-4.4605 StartZ=0 EndX=22.2745 EndY=-23.2539 EndZ=0
    g5: LineSegment StartX=22.2745 StartY=-23.2539 StartZ=0 EndX=29.8226 EndY=-18.3521 EndZ=0
    g6: LineSegment StartX=3 StartY=0 StartZ=0 EndX=13.4834 EndY=6.80799 EndZ=0
    g7: LineSegment StartX=-10 StartY=-11 StartZ=0 EndX=0 EndY=-11 EndZ=0
    g8: LineSegment StartX=0 StartY=-11 StartZ=0 EndX=10.07 EndY=-4.4605 EndZ=0
    g9: LineSegment StartX=-18 StartY=-6 StartZ=0 EndX=-16 EndY=-4 EndZ=0
    g10: LineSegment StartX=-3.15946 StartY=-4 StartZ=0 EndX=3 EndY=0 EndZ=0
  constraints (33):
    c: Vertical(g1)
    c: DistanceY(g1,g1) = 5
    c: Coincident(g2,g1)
    c: Horizontal(g2)
    c: DistanceX(g2,g2) = 8
    c: Coincident(g5,g4)
    c: Coincident(g5,g0)
    c: Perpendicular(g0,g5)
    c: Perpendicular(g4,g5)
    c: Distance(g0) = 30
    c: PointOnObject(g6,g-1)
    c: Coincident(g6,g0)
    c: Parallel(g6,g5)
    c: Distance(g5) = 9
    c: Coincident(g7,g1)
    c: Horizontal(g7)
    c: Coincident(g8,g7)
    c: Coincident(g4,g8)
    c: Parallel(g6,g8)
    c: DistanceX(g7,g7) = 10
    c: Distance(g6) = 12.5
    c: DistanceY(g1) = -6
    c: Coincident(g9,g2)
    c: Coincident(g9,g3)
    c: Angle(g9,g3) = 2.35619
    c: Horizontal(g3)
    c: Coincident(g10,g6)
    c: Parallel(g10,g6)
    c: DistanceX(g-1,g6) = 3
    c: Angle(g8,g7) = 2.56563
    c: DistanceY(g3,g-1) = 4
    c: Coincident(g3,g10)
    c: DistanceX(g1,g-1) = 10
FEATURE [PartDesign::Pad] Pad115
  Direction = (0,0,1)
  Length = 2.5
  Length2 = 10
  Profile = -> Sketch278
  ReferenceAxis = -> Sketch278 [N_Axis]
  Type = 0
FEATURE [Sketcher::SketchObject] Sketch284
  FullyConstrained = true
  MapMode = 5
  Placement = pos=(0,50.5,-5.7e-15) rot=(-1,0,0;1.5708rad)
  Support = -> [Pad114]
  sketch-geometry (1):
    g0: Circle CenterX=0 CenterY=0 CenterZ=0 NormalX=0 NormalY=0 NormalZ=1 AngleXU=0 Radius=2.25
  constraints (2):
    c: Coincident(g0,g-1)
    c: Diameter(g0) = 4.5
FEATURE [PartDesign::Pad] Pad119
  BaseFeature = -> Pad114
  Direction = (0,1,-2e-16)
  Length = 21
  Length2 = 10
  Placement = pos=(0,0,0) rot=(1,0,0;1.5708rad)
  Profile = -> Sketch284
  ReferenceAxis = -> Sketch284 [N_Axis]
  Type = 0
FEATURE [PartDesign::Body] Body035  label="Dribbler roll"
  Group = -> [Sketch083,Pad059,Sketch277,Pad114,Sketch284,Pad119]
  Origin = -> Origin238
  Placement = pos=(-76,30,1) rot=(1,0,0;3.14159rad)
  Tip = -> Pad119
FEATURE [Sketcher::SketchObject] Sketch285
  FullyConstrained = true
  MapMode = 5
  Support = -> [XY_Plane368]
  sketch-geometry (4):
    g0: LineSegment StartX=-65 StartY=10 StartZ=0 EndX=-32 EndY=10 EndZ=0
    g1: LineSegment StartX=-32 StartY=10 StartZ=0 EndX=-32 EndY=-10 EndZ=0
    g2: LineSegment StartX=-32 StartY=-10 StartZ=0 EndX=-65 EndY=-10 EndZ=0
    g3: LineSegment StartX=-65 StartY=-10 StartZ=0 EndX=-65 EndY=10 EndZ=0
  constraints (11):
    c: Coincident(g0,g1)
    c: Coincident(g1,g2)
    c: Coincident(g2,g3)
    c: Coincident(g3,g0)
    c: Horizontal(g0)
    c: Horizontal(g2)
    c: Vertical(g1)
    c: Symmetric(g2,g0,g-1)
    c: DistanceX(g0,g0) = 33
    c: DistanceY(g3,g3) = 20
    c: DistanceX(g0,g-1) = 32
FEATURE [PartDesign::Pad] Pad120
  Direction = (0,0,1)
  Length = 20
  Length2 = 10
  Profile = -> Sketch285
  ReferenceAxis = -> Sketch285 [N_Axis]
  Type = 0
FEATURE [PartDesign::Body] Body102  label="Kicker body"
  Group = -> [Sketch285,Pad120]
  Origin = -> Origin368
  Placement = pos=(-2,0,-18) rot=(0,0,1;0rad)
  Tip = -> Pad120
FEATURE [App::Part] Part013  label="Kicker"
  Group = -> [Body046,Body102]
  Origin = -> Origin249
  Placement = pos=(4,-2.9e-15,-23) rot=(1,0,0;3.14159rad)
FEATURE [Part::Cylinder] Cylinder  label="Cylindre"
  Angle = 360
  AttacherType = Attacher::AttachEngine3D
  FirstAngle = 0
  Height = 23
  Placement = pos=(-72,30,2) rot=(1,0,0;1.5708rad)
  Radius = 9
  SecondAngle = 0
FEATURE [Part::FeaturePython] Tube  # WARN: FeaturePython — macro-defined, semantics opaque (R4)
  AttacherType = Attacher::AttachEngine3D
  Height = 20.5
  InnerRadius = 8
  OuterRadius = 9
  Placement = pos=(-72,-7,2) rot=(0,0.707107,-0.707107;3.14159rad)
FEATURE [PartDesign::SubShapeBinder] Binder058
  BindCopyOnChange = 0
  BindMode = 0
  ClaimChildren = false
  Context = -> Part011 [Body121.Binder058.]
  Fuse = false
  MakeFace = true
  OffsetFill = false
  OffsetIntersection = false
  OffsetJoinType = 0
  OffsetOpenResult = false
  PartialLoad = false
  Relative = true
  _Version = 2
FEATURE [Sketcher::SketchObject] Sketch341
  FullyConstrained = true
  MapMode = 5
  Support = -> [XY_Plane405]
  sketch-geometry (11):
    g0: LineSegment StartX=13.4834 StartY=6.80799 StartZ=0 EndX=29.8226 EndY=-18.3521 EndZ=0
    g1: LineSegment StartX=-10 StartY=-17.5 StartZ=0 EndX=-10 EndY=-12.5 EndZ=0
    g2: LineSegment StartX=-10 StartY=-12.5 StartZ=0 EndX=-18 EndY=-12.5 EndZ=0
    g3: LineSegment StartX=-16 StartY=-10.5 StartZ=0 EndX=-13.1686 EndY=-10.5 EndZ=0
    g4: LineSegment StartX=10.3693 StartY=-4.92144 StartZ=0 EndX=22.2745 EndY=-23.2539 EndZ=0
    g5: LineSegment StartX=22.2745 StartY=-23.2539 StartZ=0 EndX=29.8226 EndY=-18.3521 EndZ=0
    g6: LineSegment StartX=3 StartY=0 StartZ=0 EndX=13.4834 EndY=6.80799 EndZ=0
    g7: LineSegment StartX=-10 StartY=-17.5 StartZ=0 EndX=-9 EndY=-17.5 EndZ=0
    g8: LineSegment StartX=-9 StartY=-17.5 StartZ=0 EndX=10.3693 EndY=-4.92144 EndZ=0
    g9: LineSegment StartX=-18 StartY=-12.5 StartZ=0 EndX=-16 EndY=-10.5 EndZ=0
    g10: LineSegment StartX=-13.1686 StartY=-10.5 StartZ=0 EndX=3 EndY=0 EndZ=0
  constraints (33):
    c: Vertical(g1)
    c: DistanceY(g1,g1) = 5
    c: Coincident(g2,g1)
    c: Horizontal(g2)
    c: DistanceX(g2,g2) = 8
    c: Coincident(g5,g4)
    c: Coincident(g5,g0)
    c: Perpendicular(g0,g5)
    c: Perpendicular(g4,g5)
    c: Distance(g0) = 30
    c: PointOnObject(g6,g-1)
    c: Coincident(g6,g0)
    c: Parallel(g6,g5)
    c: Distance(g5) = 9
    c: Coincident(g7,g1)
    c: Horizontal(g7)
    c: Coincident(g8,g7)
    c: Coincident(g4,g8)
    c: Parallel(g6,g8)
    c: DistanceX(g7,g7) = 1
    c: Distance(g6) = 12.5
    c: Coincident(g9,g2)
    c: Coincident(g9,g3)
    c: Angle(g9,g3) = 2.35619
    c: Horizontal(g3)
    c: Coincident(g10,g6)
    c: Parallel(g10,g6)
    c: DistanceX(g-1,g6) = 3
    c: Angle(g8,g7) = 2.56563
    c: DistanceY(g3,g-1) = 10.5
    c: Coincident(g3,g10)
    c: DistanceX(g1,g-1) = 10
    c: DistanceY(g2,g-1) = 12.5
FEATURE [PartDesign::Pad] Pad160
  Direction = (0,0,1)
  Length = 2.5
  Length2 = 10
  Profile = -> Sketch341
  ReferenceAxis = -> Sketch341 [N_Axis]
  Type = 0
FEATURE [PartDesign::Pocket] Pocket153
  BaseFeature = -> Pad160
  Direction = (1e-16,-2e-16,-1)
  Length = 5
  Length2 = 5
  Profile = -> Binder058
  Reversed = true
  Type = 1
FEATURE [Sketcher::SketchObject] Sketch342
  ExternalGeometry = -> [Pocket153]
  FullyConstrained = true
  MapMode = 5
  Placement = pos=(0,-12.5,0) rot=(1,0,0;1.5708rad)
  Support = -> [Pocket153]
  sketch-geometry (7):
    g0: LineSegment StartX=-18 StartY=4 StartZ=0 EndX=-10 EndY=4 EndZ=0
    g1: LineSegment StartX=-10 StartY=4 StartZ=0 EndX=-10 EndY=-4 EndZ=0
    g2: LineSegment StartX=-10 StartY=-4 StartZ=0 EndX=-18 EndY=-4 EndZ=0
    g3: LineSegment StartX=-18 StartY=-4 StartZ=0 EndX=-18 EndY=4 EndZ=0
    g4: Circle CenterX=-14 CenterY=5.46461e-11 CenterZ=0 NormalX=0 NormalY=0 NormalZ=1 AngleXU=0 Radius=2.5
    g5: LineSegment StartX=-10 StartY=-4 StartZ=0 EndX=-14 EndY=5.46461e-11 EndZ=0
    g6: LineSegment StartX=-14 StartY=5.46461e-11 StartZ=0 EndX=-18 EndY=-4 EndZ=0
  constraints (19):
    c: Coincident(g0,g1)
    c: Coincident(g1,g2)
    c: Coincident(g2,g3)
    c: Coincident(g3,g0)
    c: Horizontal(g0)
    c: Horizontal(g2)
    c: Vertical(g1)
    c: Vertical(g3)
    c: PointOnObject(g-3,g1)
    c: Equal(g3,g0)
    c: DistanceY(g2,g-3) = 6.5
    c: Diameter(g4) = 5
    c: Coincident(g5,g1)
    c: Coincident(g5,g4)
    c: Coincident(g6,g4)
    c: Coincident(g6,g2)
    c: Equal(g6,g5)
    c: Perpendicular(g5,g6)
    c: DistanceX(g2,g2) = 8
FEATURE [PartDesign::Pad] Pad161
  BaseFeature = -> Pocket153
  Direction = (0,-1,2e-16)
  Length = 5
  Length2 = 10
  Profile = -> Sketch342
  ReferenceAxis = -> Sketch342 [N_Axis]
  Type = 0
FEATURE [PartDesign::Body] Body121  label="Roll left support001"
  Group = -> [Sketch341,Pad160,Binder058,Pocket153,Sketch342,Pad161]
  Origin = -> Origin405
  Placement = pos=(-62,48,1) rot=(0,0,1;0rad)
  Tip = -> Pad161
FEATURE [Part::FeaturePython] Tube001  # WARN: FeaturePython — macro-defined, semantics opaque (R4)
  AttacherType = Attacher::AttachEngine3D
  Height = 14
  InnerRadius = 6
  OuterRadius = 10
  Placement = pos=(-76,7,1) rot=(1,0,0;1.5708rad)
FEATURE [Part::Cut] Cut
  Base = -> Body035
  Tool = -> Tube001
FEATURE [Sketcher::SketchObject] Sketch343
  FullyConstrained = false
  MapMode = 5
  Placement = pos=(0,-6,0) rot=(1,0,0;1.5708rad)
  sketch-geometry (7):
    g0: LineSegment StartX=-18 StartY=6.5 StartZ=0 EndX=-10 EndY=6.5 EndZ=0
    g1: LineSegment StartX=-10 StartY=6.5 StartZ=0 EndX=-10 EndY=-1.5 EndZ=0
    g2: LineSegment StartX=-10 StartY=-1.5 StartZ=0 EndX=-18 EndY=-1.5 EndZ=0
    g3: LineSegment StartX=-18 StartY=-1.5 StartZ=0 EndX=-18 EndY=6.5 EndZ=0
    g4: Circle CenterX=-14 CenterY=2.5 CenterZ=0 NormalX=0 NormalY=0 NormalZ=1 AngleXU=0 Radius=2.5
    g5: LineSegment StartX=-18 StartY=6.5 StartZ=0 EndX=-14 EndY=2.5 EndZ=0
    g6: LineSegment StartX=-14 StartY=2.5 StartZ=0 EndX=-10 EndY=-1.5 EndZ=0
  constraints (17):
    c: Coincident(g0,g1)
    c: Coincident(g1,g2)
    c: Coincident(g2,g3)
    c: Coincident(g3,g0)
    c: Horizontal(g0)
    c: Horizontal(g2)
    c: Vertical(g1)
    c: Vertical(g3)
    c: Equal(g2,g1)
    c: Diameter(g4) = 5
    c: Coincident(g5,g0)
    c: Coincident(g5,g4)
    c: Coincident(g6,g4)
    c: Coincident(g6,g1)
    c: Parallel(g5,g6)
    c: Equal(g5,g6)
    c: DistanceX(g2,g2) = 8
FEATURE [PartDesign::Pad] Pad162
  BaseFeature = -> Pad115
  Direction = (0,-1,2e-16)
  Length = 5
  Length2 = 10
  Profile = -> Sketch343
  ReferenceAxis = -> Sketch343 [N_Axis]
  Type = 0
FEATURE [PartDesign::SubShapeBinder] Binder059
  BindCopyOnChange = 0
  BindMode = 0
  ClaimChildren = false
  Context = -> Part011 [Body099.Binder059.]
  Fuse = false
  MakeFace = true
  OffsetFill = false
  OffsetIntersection = false
  OffsetJoinType = 0
  OffsetOpenResult = false
  PartialLoad = false
  Relative = true
  Support = -> [Part003[Part008.Body041.Pocket036.Sketch098.]]
  _Version = 2
FEATURE [PartDesign::Pocket] Pocket154
  BaseFeature = -> Pad162
  Direction = (-1e-16,2e-16,-1)
  Length = 5
  Length2 = 5
  Profile = -> Binder059
  Type = 1
FEATURE [PartDesign::Body] Body099  label="Roll right support001"
  Group = -> [Sketch278,Pad115,Sketch343,Pad162,Binder059,Pocket154]
  Origin = -> Origin365
  Placement = pos=(-62,-48,3.5) rot=(1,0,0;3.14159rad)
  Tip = -> Pocket154
FEATURE [App::Part] Part011  label="Dribbler"
  Group = -> [Body034,Body050,Body099,Body121,Body035,Cut,Tube001]
  Origin = -> Origin236
  Placement = pos=(4,0,1) rot=(0,0,1;0rad)
FEATURE [Part::Feature] Part__Feature442  label="114-00841-68--3DModel-STEP-56544 v004"
  Placement = pos=(24.0935,-0.00012972,0.814608) rot=(0.57735,0.57735,0.57735;2.0944rad)
  shape: bbox 10 x 11.95 x 1.48 mm, 267 faces (baked)
FEATURE [App::Part] _14_00841_68__3DModel_STEP_56544_v1  label="114-00841-68--3DModel-STEP-56544 v015"
  Group = -> [Part__Feature439,Part__Feature442]
  Origin = -> Origin052
FEATURE [App::Part] Teensy4_1_v22  label="Teensy 4.1 "
  Group = -> [_14_00841_68__3DModel_STEP_56544_v1,MIMXRT1052CVJ5B_v1,Part__Feature589,Pin_Header_1x6_TH_Pitch_2_54mm_v1,Pin_Header_1x6_TH_Pitch_2_54mm_v002,Pin_Header_1x6_TH_Pitch_2_54mm_v003,Pin_Header_1x6_TH_Pitch_2_54mm_v004,Pin_Header_1x6_TH_Pitch_2_54mm_v1_Mirror_,Pin_Header_1x6_TH_Pitch_2_54mm_v1_Mirror_001,Pin_Header_1x6_TH_Pitch_2_54mm_v1_Mirror_002,Pin_Header_1x6_TH_Pitch_2_54mm_v1_Mirror_003,+2 more]
  Origin = -> Origin050
  Placement = pos=(33.7332,-0.281902,31) rot=(0,0,-1;4.71239rad)
FEATURE [App::Part] Part  label="Main PCB"
  Group = -> [Body024,Teensy4_1_v22,HC05_Modulo]
  Origin = -> Origin077
  Placement = pos=(0,0,-8) rot=(0,0,1;0rad)
